FCSTD DOCUMENT  (FreeCAD 0.20R29410 (Git))
Label: lightModuleV2_2023_08_15
License: All rights reserved
LicenseURL: http://en.wikipedia.org/wiki/All_rights_reserved
objects: Part::Cylinder×122, Part::Feature×114, Part::MultiFuse×90, Sketcher::SketchObject×51, Part::Cut×49, Part::Extrusion×35, App::Part×14, Part::Box×12, Part::Fillet×11, Part::FeaturePython×10, Part::Loft×8, Part::Sphere×4, Mesh::Feature×2, Part::Compound×1, Part::Cone×1, Part::Compound2×1
note: 508 computed .brp shape members not serialized (recipe doc carries the construction recipe); baked Part::Feature solids carry a one-line shape summary decoded from their .brp

FEATURE [Mesh::Feature] Odroid_H004  label="Odroid-H004"
  Placement = pos=(15,-110,-70) rot=(0.57735,-0.57735,0.57735;4.18879rad)
FEATURE [Sketcher::SketchObject] Sketch  label="top"
  FullyConstrained = true
  sketch-geometry (24):
    g0: Circle CenterX=0 CenterY=-150 CenterZ=0 NormalX=0 NormalY=0 NormalZ=1 AngleXU=0 Radius=98
    g1: Circle CenterX=-92 CenterY=-150 CenterZ=0 NormalX=0 NormalY=0 NormalZ=1 AngleXU=0 Radius=2
    g2: Circle CenterX=-57 CenterY=-115 CenterZ=0 NormalX=0 NormalY=0 NormalZ=1 AngleXU=0 Radius=2
    g3: Circle CenterX=-22 CenterY=-150 CenterZ=0 NormalX=0 NormalY=0 NormalZ=1 AngleXU=0 Radius=2
    g4: Circle CenterX=-57 CenterY=-185 CenterZ=0 NormalX=0 NormalY=0 NormalZ=1 AngleXU=0 Radius=2
    g5: Circle CenterX=0 CenterY=-172 CenterZ=0 NormalX=0 NormalY=0 NormalZ=1 AngleXU=0 Radius=2
    g6: Circle CenterX=0 CenterY=-242 CenterZ=0 NormalX=0 NormalY=0 NormalZ=1 AngleXU=0 Radius=2
    g7: Circle CenterX=-35 CenterY=-207 CenterZ=0 NormalX=0 NormalY=0 NormalZ=1 AngleXU=0 Radius=2
    g8: Circle CenterX=35 CenterY=-207 CenterZ=0 NormalX=0 NormalY=0 NormalZ=1 AngleXU=0 Radius=2
    g9: Circle CenterX=57 CenterY=-185 CenterZ=0 NormalX=0 NormalY=0 NormalZ=1 AngleXU=0 Radius=2
    g10: Circle CenterX=22 CenterY=-150 CenterZ=0 NormalX=0 NormalY=0 NormalZ=1 AngleXU=0 Radius=2
    g11: Circle CenterX=57 CenterY=-115 CenterZ=0 NormalX=0 NormalY=0 NormalZ=1 AngleXU=0 Radius=2
    g12: Circle CenterX=92 CenterY=-150 CenterZ=0 NormalX=0 NormalY=0 NormalZ=1 AngleXU=0 Radius=2
    g13: Circle CenterX=0 CenterY=-58 CenterZ=0 NormalX=0 NormalY=0 NormalZ=1 AngleXU=0 Radius=2
    g14: Circle CenterX=0 CenterY=-207 CenterZ=0 NormalX=0 NormalY=0 NormalZ=1 AngleXU=0 Radius=25
    g15: Circle CenterX=57 CenterY=-150 CenterZ=0 NormalX=0 NormalY=0 NormalZ=1 AngleXU=0 Radius=25
    g16: Circle CenterX=0 CenterY=-93 CenterZ=0 NormalX=0 NormalY=0 NormalZ=1 AngleXU=0 Radius=25
    g17: Circle CenterX=-35 CenterY=-93 CenterZ=0 NormalX=0 NormalY=0 NormalZ=1 AngleXU=0 Radius=2
    g18: Circle CenterX=35 CenterY=-93 CenterZ=0 NormalX=0 NormalY=0 NormalZ=1 AngleXU=0 Radius=2
    g19: Circle CenterX=0 CenterY=-128 CenterZ=0 NormalX=0 NormalY=0 NormalZ=1 AngleXU=0 Radius=2
    g20: LineSegment StartX=-75.25 StartY=-129.25 StartZ=0 EndX=-38.75 EndY=-129.25 EndZ=0
    g21: LineSegment StartX=-38.75 StartY=-129.25 StartZ=0 EndX=-38.75 EndY=-170.75 EndZ=0
    g22: LineSegment StartX=-38.75 StartY=-170.75 StartZ=0 EndX=-75.25 EndY=-170.75 EndZ=0
    g23: LineSegment StartX=-75.25 StartY=-170.75 StartZ=0 EndX=-75.25 EndY=-129.25 EndZ=0
  constraints (72):
    c: PointOnObject(g0,g-2)
    c: Radius(g0) = 98
    c: DistanceY(g0) = -150
    c: PointOnObject(g5,g-2)
    c: PointOnObject(g6,g-2)
    c: PointOnObject(g13,g-2)
    c: PointOnObject(g19,g-2)
    c: Equal(g6,g7)
    c: Equal(g6,g4)
    c: Equal(g6,g1)
    c: Equal(g6,g2)
    c: Equal(g6,g3)
    c: Equal(g6,g19)
    c: Equal(g6,g5)
    c: Equal(g6,g8)
    c: Equal(g6,g9)
    c: Equal(g6,g10)
    c: Equal(g6,g12)
    c: Equal(g6,g11)
    c: Equal(g6,g17)
    c: Equal(g6,g18)
    c: Equal(g6,g13)
    c: Radius(g6) = 2
    c: DistanceY(g12,g0) = 0
    c: DistanceY(g10,g0) = 0
    c: DistanceY(g0,g3) = 0
    c: DistanceY(g1,g3) = 0
    c: Equal(g15,g14)
    c: Equal(g15,g16)
    c: Radius(g15) = 25
    c: Coincident(g20,g21)
    c: Coincident(g21,g22)
    c: Coincident(g22,g23)
    c: Coincident(g23,g20)
    c: Horizontal(g20)
    c: Horizontal(g22)
    c: Vertical(g21)
    c: Vertical(g23)
    c: DistanceX(g20) = -38.75
    c: DistanceY(g0,g20) = 20.75
    c: DistanceY(g21,g0) = 20.75
    c: DistanceX(g22,g0) = 75.25
    c: DistanceX(g14,g0) = 0
    c: DistanceX(g0,g15) = 57
    c: DistanceY(g15,g0) = 0
    c: DistanceY(g0,g16) = 57
    c: DistanceX(g16,g0) = 0
    c: DistanceX(g0,g10) = 22
    c: DistanceX(g3,g0) = 22
    c: DistanceX(g1,g0) = 92
    c: DistanceX(g15,g12) = 35
    c: DistanceX(g16,g18) = 35
    c: DistanceX(g17,g16) = 35
    c: DistanceX(g7,g14) = 35
    c: DistanceX(g14,g8) = 35
    c: DistanceX(g9,g15) = 0
    c: DistanceX(g15,g11) = 0
    c: DistanceX(g2,g0) = 57
    c: DistanceY(g18,g16) = 0
    c: DistanceY(g16,g17) = 0
    c: DistanceY(g19,g16) = 35
    c: DistanceY(g16,g13) = 35
    c: DistanceY(g4,g0) = 35
    c: DistanceY(g0,g2) = 35
    c: DistanceY(g14,g5) = 35
    c: DistanceY(g6,g14) = 35
    c: DistanceY(g8,g14) = 0
    c: DistanceY(g14,g7) = 0
    c: DistanceY(g9,g15) = 35
    c: DistanceY(g15,g11) = 35
    c: DistanceX(g4,g2) = 0
    c: DistanceY(g14,g0) = 57
FEATURE [Part::Cylinder] Cylinder036
  Angle = 360
  AttacherType = Attacher::AttachEngine3D
  FirstAngle = 0
  Height = 10
  Placement = pos=(0,-21,0) rot=(0,0,1;0rad)
  Radius = 2
  SecondAngle = 0
FEATURE [Part::Cylinder] Cylinder037
  Angle = 360
  AttacherType = Attacher::AttachEngine3D
  FirstAngle = 0
  Height = 10
  Placement = pos=(20,-21,0) rot=(0,0,1;0rad)
  Radius = 2
  SecondAngle = 0
FEATURE [Part::Cylinder] Cylinder038
  Angle = 360
  AttacherType = Attacher::AttachEngine3D
  FirstAngle = 0
  Height = 10
  Placement = pos=(0,-21,0) rot=(0,0,1;0rad)
  Radius = 2
  SecondAngle = 0
FEATURE [Part::Cylinder] Cylinder039
  Angle = 360
  AttacherType = Attacher::AttachEngine3D
  FirstAngle = 0
  Height = 10
  Placement = pos=(20,-21,0) rot=(0,0,1;0rad)
  Radius = 2
  SecondAngle = 0
FEATURE [Part::Cylinder] Cylinder040  label="base002"
  Angle = 360
  AttacherType = Attacher::AttachEngine3D
  FirstAngle = 0
  Height = 5
  Placement = pos=(5,0,70) rot=(0,0,1;0rad)
  Radius = 40
  SecondAngle = 0
FEATURE [Part::Cylinder] Cylinder041  label="baseCut001"
  Angle = 360
  AttacherType = Attacher::AttachEngine3D
  FirstAngle = 0
  Height = 7
  Placement = pos=(5,0,74) rot=(0,0,1;0rad)
  Radius = 24
  SecondAngle = 0
FEATURE [Part::Cylinder] Cylinder042  label="wireCUt002"
  Angle = 360
  AttacherType = Attacher::AttachEngine3D
  FirstAngle = 0
  Height = 10
  Placement = pos=(-5,0,70) rot=(0,0,1;0rad)
  Radius = 2
  SecondAngle = 0
FEATURE [Part::Cylinder] Cylinder043  label="wireCUt003"
  Angle = 360
  AttacherType = Attacher::AttachEngine3D
  FirstAngle = 0
  Height = 10
  Placement = pos=(15,0,70) rot=(0,0,1;0rad)
  Radius = 2
  SecondAngle = 0
FEATURE [Part::Cylinder] Cylinder044  label="m3Cuts002"
  Angle = 360
  AttacherType = Attacher::AttachEngine3D
  FirstAngle = 0
  Height = 10
  Placement = pos=(5,-9,70) rot=(0,0,1;0rad)
  Radius = 1.75
  SecondAngle = 0
FEATURE [Part::Cylinder] Cylinder045  label="m3Cuts003"
  Angle = 360
  AttacherType = Attacher::AttachEngine3D
  FirstAngle = 0
  Height = 10
  Placement = pos=(5,9,70) rot=(0,0,1;0rad)
  Radius = 1.75
  SecondAngle = 0
FEATURE [Part::Cylinder] Cylinder046  label="m2HeatSetInsets004"
  Angle = 360
  AttacherType = Attacher::AttachEngine3D
  FirstAngle = 0
  Height = 10
  Placement = pos=(-30,0,65) rot=(0,0,1;0rad)
  Radius = 1.6
  SecondAngle = 0
FEATURE [Part::Cylinder] Cylinder047  label="m2HeatSetInsets005"
  Angle = 360
  AttacherType = Attacher::AttachEngine3D
  FirstAngle = 0
  Height = 10
  Placement = pos=(40,0,65) rot=(0,0,1;0rad)
  Radius = 1.6
  SecondAngle = 0
FEATURE [Part::Cylinder] Cylinder048  label="m2HeatSetInsets006"
  Angle = 360
  AttacherType = Attacher::AttachEngine3D
  FirstAngle = 0
  Height = 10
  Placement = pos=(5,35,65) rot=(0,0,1;0rad)
  Radius = 1.6
  SecondAngle = 0
FEATURE [Part::Cylinder] Cylinder049  label="m2HeatSetInsets007"
  Angle = 360
  AttacherType = Attacher::AttachEngine3D
  FirstAngle = 0
  Height = 10
  Placement = pos=(5,-35,65) rot=(0,0,1;0rad)
  Radius = 1.6
  SecondAngle = 0
FEATURE [Part::MultiFuse] Fusion014  label="m3HeatSetCuts003"
  Placement = pos=(-5,38.5,70) rot=(0,0,1;0rad)
  Shapes = -> [Cylinder037,Cylinder036]
FEATURE [Part::MultiFuse] Fusion015  label="m3HeatSetCuts004"
  Placement = pos=(-5,3.5,70) rot=(0,0,1;0rad)
  Shapes = -> [Cylinder039,Cylinder038]
FEATURE [Part::MultiFuse] Fusion016  label="m3HeatSetCuts005"
  Shapes = -> [Fusion015,Fusion014]
FEATURE [Part::MultiFuse] Fusion017  label="wireCuts001"
  Shapes = -> [Cylinder042,Cylinder043]
FEATURE [Part::MultiFuse] Fusion018  label="m3Cute001"
  Shapes = -> [Cylinder044,Cylinder045]
FEATURE [Part::MultiFuse] Fusion019  label="baseCUts001"
  Shapes = -> [Fusion016,Fusion017,Fusion018]
FEATURE [Part::MultiFuse] Fusion021
  Shapes = -> [Cylinder046,Cylinder047,Cylinder048,Cylinder049]
FEATURE [Part::Sphere] Sphere002  label="SphereBase001"
  Angle1 = 0
  Angle2 = 12
  Angle3 = 360
  AttacherType = Attacher::AttachEngine3D
  Placement = pos=(5,0,74) rot=(0,0,1;0rad)
  Radius = 29
FEATURE [Part::Cut] Cut006
  Base = -> Sphere002
  Tool = -> Cylinder041
FEATURE [Part::MultiFuse] Fusion020  label="base003"
  Shapes = -> [Cylinder040,Cut006]
FEATURE [Part::Cut] Cut007
  Base = -> Fusion020
  Tool = -> Fusion019
FEATURE [Part::Cut] Cut008  label="lightModule001"
  Base = -> Cut007
  Placement = pos=(-5,-207,0) rot=(0,1,0;0rad)
  Tool = -> Fusion021
FEATURE [Part::Box] Box005  label="as7265x"
  AttacherType = Attacher::AttachEngine3D
  Height = 2
  Length = 36
  Placement = pos=(-75,-170.5,110) rot=(0,0,1;0rad)
  Width = 41
FEATURE [Part::Cylinder] Cylinder050
  Angle = 360
  AttacherType = Attacher::AttachEngine3D
  FirstAngle = 0
  Height = 10
  Placement = pos=(0,-21,0) rot=(0,0,1;0rad)
  Radius = 2
  SecondAngle = 0
FEATURE [Part::Cylinder] Cylinder051
  Angle = 360
  AttacherType = Attacher::AttachEngine3D
  FirstAngle = 0
  Height = 10
  Placement = pos=(20,-21,0) rot=(0,0,1;0rad)
  Radius = 2
  SecondAngle = 0
FEATURE [Part::Cylinder] Cylinder052
  Angle = 360
  AttacherType = Attacher::AttachEngine3D
  FirstAngle = 0
  Height = 10
  Placement = pos=(0,-21,0) rot=(0,0,1;0rad)
  Radius = 2
  SecondAngle = 0
FEATURE [Part::Cylinder] Cylinder053
  Angle = 360
  AttacherType = Attacher::AttachEngine3D
  FirstAngle = 0
  Height = 10
  Placement = pos=(20,-21,0) rot=(0,0,1;0rad)
  Radius = 2
  SecondAngle = 0
FEATURE [Part::Cylinder] Cylinder054  label="base004"
  Angle = 360
  AttacherType = Attacher::AttachEngine3D
  FirstAngle = 0
  Height = 5
  Placement = pos=(5,0,70) rot=(0,0,1;0rad)
  Radius = 40
  SecondAngle = 0
FEATURE [Part::Cylinder] Cylinder055  label="baseCut002"
  Angle = 360
  AttacherType = Attacher::AttachEngine3D
  FirstAngle = 0
  Height = 7
  Placement = pos=(5,0,74) rot=(0,0,1;0rad)
  Radius = 24
  SecondAngle = 0
FEATURE [Part::Cylinder] Cylinder056  label="wireCUt004"
  Angle = 360
  AttacherType = Attacher::AttachEngine3D
  FirstAngle = 0
  Height = 10
  Placement = pos=(-5,0,70) rot=(0,0,1;0rad)
  Radius = 2
  SecondAngle = 0
FEATURE [Part::Cylinder] Cylinder057  label="wireCUt005"
  Angle = 360
  AttacherType = Attacher::AttachEngine3D
  FirstAngle = 0
  Height = 10
  Placement = pos=(15,0,70) rot=(0,0,1;0rad)
  Radius = 2
  SecondAngle = 0
FEATURE [Part::Cylinder] Cylinder058  label="m3Cuts004"
  Angle = 360
  AttacherType = Attacher::AttachEngine3D
  FirstAngle = 0
  Height = 10
  Placement = pos=(5,-9,70) rot=(0,0,1;0rad)
  Radius = 1.75
  SecondAngle = 0
FEATURE [Part::Cylinder] Cylinder059  label="m3Cuts005"
  Angle = 360
  AttacherType = Attacher::AttachEngine3D
  FirstAngle = 0
  Height = 10
  Placement = pos=(5,9,70) rot=(0,0,1;0rad)
  Radius = 1.75
  SecondAngle = 0
FEATURE [Part::Cylinder] Cylinder060  label="m2HeatSetInsets008"
  Angle = 360
  AttacherType = Attacher::AttachEngine3D
  FirstAngle = 0
  Height = 10
  Placement = pos=(-30,0,65) rot=(0,0,1;0rad)
  Radius = 1.6
  SecondAngle = 0
FEATURE [Part::Cylinder] Cylinder061  label="m2HeatSetInsets009"
  Angle = 360
  AttacherType = Attacher::AttachEngine3D
  FirstAngle = 0
  Height = 10
  Placement = pos=(40,0,65) rot=(0,0,1;0rad)
  Radius = 1.6
  SecondAngle = 0
FEATURE [Part::Cylinder] Cylinder062  label="m2HeatSetInsets010"
  Angle = 360
  AttacherType = Attacher::AttachEngine3D
  FirstAngle = 0
  Height = 10
  Placement = pos=(5,35,65) rot=(0,0,1;0rad)
  Radius = 1.6
  SecondAngle = 0
FEATURE [Part::Cylinder] Cylinder063  label="m2HeatSetInsets011"
  Angle = 360
  AttacherType = Attacher::AttachEngine3D
  FirstAngle = 0
  Height = 10
  Placement = pos=(5,-35,65) rot=(0,0,1;0rad)
  Radius = 1.6
  SecondAngle = 0
FEATURE [Part::MultiFuse] Fusion022  label="m3HeatSetCuts006"
  Placement = pos=(-5,38.5,70) rot=(0,0,1;0rad)
  Shapes = -> [Cylinder051,Cylinder050]
FEATURE [Part::MultiFuse] Fusion023  label="m3HeatSetCuts007"
  Placement = pos=(-5,3.5,70) rot=(0,0,1;0rad)
  Shapes = -> [Cylinder053,Cylinder052]
FEATURE [Part::MultiFuse] Fusion024  label="m3HeatSetCuts008"
  Shapes = -> [Fusion023,Fusion022]
FEATURE [Part::MultiFuse] Fusion025  label="wireCuts002"
  Shapes = -> [Cylinder056,Cylinder057]
FEATURE [Part::MultiFuse] Fusion026  label="m3Cute002"
  Shapes = -> [Cylinder058,Cylinder059]
FEATURE [Part::MultiFuse] Fusion027  label="baseCUts002"
  Shapes = -> [Fusion024,Fusion025,Fusion026]
FEATURE [Part::MultiFuse] Fusion029
  Shapes = -> [Cylinder060,Cylinder061,Cylinder062,Cylinder063]
FEATURE [Part::Sphere] Sphere003  label="SphereBase002"
  Angle1 = 0
  Angle2 = 12
  Angle3 = 360
  AttacherType = Attacher::AttachEngine3D
  Placement = pos=(5,0,74) rot=(0,0,1;0rad)
  Radius = 29
FEATURE [Part::Cut] Cut009
  Base = -> Sphere003
  Tool = -> Cylinder055
FEATURE [Part::MultiFuse] Fusion028  label="base005"
  Shapes = -> [Cylinder054,Cut009]
FEATURE [Part::Cut] Cut010
  Base = -> Fusion028
  Tool = -> Fusion027
FEATURE [Part::Cut] Cut011  label="lightModule002"
  Base = -> Cut010
  Placement = pos=(-62,-150,0) rot=(0,1,0;0rad)
  Tool = -> Fusion029
FEATURE [Part::Cylinder] Cylinder064
  Angle = 360
  AttacherType = Attacher::AttachEngine3D
  FirstAngle = 0
  Height = 10
  Placement = pos=(0,-21,0) rot=(0,0,1;0rad)
  Radius = 2
  SecondAngle = 0
FEATURE [Part::Cylinder] Cylinder065
  Angle = 360
  AttacherType = Attacher::AttachEngine3D
  FirstAngle = 0
  Height = 10
  Placement = pos=(20,-21,0) rot=(0,0,1;0rad)
  Radius = 2
  SecondAngle = 0
FEATURE [Part::Cylinder] Cylinder066
  Angle = 360
  AttacherType = Attacher::AttachEngine3D
  FirstAngle = 0
  Height = 10
  Placement = pos=(0,-21,0) rot=(0,0,1;0rad)
  Radius = 2
  SecondAngle = 0
FEATURE [Part::Cylinder] Cylinder067
  Angle = 360
  AttacherType = Attacher::AttachEngine3D
  FirstAngle = 0
  Height = 10
  Placement = pos=(20,-21,0) rot=(0,0,1;0rad)
  Radius = 2
  SecondAngle = 0
FEATURE [Part::Cylinder] Cylinder068  label="base006"
  Angle = 360
  AttacherType = Attacher::AttachEngine3D
  FirstAngle = 0
  Height = 5
  Placement = pos=(5,0,70) rot=(0,0,1;0rad)
  Radius = 40
  SecondAngle = 0
FEATURE [Part::Cylinder] Cylinder069  label="baseCut003"
  Angle = 360
  AttacherType = Attacher::AttachEngine3D
  FirstAngle = 0
  Height = 7
  Placement = pos=(5,0,74) rot=(0,0,1;0rad)
  Radius = 24
  SecondAngle = 0
FEATURE [Part::Cylinder] Cylinder070  label="wireCUt006"
  Angle = 360
  AttacherType = Attacher::AttachEngine3D
  FirstAngle = 0
  Height = 10
  Placement = pos=(-5,0,70) rot=(0,0,1;0rad)
  Radius = 2
  SecondAngle = 0
FEATURE [Part::Cylinder] Cylinder071  label="wireCUt007"
  Angle = 360
  AttacherType = Attacher::AttachEngine3D
  FirstAngle = 0
  Height = 10
  Placement = pos=(15,0,70) rot=(0,0,1;0rad)
  Radius = 2
  SecondAngle = 0
FEATURE [Part::Cylinder] Cylinder072  label="m3Cuts006"
  Angle = 360
  AttacherType = Attacher::AttachEngine3D
  FirstAngle = 0
  Height = 10
  Placement = pos=(5,-9,70) rot=(0,0,1;0rad)
  Radius = 1.75
  SecondAngle = 0
FEATURE [Part::Cylinder] Cylinder073  label="m3Cuts007"
  Angle = 360
  AttacherType = Attacher::AttachEngine3D
  FirstAngle = 0
  Height = 10
  Placement = pos=(5,9,70) rot=(0,0,1;0rad)
  Radius = 1.75
  SecondAngle = 0
FEATURE [Part::Cylinder] Cylinder074  label="m2HeatSetInsets012"
  Angle = 360
  AttacherType = Attacher::AttachEngine3D
  FirstAngle = 0
  Height = 10
  Placement = pos=(-30,0,65) rot=(0,0,1;0rad)
  Radius = 1.6
  SecondAngle = 0
FEATURE [Part::Cylinder] Cylinder075  label="m2HeatSetInsets013"
  Angle = 360
  AttacherType = Attacher::AttachEngine3D
  FirstAngle = 0
  Height = 10
  Placement = pos=(40,0,65) rot=(0,0,1;0rad)
  Radius = 1.6
  SecondAngle = 0
FEATURE [Part::Cylinder] Cylinder076  label="m2HeatSetInsets014"
  Angle = 360
  AttacherType = Attacher::AttachEngine3D
  FirstAngle = 0
  Height = 10
  Placement = pos=(5,35,65) rot=(0,0,1;0rad)
  Radius = 1.6
  SecondAngle = 0
FEATURE [Part::Cylinder] Cylinder077  label="m2HeatSetInsets015"
  Angle = 360
  AttacherType = Attacher::AttachEngine3D
  FirstAngle = 0
  Height = 10
  Placement = pos=(5,-35,65) rot=(0,0,1;0rad)
  Radius = 1.6
  SecondAngle = 0
FEATURE [Part::MultiFuse] Fusion030  label="m3HeatSetCuts009"
  Placement = pos=(-5,38.5,70) rot=(0,0,1;0rad)
  Shapes = -> [Cylinder065,Cylinder064]
FEATURE [Part::MultiFuse] Fusion031  label="m3HeatSetCuts010"
  Placement = pos=(-5,3.5,70) rot=(0,0,1;0rad)
  Shapes = -> [Cylinder067,Cylinder066]
FEATURE [Part::MultiFuse] Fusion032  label="m3HeatSetCuts011"
  Shapes = -> [Fusion031,Fusion030]
FEATURE [Part::MultiFuse] Fusion033  label="wireCuts003"
  Shapes = -> [Cylinder070,Cylinder071]
FEATURE [Part::MultiFuse] Fusion034  label="m3Cute003"
  Shapes = -> [Cylinder072,Cylinder073]
FEATURE [Part::MultiFuse] Fusion035  label="baseCUts003"
  Shapes = -> [Fusion032,Fusion033,Fusion034]
FEATURE [Part::MultiFuse] Fusion037
  Shapes = -> [Cylinder074,Cylinder075,Cylinder076,Cylinder077]
FEATURE [Part::Sphere] Sphere004  label="SphereBase003"
  Angle1 = 0
  Angle2 = 12
  Angle3 = 360
  AttacherType = Attacher::AttachEngine3D
  Placement = pos=(5,0,74) rot=(0,0,1;0rad)
  Radius = 29
FEATURE [Part::Cut] Cut012
  Base = -> Sphere004
  Tool = -> Cylinder069
FEATURE [Part::MultiFuse] Fusion036  label="base007"
  Shapes = -> [Cylinder068,Cut012]
FEATURE [Part::Cut] Cut013
  Base = -> Fusion036
  Tool = -> Fusion035
FEATURE [Part::Cut] Cut014  label="lightModule003"
  Base = -> Cut013
  Placement = pos=(52,-150,0) rot=(0,1,0;0rad)
  Tool = -> Fusion037
FEATURE [Part::Cylinder] Cylinder078
  Angle = 360
  AttacherType = Attacher::AttachEngine3D
  FirstAngle = 0
  Height = 10
  Placement = pos=(0,-21,0) rot=(0,0,1;0rad)
  Radius = 2
  SecondAngle = 0
FEATURE [Part::Cylinder] Cylinder079
  Angle = 360
  AttacherType = Attacher::AttachEngine3D
  FirstAngle = 0
  Height = 10
  Placement = pos=(20,-21,0) rot=(0,0,1;0rad)
  Radius = 2
  SecondAngle = 0
FEATURE [Part::Cylinder] Cylinder080
  Angle = 360
  AttacherType = Attacher::AttachEngine3D
  FirstAngle = 0
  Height = 10
  Placement = pos=(0,-21,0) rot=(0,0,1;0rad)
  Radius = 2
  SecondAngle = 0
FEATURE [Part::Cylinder] Cylinder081
  Angle = 360
  AttacherType = Attacher::AttachEngine3D
  FirstAngle = 0
  Height = 10
  Placement = pos=(20,-21,0) rot=(0,0,1;0rad)
  Radius = 2
  SecondAngle = 0
FEATURE [Part::Cylinder] Cylinder082  label="base008"
  Angle = 360
  AttacherType = Attacher::AttachEngine3D
  FirstAngle = 0
  Height = 5
  Placement = pos=(5,0,70) rot=(0,0,1;0rad)
  Radius = 40
  SecondAngle = 0
FEATURE [Part::Cylinder] Cylinder083  label="baseCut004"
  Angle = 360
  AttacherType = Attacher::AttachEngine3D
  FirstAngle = 0
  Height = 7
  Placement = pos=(5,0,74) rot=(0,0,1;0rad)
  Radius = 24
  SecondAngle = 0
FEATURE [Part::Cylinder] Cylinder084  label="wireCUt008"
  Angle = 360
  AttacherType = Attacher::AttachEngine3D
  FirstAngle = 0
  Height = 10
  Placement = pos=(-5,0,70) rot=(0,0,1;0rad)
  Radius = 2
  SecondAngle = 0
FEATURE [Part::Cylinder] Cylinder085  label="wireCUt009"
  Angle = 360
  AttacherType = Attacher::AttachEngine3D
  FirstAngle = 0
  Height = 10
  Placement = pos=(15,0,70) rot=(0,0,1;0rad)
  Radius = 2
  SecondAngle = 0
FEATURE [Part::Cylinder] Cylinder086  label="m3Cuts008"
  Angle = 360
  AttacherType = Attacher::AttachEngine3D
  FirstAngle = 0
  Height = 10
  Placement = pos=(5,-9,70) rot=(0,0,1;0rad)
  Radius = 1.75
  SecondAngle = 0
FEATURE [Part::Cylinder] Cylinder087  label="m3Cuts009"
  Angle = 360
  AttacherType = Attacher::AttachEngine3D
  FirstAngle = 0
  Height = 10
  Placement = pos=(5,9,70) rot=(0,0,1;0rad)
  Radius = 1.75
  SecondAngle = 0
FEATURE [Part::Cylinder] Cylinder088  label="m2HeatSetInsets016"
  Angle = 360
  AttacherType = Attacher::AttachEngine3D
  FirstAngle = 0
  Height = 10
  Placement = pos=(-30,0,65) rot=(0,0,1;0rad)
  Radius = 1.6
  SecondAngle = 0
FEATURE [Part::Cylinder] Cylinder089  label="m2HeatSetInsets017"
  Angle = 360
  AttacherType = Attacher::AttachEngine3D
  FirstAngle = 0
  Height = 10
  Placement = pos=(40,0,65) rot=(0,0,1;0rad)
  Radius = 1.6
  SecondAngle = 0
FEATURE [Part::Cylinder] Cylinder090  label="m2HeatSetInsets018"
  Angle = 360
  AttacherType = Attacher::AttachEngine3D
  FirstAngle = 0
  Height = 10
  Placement = pos=(5,35,65) rot=(0,0,1;0rad)
  Radius = 1.6
  SecondAngle = 0
FEATURE [Part::Cylinder] Cylinder091  label="m2HeatSetInsets019"
  Angle = 360
  AttacherType = Attacher::AttachEngine3D
  FirstAngle = 0
  Height = 10
  Placement = pos=(5,-35,65) rot=(0,0,1;0rad)
  Radius = 1.6
  SecondAngle = 0
FEATURE [Part::MultiFuse] Fusion038  label="m3HeatSetCuts012"
  Placement = pos=(-5,38.5,70) rot=(0,0,1;0rad)
  Shapes = -> [Cylinder079,Cylinder078]
FEATURE [Part::MultiFuse] Fusion039  label="m3HeatSetCuts013"
  Placement = pos=(-5,3.5,70) rot=(0,0,1;0rad)
  Shapes = -> [Cylinder081,Cylinder080]
FEATURE [Part::MultiFuse] Fusion040  label="m3HeatSetCuts014"
  Shapes = -> [Fusion039,Fusion038]
FEATURE [Part::MultiFuse] Fusion041  label="wireCuts004"
  Shapes = -> [Cylinder084,Cylinder085]
FEATURE [Part::MultiFuse] Fusion042  label="m3Cute004"
  Shapes = -> [Cylinder086,Cylinder087]
FEATURE [Part::MultiFuse] Fusion043  label="baseCUts004"
  Shapes = -> [Fusion040,Fusion041,Fusion042]
FEATURE [Part::MultiFuse] Fusion045
  Shapes = -> [Cylinder088,Cylinder089,Cylinder090,Cylinder091]
FEATURE [Part::Sphere] Sphere005  label="SphereBase004"
  Angle1 = 0
  Angle2 = 12
  Angle3 = 360
  AttacherType = Attacher::AttachEngine3D
  Placement = pos=(5,0,74) rot=(0,0,1;0rad)
  Radius = 29
FEATURE [Part::Cut] Cut015
  Base = -> Sphere005
  Tool = -> Cylinder083
FEATURE [Part::MultiFuse] Fusion044  label="base009"
  Shapes = -> [Cylinder082,Cut015]
FEATURE [Part::Cut] Cut016
  Base = -> Fusion044
  Tool = -> Fusion043
FEATURE [Part::Cut] Cut017  label="lightModule004"
  Base = -> Cut016
  Placement = pos=(-5,-93,0) rot=(0,1,0;0rad)
  Tool = -> Fusion045
FEATURE [Part::MultiFuse] Fusion  label="lightModules"
  Placement = pos=(0,0,30) rot=(0,0,1;0rad)
  Shapes = -> [Cut008,Cut011,Cut014,Cut017]
FEATURE [Part::Extrusion] Extrude  label="top001"
  Base = -> Sketch
  Dir = (0,0,1)
  DirMode = 2
  FaceMakerClass = Part::FaceMakerBullseye
  LengthFwd = 5
  LengthRev = 0
  Placement = pos=(0,0,100) rot=(0,0,1;0rad)
  Solid = true
  Symmetric = false
FEATURE [Part::Feature] Part__Feature  label="elpCamera"
  Placement = pos=(57,-150,90) rot=(0,0,1;0rad)
  shape: bbox 38 x 38 x 25.12 mm, 164 faces (baked)
FEATURE [Part::FeaturePython] Tube  label="tube001"  # WARN: FeaturePython — macro-defined, semantics opaque (R4)
  AttacherType = Attacher::AttachEngine3D
  Height = 20
  InnerRadius = 94
  OuterRadius = 98
  Placement = pos=(0,-150,80) rot=(0,0,1;0rad)
FEATURE [Part::Feature] Part__Feature010  label="veml6075_sensor"
  Placement = pos=(0,-92,105) rot=(0,0,1;0rad)
  shape: bbox 15.31 x 17.01 x 46.02 mm, 450 faces (baked)
FEATURE [Sketcher::SketchObject] Sketch001
  FullyConstrained = true
  Placement = pos=(0,0,105) rot=(0,0,1;0rad)
  sketch-geometry (14):
    g0: Circle CenterX=0 CenterY=-93 CenterZ=0 NormalX=0 NormalY=0 NormalZ=1 AngleXU=0 Radius=25
    g1: Circle CenterX=0 CenterY=-93 CenterZ=0 NormalX=0 NormalY=0 NormalZ=1 AngleXU=0 Radius=26.5
    g2: Circle CenterX=57 CenterY=-150 CenterZ=0 NormalX=0 NormalY=0 NormalZ=1 AngleXU=0 Radius=25
    g3: Circle CenterX=57 CenterY=-150 CenterZ=0 NormalX=0 NormalY=0 NormalZ=1 AngleXU=0 Radius=26.5
    g4: Circle CenterX=0 CenterY=-207 CenterZ=0 NormalX=0 NormalY=0 NormalZ=1 AngleXU=0 Radius=25
    g5: Circle CenterX=0 CenterY=-207 CenterZ=0 NormalX=0 NormalY=0 NormalZ=1 AngleXU=0 Radius=26.5
    g6: LineSegment StartX=-75.25 StartY=-129.25 StartZ=0 EndX=-38.75 EndY=-129.25 EndZ=0
    g7: LineSegment StartX=-38.75 StartY=-129.25 StartZ=0 EndX=-38.75 EndY=-170.75 EndZ=0
    g8: LineSegment StartX=-38.75 StartY=-170.75 StartZ=0 EndX=-75.25 EndY=-170.75 EndZ=0
    g9: LineSegment StartX=-75.25 StartY=-170.75 StartZ=0 EndX=-75.25 EndY=-129.25 EndZ=0
    g10: LineSegment StartX=-75.7 StartY=-128.8 StartZ=0 EndX=-38.3 EndY=-128.8 EndZ=0
    g11: LineSegment StartX=-38.3 StartY=-128.8 StartZ=0 EndX=-38.3 EndY=-171.2 EndZ=0
    g12: LineSegment StartX=-38.3 StartY=-171.2 StartZ=0 EndX=-75.7 EndY=-171.2 EndZ=0
    g13: LineSegment StartX=-75.7 StartY=-171.2 StartZ=0 EndX=-75.7 EndY=-128.8 EndZ=0
  constraints (39):
    c: PointOnObject(g0,g-2)
    c: Coincident(g1,g0)
    c: Coincident(g3,g2)
    c: PointOnObject(g4,g-2)
    c: Coincident(g5,g4)
    c: Coincident(g6,g7)
    c: Coincident(g7,g8)
    c: Coincident(g8,g9)
    c: Coincident(g9,g6)
    c: Horizontal(g6)
    c: Horizontal(g8)
    c: Vertical(g7)
    c: Vertical(g9)
    c: DistanceY(g0) = -93
    c: DistanceY(g2) = -150
    c: DistanceX(g2) = 57
    c: Equal(g0,g2)
    c: Equal(g0,g4)
    c: Radius(g0) = 25
    c: Equal(g3,g1)
    c: Equal(g3,g5)
    c: Radius(g3) = 26.5
    c: DistanceY(g4) = -207
    c: DistanceY(g7) = -170.75
    c: DistanceX(g7) = -38.75
    c: DistanceX(g6) = -75.25
    c: DistanceY(g6) = -129.25
    c: Coincident(g10,g11)
    c: Coincident(g11,g12)
    c: Coincident(g12,g13)
    c: Coincident(g13,g10)
    c: Horizontal(g10)
    c: Horizontal(g12)
    c: Vertical(g11)
    c: Vertical(g13)
    c: DistanceY(g11,g7) = 0.45
    c: DistanceX(g7,g11) = 0.45
    c: DistanceX(g10,g6) = 0.45
    c: DistanceY(g6,g10) = 0.45
FEATURE [Part::Extrusion] Extrude001
  Base = -> Sketch001
  Dir = (0,0,1)
  DirMode = 2
  FaceMakerClass = Part::FaceMakerBullseye
  LengthFwd = 1
  LengthRev = 0
  Solid = true
  Symmetric = false
FEATURE [Part::MultiFuse] Fusion046  label="top002"
  Shapes = -> [Extrude001,Extrude]
FEATURE [Part::Cylinder] Cylinder
  Angle = 360
  AttacherType = Attacher::AttachEngine3D
  FirstAngle = 0
  Height = 300
  Placement = pos=(0,0,90) rot=(1,0,0;1.5708rad)
  Radius = 2.2
  SecondAngle = 0
FEATURE [Part::Cylinder] Cylinder092
  Angle = 360
  AttacherType = Attacher::AttachEngine3D
  FirstAngle = 0
  Height = 300
  Placement = pos=(-150,-150,90) rot=(0.57735,0.57735,0.57735;2.0944rad)
  Radius = 2.2
  SecondAngle = 0
FEATURE [Part::MultiFuse] Fusion047  label="m4Cuts"
  Shapes = -> [Cylinder092,Cylinder]
FEATURE [Part::Fillet] Fillet  label="top003"
  Base = -> Fusion046
  Edges = 1 edges r=2: [Edge3]
FEATURE [Part::Fillet] Fillet001  label="tube"
  Base = -> Tube
  Edges = 1 edges r=2: [Edge5]
FEATURE [Part::MultiFuse] Fusion048  label="top004"
  Shapes = -> [Fillet,Fillet001]
FEATURE [Part::Cut] Cut  label="top005"
  Base = -> Fusion048
  Tool = -> Fusion047
FEATURE [Part::Cylinder] Cylinder094  label="refModules"
  Angle = 360
  AttacherType = Attacher::AttachEngine3D
  FirstAngle = 0
  Height = 75
  Placement = pos=(0,-207,37) rot=(0,0,1;0rad)
  Radius = 3.75
  SecondAngle = 0
FEATURE [Part::Cylinder] Cylinder095  label="refModulesCoverCut"
  Angle = 360
  AttacherType = Attacher::AttachEngine3D
  FirstAngle = 0
  Height = 60
  Placement = pos=(0,-207,37) rot=(0,0,1;0rad)
  Radius = 4.5
  SecondAngle = 0
FEATURE [Sketcher::SketchObject] Sketch002
  FullyConstrained = true
  sketch-geometry (16):
    g0: Circle CenterX=-67 CenterY=-167.5 CenterZ=0 NormalX=0 NormalY=0 NormalZ=1 AngleXU=0 Radius=1.625
    g1: Circle CenterX=-47 CenterY=-167.5 CenterZ=0 NormalX=0 NormalY=0 NormalZ=1 AngleXU=0 Radius=1.625
    g2: Circle CenterX=-67 CenterY=-132.5 CenterZ=0 NormalX=0 NormalY=0 NormalZ=1 AngleXU=0 Radius=1.625
    g3: Circle CenterX=-47 CenterY=-132.5 CenterZ=0 NormalX=0 NormalY=0 NormalZ=1 AngleXU=0 Radius=1.625
    g4: LineSegment StartX=-62 StartY=-129.75 StartZ=0 EndX=-72 EndY=-129.75 EndZ=0
    g5: LineSegment StartX=-52 StartY=-129.75 StartZ=0 EndX=-42 EndY=-129.75 EndZ=0
    g6: LineSegment StartX=-72 StartY=-129.75 StartZ=0 EndX=-72 EndY=-170.25 EndZ=0
    g7: LineSegment StartX=-72 StartY=-170.25 StartZ=0 EndX=-62 EndY=-170.25 EndZ=0
    g8: LineSegment StartX=-62 StartY=-170.25 StartZ=0 EndX=-62 EndY=-155 EndZ=0
    g9: LineSegment StartX=-52 StartY=-155 StartZ=0 EndX=-52 EndY=-170.25 EndZ=0
    g10: LineSegment StartX=-52 StartY=-170.25 StartZ=0 EndX=-42 EndY=-170.25 EndZ=0
    g11: LineSegment StartX=-42 StartY=-170.25 StartZ=0 EndX=-42 EndY=-129.75 EndZ=0
    g12: LineSegment StartX=-62 StartY=-155 StartZ=0 EndX=-52 EndY=-155 EndZ=0
    g13: LineSegment StartX=-62 StartY=-129.75 StartZ=0 EndX=-62 EndY=-145 EndZ=0
    g14: LineSegment StartX=-62 StartY=-145 StartZ=0 EndX=-52 EndY=-145 EndZ=0
    g15: LineSegment StartX=-52 StartY=-145 StartZ=0 EndX=-52 EndY=-129.75 EndZ=0
  constraints (48):
    c: DistanceY(g2,g3) = 0
    c: DistanceX(g0,g2) = 0
    c: DistanceX(g1,g3) = 0
    c: DistanceX(g1) = -47
    c: DistanceY(g1) = -167.5
    c: DistanceX(g0,g1) = 20
    c: Horizontal(g4)
    c: Horizontal(g5)
    c: Vertical(g6)
    c: Coincident(g7,g6)
    c: Horizontal(g7)
    c: Coincident(g8,g7)
    c: Vertical(g9)
    c: Coincident(g10,g9)
    c: Horizontal(g10)
    c: Coincident(g11,g10)
    c: Vertical(g8)
    c: DistanceX(g4,g4) = 10
    c: DistanceX(g5,g5) = 10
    c: DistanceX(g6,g7) = 10
    c: DistanceX(g9,g10) = 10
    c: Vertical(g11)
    c: DistanceY(g7,g9) = 0
    c: DistanceY(g4,g5) = 0
    c: DistanceX(g6,g0) = 5
    c: DistanceX(g9,g1) = 5
    c: DistanceY(g2,g4) = 2.75
    c: Coincident(g4,g6)
    c: Coincident(g12,g8)
    c: Horizontal(g12)
    c: Coincident(g9,g12)
    c: Coincident(g13,g4)
    c: Vertical(g13)
    c: Coincident(g14,g13)
    c: Horizontal(g14)
    c: Coincident(g15,g14)
    c: Coincident(g15,g5)
    c: Vertical(g15)
    c: Coincident(g5,g11)
    c: DistanceY(g8,g13) = 10
    c: DistanceY(g13) = -145
    c: DistanceY(g7,g0) = 2.75
    c: Equal(g1,g0)
    c: Equal(g1,g2)
    c: Equal(g1,g3)
    c: Diameter(g1) = 3.25
    c: DistanceY(g1,g0) = 0
    c: DistanceY(g2) = -132.5
FEATURE [Sketcher::SketchObject] Sketch003
  FullyConstrained = true
  sketch-geometry (6):
    g0: Circle CenterX=74 CenterY=-167 CenterZ=0 NormalX=0 NormalY=0 NormalZ=1 AngleXU=0 Radius=1.65
    g1: Circle CenterX=40 CenterY=-167 CenterZ=0 NormalX=0 NormalY=0 NormalZ=1 AngleXU=0 Radius=1.65
    g2: Circle CenterX=40 CenterY=-133 CenterZ=0 NormalX=0 NormalY=0 NormalZ=1 AngleXU=0 Radius=1.65
    g3: Circle CenterX=74 CenterY=-133 CenterZ=0 NormalX=0 NormalY=0 NormalZ=1 AngleXU=0 Radius=1.65
    g4: Circle CenterX=57 CenterY=-150 CenterZ=0 NormalX=0 NormalY=0 NormalZ=1 AngleXU=0 Radius=27.5
    g5: Circle CenterX=57 CenterY=-150 CenterZ=0 NormalX=0 NormalY=0 NormalZ=1 AngleXU=0 Radius=21
  constraints (17):
    c: Equal(g3,g0)
    c: Equal(g3,g1)
    c: Equal(g3,g2)
    c: Diameter(g3) = 3.3
    c: DistanceX(g1) = 40
    c: DistanceY(g1) = -167
    c: DistanceY(g1,g0) = 0
    c: DistanceX(g2,g1) = 0
    c: DistanceY(g1,g2) = 34
    c: DistanceY(g2,g3) = 0
    c: DistanceX(g2,g3) = 34
    c: DistanceX(g0,g3) = 0
    c: Coincident(g5,g4)
    c: DistanceX(g4) = 57
    c: DistanceY(g4) = -150
    c: Diameter(g5) = 42
    c: Diameter(g4) = 55
FEATURE [Part::Feature] Part__Feature105  label="Printed Circuit Board"
  shape: bbox 25.4 x 17.78 x 1.6 mm, 42 faces (baked)
FEATURE [Part::Feature] Part__Feature106  label="EAHC2835WD6"
  shape: bbox 3.513 x 2.813 x 0.7485 mm, 108 faces, 4 solids (baked)
FEATURE [Part::Feature] Part__Feature107  label="AS7341 v2"
  Placement = pos=(0,-0.339822,1.6) rot=(0,0,1;0rad)
  shape: bbox 2 x 3.1 x 1.1 mm, 267 faces, 26 solids (baked)
FEATURE [Part::Feature] Part__Feature108  label="CAPC-0805-T0.95-BN v1"
  Placement = pos=(-5.01759,-3.15294,1.6) rot=(0,0,1;0rad)
  shape: bbox 2.1 x 1.35 x 0.95 mm, 42 faces (baked)
FEATURE [Part::Feature] Part__Feature109  label="CAPC-0805-T0.95-BN v002"
  Placement = pos=(-5.48627,2.66154,1.6) rot=(0,0,-1;1.5708rad)
  shape: bbox 1.35 x 2.1 x 0.95 mm, 42 faces (baked)
FEATURE [Part::Feature] Part__Feature110  label="CAPC-0805-T0.95-BN v003"
  Placement = pos=(-3.43627,2.66154,1.6) rot=(0,0,-1;1.5708rad)
  shape: bbox 1.35 x 2.1 x 0.95 mm, 42 faces (baked)
FEATURE [Part::Feature] Part__Feature111  label="CAPC-0603-T0.9-BN v1"
  Placement = pos=(-1.69987,-3.28475,1.6) rot=(0,0,1;0rad)
  shape: bbox 1.7 x 0.9 x 0.9 mm, 42 faces (baked)
FEATURE [Part::Feature] Part__Feature112  label="BODY_MF06A"
  Placement = pos=(0,0,0.762) rot=(0.57735,-0.57735,-0.57735;2.0944rad)
  shape: bbox 1.601 x 2.921 x 1.016 mm, 42 faces (baked)
FEATURE [Part::Feature] Part__Feature113  label="LEAD_MF06A"
  Placement = pos=(-0.9652,-0.9525,0.1016) rot=(0.57735,-0.57735,-0.57735;2.0944rad)
  shape: bbox 0.6223 x 0.3749 x 0.8636 mm, 14 faces (baked)
FEATURE [Part::Feature] Part__Feature114  label="LEAD_MF06A001"
  Placement = pos=(-0.9652,0,0.1016) rot=(0.57735,-0.57735,-0.57735;2.0944rad)
  shape: bbox 0.6223 x 0.3749 x 0.8636 mm, 14 faces (baked)
FEATURE [Part::Feature] Part__Feature115  label="LEAD_MF06A002"
  Placement = pos=(-0.9652,0.9525,0.1016) rot=(0.57735,-0.57735,-0.57735;2.0944rad)
  shape: bbox 0.6223 x 0.3749 x 0.8636 mm, 14 faces (baked)
FEATURE [Part::Feature] Part__Feature116  label="LEAD_MF06A003"
  Placement = pos=(0.9652,-0.9525,0.1016) rot=(0.57735,0.57735,0.57735;2.0944rad)
  shape: bbox 0.6223 x 0.3749 x 0.8636 mm, 14 faces (baked)
FEATURE [Part::Feature] Part__Feature117  label="LEAD_MF06A004"
  Placement = pos=(0.9652,0,0.1016) rot=(0.57735,0.57735,0.57735;2.0944rad)
  shape: bbox 0.6223 x 0.3749 x 0.8636 mm, 14 faces (baked)
FEATURE [Part::Feature] Part__Feature118  label="LEAD_MF06A005"
  Placement = pos=(0.9652,0.9525,0.1016) rot=(0.57735,0.57735,0.57735;2.0944rad)
  shape: bbox 0.6223 x 0.3749 x 0.8636 mm, 14 faces (baked)
FEATURE [Part::Feature] Part__Feature119  label="SOT363 v2"
  Placement = pos=(4.97054,-0.645171,1.675) rot=(0,0,1;3.14159rad)
  shape: bbox 2.1 x 2 x 1.1 mm, 94 faces, 7 solids (baked)
FEATURE [Part::Feature] Part__Feature120  label="LED 0603 single color v1"
  Placement = pos=(-9.18406,3.72778,1.60762) rot=(0,0,1;1.5708rad)
  shape: bbox 1.961 x 0.7932 x 0.7145 mm, 63 faces, 5 solids (baked)
FEATURE [Part::Feature] Part__Feature121  label="RESC-0603 v1"
  Placement = pos=(4.83432,-3.67461,1.6) rot=(0,0,1;0rad)
  shape: bbox 1.7 x 0.9 x 0.55 mm, 52 faces, 3 solids (baked)
FEATURE [Part::Feature] Part__Feature122  label="RESC-0603 v002"
  Placement = pos=(-7.14949,3.61248,1.6) rot=(0,0,-1;1.5708rad)
  shape: bbox 0.9 x 1.7 x 0.55 mm, 52 faces, 3 solids (baked)
FEATURE [Part::Feature] Part__Feature123  label="YC164_RESPACK v1"
  Placement = pos=(2.99591,1.52916,1.6) rot=(0,0,1;0rad)
  shape: bbox 3.2 x 1.6 x 0.61 mm, 172 faces (baked)
FEATURE [Part::Feature] Part__Feature124  label="qwicc v2"
  Placement = pos=(-10.8364,0.0607456,1.65) rot=(0,0,-1;1.5708rad)
  shape: bbox 4.95 x 6 x 2.96 mm, 229 faces, 7 solids (baked)
FEATURE [Part::Feature] Part__Feature125  label="qwicc v003"
  Placement = pos=(10.8256,0.00556102,1.65) rot=(0,0,1;1.5708rad)
  shape: bbox 4.95 x 6 x 2.96 mm, 229 faces, 7 solids (baked)
FEATURE [App::Part] sot_23_6_v2  label="sot-23-6 v2"
  Group = -> [Part__Feature112,Part__Feature113,Part__Feature114,Part__Feature115,Part__Feature116,Part__Feature117,Part__Feature118]
  Origin = -> Origin008
  Placement = pos=(-4.47945,-0.603742,1.69152) rot=(0,0,1;0rad)
FEATURE [App::Part] Adafruit_AS7341_STEMMA_QT_v2  label="ltr390"
  Group = -> [Part__Feature105,Part__Feature106,Part__Feature107,Part__Feature108,Part__Feature109,Part__Feature110,Part__Feature111,sot_23_6_v2,Part__Feature119,Part__Feature120,Part__Feature121,Part__Feature122,Part__Feature123,Part__Feature124,Part__Feature125]
  Origin = -> Origin009
  Placement = pos=(0,-98,110) rot=(0,0,1;0rad)
FEATURE [Part::Box] Box  label="guva"
  AttacherType = Attacher::AttachEngine3D
  Height = 2
  Length = 19
  Placement = pos=(-9.5,-88,0) rot=(0,0,1;0rad)
  Width = 10
FEATURE [Part::Cylinder] Cylinder098
  Angle = 360
  AttacherType = Attacher::AttachEngine3D
  FirstAngle = 0
  Height = 10
  Placement = pos=(6.5,-83,0) rot=(0,0,1;0rad)
  Radius = 1.13
  SecondAngle = 0
FEATURE [Part::Cut] Cut018  label="guva001"
  Base = -> Box
  Placement = pos=(0,0,110) rot=(0,0,1;0rad)
  Tool = -> Cylinder098
FEATURE [Sketcher::SketchObject] Sketch004
  FullyConstrained = true
  sketch-geometry (11):
    g0: Circle CenterX=6.5 CenterY=-83 CenterZ=0 NormalX=0 NormalY=0 NormalZ=1 AngleXU=0 Radius=1.125
    g1: Circle CenterX=10.15 CenterY=-91.65 CenterZ=0 NormalX=0 NormalY=0 NormalZ=1 AngleXU=0 Radius=1.125
    g2: Circle CenterX=10.15 CenterY=-104.35 CenterZ=0 NormalX=0 NormalY=0 NormalZ=1 AngleXU=0 Radius=1.125
    g3: Circle CenterX=-10.15 CenterY=-104.35 CenterZ=0 NormalX=0 NormalY=0 NormalZ=1 AngleXU=0 Radius=1.125
    g4: Circle CenterX=-10.15 CenterY=-91.65 CenterZ=0 NormalX=0 NormalY=0 NormalZ=1 AngleXU=0 Radius=1.125
    g5: ArcOfCircle CenterX=-9.5 CenterY=-78 CenterZ=0 NormalX=0 NormalY=0 NormalZ=1 AngleXU=0 Radius=9.5 StartAngle=4.71239 EndAngle=6.28319
    g6: LineSegment StartX=-9.5 StartY=-87.5 StartZ=0 EndX=-15.15 EndY=-87.5 EndZ=0
    g7: LineSegment StartX=-15.15 StartY=-87.5 StartZ=0 EndX=-15.15 EndY=-109.35 EndZ=0
    g8: LineSegment StartX=-15.15 StartY=-109.35 StartZ=0 EndX=15.15 EndY=-109.35 EndZ=0
    g9: LineSegment StartX=15.15 StartY=-109.35 StartZ=0 EndX=15.15 EndY=-78 EndZ=0
    g10: LineSegment StartX=15.15 StartY=-78 StartZ=0 EndX=0 EndY=-78 EndZ=0
  constraints (34):
    c: DistanceX(g4,g3) = 0
    c: DistanceX(g2,g1) = 0
    c: Equal(g2,g3)
    c: Equal(g2,g4)
    c: Equal(g2,g1)
    c: Equal(g2,g0)
    c: Diameter(g2) = 2.25
    c: DistanceX(g2) = 10.15
    c: DistanceY(g2) = -104.35
    c: DistanceY(g2,g1) = 12.7
    c: DistanceY(g3,g2) = 0
    c: DistanceX(g3,g2) = 20.3
    c: DistanceY(g4,g1) = 0
    c: DistanceY(g0) = -83
    c: DistanceX(g0) = 6.5
    c: PointOnObject(g5,g-2)
    c: Coincident(g6,g5)
    c: Horizontal(g6)
    c: Coincident(g7,g6)
    c: Vertical(g7)
    c: Coincident(g8,g7)
    c: Horizontal(g8)
    c: Coincident(g9,g8)
    c: Vertical(g9)
    c: Coincident(g10,g9)
    c: Coincident(g10,g5)
    c: Horizontal(g10)
    c: DistanceY(g5) = -78
    c: DistanceY(g5,g5) = 0
    c: DistanceX(g5,g5) = 9.5
    c: DistanceX(g5,g5) = 0
    c: DistanceX(g1,g9) = 5
    c: DistanceX(g7,g3) = 5
    c: DistanceY(g7,g3) = 5
FEATURE [Part::Extrusion] Extrude002  label="as7265Holder"
  Base = -> Sketch002
  Dir = (0,0,1)
  DirMode = 2
  FaceMakerClass = Part::FaceMakerBullseye
  LengthFwd = 10
  LengthRev = 0
  Placement = pos=(0,0,100) rot=(0,0,1;0rad)
  Solid = true
  Symmetric = false
FEATURE [Part::Extrusion] Extrude003  label="cameraHolder"
  Base = -> Sketch003
  Dir = (0,0,1)
  DirMode = 2
  FaceMakerClass = Part::FaceMakerBullseye
  LengthFwd = 8.25
  LengthRev = 0
  Placement = pos=(0,0,80) rot=(0,0,1;0rad)
  Solid = true
  Symmetric = false
FEATURE [Part::Extrusion] Extrude004  label="uvHolder"
  Base = -> Sketch004
  Dir = (0,0,1)
  DirMode = 2
  FaceMakerClass = Part::FaceMakerBullseye
  LengthFwd = 10
  LengthRev = 0
  Placement = pos=(0,0,100) rot=(0,0,1;0rad)
  Solid = true
  Symmetric = false
FEATURE [Part::Feature] Part__Feature040  label="CeramicBody (1)"
  shape: bbox 1.8 x 1.23 x 1.23 mm, 10 faces (baked)
FEATURE [Part::Feature] Part__Feature104  label="ips7100"
  Placement = pos=(-24,0,222) rot=(0.999993,-0.003655,0;3.14159rad)
  shape: bbox 48.14 x 14.05 x 44.14 mm, 1935 faces (baked)
FEATURE [Part::Compound] Compound  label="ips7100s"
  Links = -> [Part__Feature104]
  Placement = pos=(24,-180,25) rot=(0,0,1;0.006109rad)
FEATURE [Part::Feature] Part__Feature126  label="scd30"
  Placement = pos=(-1e-15,-110,40) rot=(1,0,0;3.14159rad)
  shape: bbox 35.11 x 7.027 x 23.02 mm, 2292 faces, 25 solids (baked)
FEATURE [Part::Feature] Part__Feature127  label="Board"
  shape: bbox 25.4 x 25.4 x 1.57 mm, 211 faces (baked)
FEATURE [Part::Feature] Part__Feature128  label="QFN24_4MM"
  Placement = pos=(12.1412,14.4526,1.57) rot=(0,0,1;3.92699rad)
  shape: bbox 5.657 x 5.657 x 0.9 mm, 172 faces (baked)
FEATURE [Part::Feature] Part__Feature129  label="Part 5"
  shape: bbox 0.48 x 0.6603 x 0.6 mm, 14 faces (baked)
FEATURE [Part::Feature] Part__Feature130  label="Part 6"
  shape: bbox 0.48 x 0.6603 x 0.6 mm, 14 faces (baked)
FEATURE [Part::Feature] Part__Feature131  label="Part 4"
  shape: bbox 0.48 x 0.6603 x 0.6 mm, 14 faces (baked)
FEATURE [Part::Feature] Part__Feature132  label="Part 3"
  shape: bbox 0.48 x 0.6603 x 0.6 mm, 14 faces (baked)
FEATURE [Part::Feature] Part__Feature133  label="Part 010"
  shape: bbox 0.48 x 0.6603 x 0.6 mm, 14 faces (baked)
FEATURE [Part::Feature] Part__Feature134  label="Part 011"
  shape: bbox 3 x 1.4 x 1 mm, 10 faces (baked)
FEATURE [Part::Feature] Part__Feature135  label="Pin1"
  shape: bbox 0.6224 x 1.252 x 1.252 mm, 37 faces (baked)
FEATURE [Part::Feature] Part__Feature136  label="Pin2"
  shape: bbox 0.6224 x 1.252 x 1.252 mm, 37 faces (baked)
FEATURE [Part::Feature] Part__Feature137  label="CeramicBody"
  shape: bbox 1.8 x 1.23 x 1.23 mm, 10 faces (baked)
FEATURE [Part::Feature] Part__Feature138  label="0603-NO (1)"
  Placement = pos=(23.241,6.223,1.57) rot=(0,0,1;0rad)
  shape: bbox 1.7 x 0.9 x 0.55 mm, 52 faces, 3 solids (baked)
FEATURE [Part::Feature] Part__Feature139  label="0603-NO (2)"
  Placement = pos=(13.3858,8.4328,1.57) rot=(0,0,1;0rad)
  shape: bbox 1.7 x 0.9 x 0.55 mm, 52 faces, 3 solids (baked)
FEATURE [Part::Feature] Part__Feature140  label="0603-NO (3)"
  Placement = pos=(1.905,18.923,1.57) rot=(0,0,1;3.14159rad)
  shape: bbox 1.7 x 0.9 x 0.55 mm, 52 faces, 3 solids (baked)
FEATURE [Part::Feature] Part__Feature141  label="Pin1 (1)"
  shape: bbox 0.6224 x 1.252 x 1.252 mm, 37 faces (baked)
FEATURE [Part::Feature] Part__Feature142  label="Pin2 (1)"
  shape: bbox 0.6224 x 1.252 x 1.252 mm, 37 faces (baked)
FEATURE [Part::Feature] Part__Feature143  label="Pin1 (2)"
  shape: bbox 0.6224 x 1.252 x 1.252 mm, 37 faces (baked)
FEATURE [Part::Feature] Part__Feature144  label="Pin2 (2)"
  shape: bbox 0.6224 x 1.252 x 1.252 mm, 37 faces (baked)
FEATURE [Part::Feature] Part__Feature145  label="CeramicBody (2)"
  shape: bbox 1.8 x 1.23 x 1.23 mm, 10 faces (baked)
FEATURE [Part::Feature] Part__Feature146  label="CHIPLED_0603_NOOUTLINE"
  Placement = pos=(23.368,8.509,1.57) rot=(0,0,1;1.5708rad)
  shape: bbox 1.616 x 0.8 x 0.4 mm, 133 faces (baked)
FEATURE [Part::Feature] Part__Feature147  label="CHIPLED_0603_NOOUTLINE (1)"
  Placement = pos=(1.905,16.764,1.57) rot=(0,0,-1;1.5708rad)
  shape: bbox 1.616 x 0.8 x 0.4 mm, 133 faces (baked)
FEATURE [Part::Feature] Part__Feature148  label="JST_SH4"
  Placement = pos=(22.86,12.7,1.57) rot=(0,0,1;1.5708rad)
  shape: bbox 4.95 x 6 x 2.96 mm, 229 faces, 7 solids (baked)
FEATURE [Part::Feature] Part__Feature149  label="JST_SH4 (1)"
  Placement = pos=(2.54,12.7,1.57) rot=(0,0,-1;1.5708rad)
  shape: bbox 4.95 x 6 x 2.96 mm, 229 faces, 7 solids (baked)
FEATURE [Part::Feature] Part__Feature150  label="NEO3535_REVERSE"
  Placement = pos=(12.7,23.114,0) rot=(0,1,0;3.14159rad)
  shape: bbox 5.88 x 2.8 x 1.78 mm, 41 faces, 5 solids (baked)
FEATURE [Part::Feature] Part__Feature151  label="RESPACK_4X0603"
  Placement = pos=(22.86,18.415,1.57) rot=(0,0,1;3.14159rad)
  shape: bbox 3.2 x 1.6 x 0.61 mm, 172 faces (baked)
FEATURE [Part::Feature] Part__Feature152  label="SOT363"
  Placement = pos=(17.399,12.192,1.57) rot=(0,0,-1;1.5708rad)
  shape: bbox 2.208 x 2.208 x 1.121 mm, 178 faces, 4 solids (baked)
FEATURE [App::Part] _603_NO  label="0603-NO"
  Group = -> [Part__Feature135,Part__Feature136,Part__Feature137]
  Origin = -> Origin012
  Placement = pos=(16.51,8.382,1.57) rot=(0,0,1;0rad)
FEATURE [App::Part] _6700497  label="36700497"
  Group = -> [Part__Feature129,Part__Feature130,Part__Feature131,Part__Feature132,Part__Feature133,Part__Feature134]
  Origin = -> Origin010
  Placement = pos=(0,0,0) rot=(0,0,1;3.14159rad)
FEATURE [App::Part] SOT23_5  label="SOT23-5"
  Group = -> [_6700497]
  Origin = -> Origin011
  Placement = pos=(2.54,6.985,1.57) rot=(0,0,1;3.14159rad)
FEATURE [App::Part] _805_NO  label="0805-NO"
  Group = -> [Part__Feature141,Part__Feature142,Part__Feature040]
  Origin = -> Origin013
  Placement = pos=(7.874,13.589,1.57) rot=(0,0,1;1.5708rad)
FEATURE [App::Part] _805_NO__1_  label="0805-NO (1)"
  Group = -> [Part__Feature143,Part__Feature144,Part__Feature145]
  Origin = -> Origin014
  Placement = pos=(12.827,6.223,1.57) rot=(0,0,1;3.14159rad)
FEATURE [App::Part] Packages
  Group = -> [Part__Feature128,SOT23_5,_603_NO,Part__Feature138,Part__Feature139,Part__Feature140,_805_NO,_805_NO__1_,Part__Feature146,Part__Feature147,Part__Feature148,Part__Feature149,Part__Feature150,Part__Feature151,Part__Feature152]
  Origin = -> Origin015
FEATURE [App::Part] Adafruit_I2C_QT_Rotary_Encoder_v2  label="gps"
  Group = -> [Part__Feature127,Packages]
  Origin = -> Origin016
  Placement = pos=(-12.7,-163,95) rot=(0,0,1;0rad)
FEATURE [Sketcher::SketchObject] Sketch005  label="top007"
  FullyConstrained = true
  sketch-geometry (15):
    g0: Circle CenterX=0 CenterY=-150 CenterZ=0 NormalX=0 NormalY=0 NormalZ=1 AngleXU=0 Radius=85
    g1: Circle CenterX=-57 CenterY=-115 CenterZ=0 NormalX=0 NormalY=0 NormalZ=1 AngleXU=0 Radius=2.13
    g2: Circle CenterX=-22 CenterY=-150 CenterZ=0 NormalX=0 NormalY=0 NormalZ=1 AngleXU=0 Radius=4
    g3: Circle CenterX=-57 CenterY=-185 CenterZ=0 NormalX=0 NormalY=0 NormalZ=1 AngleXU=0 Radius=2.13
    g4: Circle CenterX=0 CenterY=-172 CenterZ=0 NormalX=0 NormalY=0 NormalZ=1 AngleXU=0 Radius=4
    g5: Circle CenterX=-35 CenterY=-207 CenterZ=0 NormalX=0 NormalY=0 NormalZ=1 AngleXU=0 Radius=2.13
    g6: Circle CenterX=35 CenterY=-207 CenterZ=0 NormalX=0 NormalY=0 NormalZ=1 AngleXU=0 Radius=2.13
    g7: Circle CenterX=57 CenterY=-185 CenterZ=0 NormalX=0 NormalY=0 NormalZ=1 AngleXU=0 Radius=2.13
    g8: Circle CenterX=22 CenterY=-150 CenterZ=0 NormalX=0 NormalY=0 NormalZ=1 AngleXU=0 Radius=4
    g9: Circle CenterX=57 CenterY=-115 CenterZ=0 NormalX=0 NormalY=0 NormalZ=1 AngleXU=0 Radius=2.13
    g10: Circle CenterX=0 CenterY=-207 CenterZ=0 NormalX=0 NormalY=0 NormalZ=1 AngleXU=0 Radius=4.5
    g11: Circle CenterX=57 CenterY=-150 CenterZ=0 NormalX=0 NormalY=0 NormalZ=1 AngleXU=0 Radius=21
    g12: Circle CenterX=-35 CenterY=-93 CenterZ=0 NormalX=0 NormalY=0 NormalZ=1 AngleXU=0 Radius=2.13
    g13: Circle CenterX=35 CenterY=-93 CenterZ=0 NormalX=0 NormalY=0 NormalZ=1 AngleXU=0 Radius=2.13
    g14: Circle CenterX=0 CenterY=-128 CenterZ=0 NormalX=0 NormalY=0 NormalZ=1 AngleXU=0 Radius=4
  constraints (45):
    c: Radius(g0) = 85
    c: DistanceY(g0) = -150
    c: DistanceY(g8,g0) = 0
    c: DistanceY(g0,g2) = 0
    c: Radius(g11) = 21
    c: DistanceX(g10,g0) = 0
    c: DistanceX(g0,g11) = 57
    c: DistanceY(g11,g0) = 0
    c: DistanceX(g0,g8) = 22
    c: DistanceX(g2,g0) = 22
    c: DistanceX(g5,g10) = 35
    c: DistanceX(g10,g6) = 35
    c: DistanceX(g7,g11) = 0
    c: DistanceX(g11,g9) = 0
    c: DistanceX(g1,g0) = 57
    c: DistanceY(g3,g0) = 35
    c: DistanceY(g0,g1) = 35
    c: DistanceY(g10,g4) = 35
    c: DistanceY(g6,g10) = 0
    c: DistanceY(g10,g5) = 0
    c: DistanceY(g7,g11) = 35
    c: DistanceY(g11,g9) = 35
    c: DistanceX(g3,g1) = 0
    c: DistanceY(g10,g0) = 57
    c: Diameter(g10) = 9
    c: DistanceX(g12) = -35
    c: DistanceX(g13) = 35
    c: DistanceY(g0,g14) = 22
    c: DistanceX(g0) = 0
    c: DistanceX(g4) = 0
    c: DistanceX(g14) = 0
    c: DistanceY(g0,g13) = 57
    c: DistanceY(g0,g12) = 57
    c: Equal(g5,g6)
    c: Equal(g5,g7)
    c: Equal(g5,g9)
    c: Equal(g5,g13)
    c: Equal(g5,g12)
    c: Equal(g5,g1)
    c: Equal(g5,g3)
    c: Radius(g5) = 2.13
    c: Equal(g4,g8)
    c: Equal(g4,g14)
    c: Equal(g4,g2)
    c: Diameter(g4) = 8
FEATURE [Part::Extrusion] Extrude005  label="level1"
  Base = -> Sketch005
  Dir = (0,0,1)
  DirMode = 2
  FaceMakerClass = Part::FaceMakerBullseye
  LengthFwd = 5
  LengthRev = 0
  Placement = pos=(0,0,75) rot=(0,0,1;0rad)
  Solid = true
  Symmetric = false
FEATURE [Part::Box] Box007  label="Cube001"
  AttacherType = Attacher::AttachEngine3D
  Height = 20
  Length = 30
  Placement = pos=(-72,-155,80) rot=(0,0,1;0rad)
  Width = 10
FEATURE [Part::MultiFuse] Fusion049  label="as7265Holder001"
  Shapes = -> [Box007,Extrude002]
FEATURE [Sketcher::SketchObject] Sketch006
  FullyConstrained = true
  sketch-geometry (6):
    g0: Circle CenterX=0 CenterY=-150 CenterZ=0 NormalX=0 NormalY=0 NormalZ=1 AngleXU=0 Radius=17.5
    g1: Circle CenterX=-10.15 CenterY=-140.15 CenterZ=0 NormalX=0 NormalY=0 NormalZ=1 AngleXU=0 Radius=1.65
    g2: Circle CenterX=10.15 CenterY=-140.15 CenterZ=0 NormalX=0 NormalY=0 NormalZ=1 AngleXU=0 Radius=1.65
    g3: Circle CenterX=10.15 CenterY=-160.45 CenterZ=0 NormalX=0 NormalY=0 NormalZ=1 AngleXU=0 Radius=1.65
    g4: Circle CenterX=-10.15 CenterY=-160.45 CenterZ=0 NormalX=0 NormalY=0 NormalZ=1 AngleXU=0 Radius=1.65
    g5: Circle CenterX=0 CenterY=-150 CenterZ=0 NormalX=0 NormalY=0 NormalZ=1 AngleXU=0 Radius=11
  constraints (17):
    c: DistanceY(g0) = -150
    c: DistanceX(g0) = 0
    c: Radius(g0) = 17.5
    c: Equal(g4,g3)
    c: Equal(g4,g2)
    c: Equal(g4,g1)
    c: Diameter(g4) = 3.3
    c: DistanceX(g1,g4) = 0
    c: DistanceY(g2,g1) = 0
    c: DistanceY(g3,g4) = 0
    c: DistanceX(g2,g3) = 0
    c: DistanceY(g4,g0) = 10.45
    c: DistanceY(g0,g1) = 9.85
    c: DistanceX(g3) = 10.15
    c: DistanceX(g4) = -10.15
    c: Coincident(g5,g0)
    c: Diameter(g5) = 22
FEATURE [Part::Extrusion] Extrude006  label="gpsHolder"
  Base = -> Sketch006
  Dir = (0,0,1)
  DirMode = 2
  FaceMakerClass = Part::FaceMakerBullseye
  LengthFwd = 15
  LengthRev = 0
  Placement = pos=(0,0,80) rot=(0,0,1;0rad)
  Solid = true
  Symmetric = false
FEATURE [Part::Box] Box008  label="Cube"
  AttacherType = Attacher::AttachEngine3D
  Height = 25
  Length = 10
  Placement = pos=(-5,-109.35,75) rot=(0,0,1;0rad)
  Width = 20
FEATURE [Part::MultiFuse] Fusion050  label="uvHolder001"
  Shapes = -> [Box008,Extrude004]
FEATURE [Part::Cylinder] Cylinder099  label="refModuleHold001"
  Angle = 360
  AttacherType = Attacher::AttachEngine3D
  FirstAngle = 0
  Height = 32
  Placement = pos=(0,-207,80) rot=(0,0,1;0rad)
  Radius = 12
  SecondAngle = 0
FEATURE [Part::MultiFuse] Fusion051  label="refModule"
  Shapes = -> [Cylinder095,Cylinder094]
FEATURE [Part::Cylinder] Cylinder100  label="refModules001"
  Angle = 360
  AttacherType = Attacher::AttachEngine3D
  FirstAngle = 0
  Height = 75
  Placement = pos=(0,-207,37) rot=(0,0,1;0rad)
  Radius = 3.75
  SecondAngle = 0
FEATURE [Part::Cylinder] Cylinder101  label="refModulesCoverCut002"
  Angle = 360
  AttacherType = Attacher::AttachEngine3D
  FirstAngle = 0
  Height = 60
  Placement = pos=(0,-207,37) rot=(0,0,1;0rad)
  Radius = 4.5
  SecondAngle = 0
FEATURE [Part::MultiFuse] Fusion052  label="refModule001Cut"
  Shapes = -> [Cylinder101,Cylinder100]
FEATURE [Part::Cut] Cut019  label="refModuleHold002"
  Base = -> Cylinder099
  Tool = -> Fusion052
FEATURE [Sketcher::SketchObject] Sketch007
  FullyConstrained = true
  Placement = pos=(0,0,0) rot=(1,0,0;1.5708rad)
  sketch-geometry (1):
    g0: Circle CenterX=0 CenterY=102.5 CenterZ=0 NormalX=0 NormalY=0 NormalZ=1 AngleXU=0 Radius=2
  constraints (3):
    c: PointOnObject(g0,g-2)
    c: DistanceY(g0) = 102.5
    c: Diameter(g0) = 4
FEATURE [Part::Extrusion] Extrude007  label="m3HeatSetInsertCut"
  Base = -> Sketch007
  Dir = (0,-1,-3e-16)
  DirMode = 2
  FaceMakerClass = Part::FaceMakerBullseye
  LengthFwd = 50
  LengthRev = 0
  Placement = pos=(0,-183.25,0) rot=(0,0,1;0rad)
  Solid = true
  Symmetric = false
FEATURE [Part::Cut] Cut020  label="refSensorHoldLev1"
  Base = -> Cut019
  Tool = -> Extrude007
FEATURE [Part::MultiFuse] Fusion053  label="level1SensorHolds"
  Shapes = -> [Fusion050,Cut020,Extrude006,Fusion049,Extrude003]
FEATURE [Part::MultiFuse] Fusion054  label="level001x"
  Shapes = -> [Fusion053,Extrude005]
FEATURE [Part::Feature] Part__Feature153  label="Printed Circuit Board001"
  shape: bbox 25.4 x 17.78 x 1.6 mm, 42 faces (baked)
FEATURE [Part::Feature] Part__Feature154  label="EAHC2835WD007"
  shape: bbox 3.513 x 2.813 x 0.7485 mm, 108 faces, 4 solids (baked)
FEATURE [Part::Feature] Part__Feature155  label="AS7341 v003"
  Placement = pos=(0,-0.339822,1.6) rot=(0,0,1;0rad)
  shape: bbox 2 x 3.1 x 1.1 mm, 267 faces, 26 solids (baked)
FEATURE [Part::Feature] Part__Feature156  label="CAPC-0805-T0.95-BN v004"
  Placement = pos=(-5.01759,-3.15294,1.6) rot=(0,0,1;0rad)
  shape: bbox 2.1 x 1.35 x 0.95 mm, 42 faces (baked)
FEATURE [Part::Feature] Part__Feature157  label="CAPC-0805-T0.95-BN v005"
  Placement = pos=(-5.48627,2.66154,1.6) rot=(0,0,-1;1.5708rad)
  shape: bbox 1.35 x 2.1 x 0.95 mm, 42 faces (baked)
FEATURE [Part::Feature] Part__Feature158  label="CAPC-0805-T0.95-BN v006"
  Placement = pos=(-3.43627,2.66154,1.6) rot=(0,0,-1;1.5708rad)
  shape: bbox 1.35 x 2.1 x 0.95 mm, 42 faces (baked)
FEATURE [Part::Feature] Part__Feature159  label="CAPC-0603-T0.9-BN v002"
  Placement = pos=(-1.69987,-3.28475,1.6) rot=(0,0,1;0rad)
  shape: bbox 1.7 x 0.9 x 0.9 mm, 42 faces (baked)
FEATURE [Part::Feature] Part__Feature160  label="BODY_MF06A001"
  Placement = pos=(0,0,0.762) rot=(0.57735,-0.57735,-0.57735;2.0944rad)
  shape: bbox 1.601 x 2.921 x 1.016 mm, 42 faces (baked)
FEATURE [Part::Feature] Part__Feature161  label="LEAD_MF06A006"
  Placement = pos=(-0.9652,-0.9525,0.1016) rot=(0.57735,-0.57735,-0.57735;2.0944rad)
  shape: bbox 0.6223 x 0.3749 x 0.8636 mm, 14 faces (baked)
FEATURE [Part::Feature] Part__Feature162  label="LEAD_MF06A007"
  Placement = pos=(-0.9652,0,0.1016) rot=(0.57735,-0.57735,-0.57735;2.0944rad)
  shape: bbox 0.6223 x 0.3749 x 0.8636 mm, 14 faces (baked)
FEATURE [Part::Feature] Part__Feature163  label="LEAD_MF06A008"
  Placement = pos=(-0.9652,0.9525,0.1016) rot=(0.57735,-0.57735,-0.57735;2.0944rad)
  shape: bbox 0.6223 x 0.3749 x 0.8636 mm, 14 faces (baked)
FEATURE [Part::Feature] Part__Feature164  label="LEAD_MF06A009"
  Placement = pos=(0.9652,-0.9525,0.1016) rot=(0.57735,0.57735,0.57735;2.0944rad)
  shape: bbox 0.6223 x 0.3749 x 0.8636 mm, 14 faces (baked)
FEATURE [Part::Feature] Part__Feature165  label="LEAD_MF06A010"
  Placement = pos=(0.9652,0,0.1016) rot=(0.57735,0.57735,0.57735;2.0944rad)
  shape: bbox 0.6223 x 0.3749 x 0.8636 mm, 14 faces (baked)
FEATURE [Part::Feature] Part__Feature166  label="LEAD_MF06A011"
  Placement = pos=(0.9652,0.9525,0.1016) rot=(0.57735,0.57735,0.57735;2.0944rad)
  shape: bbox 0.6223 x 0.3749 x 0.8636 mm, 14 faces (baked)
FEATURE [Part::Feature] Part__Feature167  label="SOT363 v003"
  Placement = pos=(4.97054,-0.645171,1.675) rot=(0,0,1;3.14159rad)
  shape: bbox 2.1 x 2 x 1.1 mm, 94 faces, 7 solids (baked)
FEATURE [Part::Feature] Part__Feature168  label="LED 0603 single color v002"
  Placement = pos=(-9.18406,3.72778,1.60762) rot=(0,0,1;1.5708rad)
  shape: bbox 1.961 x 0.7932 x 0.7145 mm, 63 faces, 5 solids (baked)
FEATURE [Part::Feature] Part__Feature169  label="RESC-0603 v003"
  Placement = pos=(4.83432,-3.67461,1.6) rot=(0,0,1;0rad)
  shape: bbox 1.7 x 0.9 x 0.55 mm, 52 faces, 3 solids (baked)
FEATURE [Part::Feature] Part__Feature170  label="RESC-0603 v004"
  Placement = pos=(-7.14949,3.61248,1.6) rot=(0,0,-1;1.5708rad)
  shape: bbox 0.9 x 1.7 x 0.55 mm, 52 faces, 3 solids (baked)
FEATURE [Part::Feature] Part__Feature171  label="YC164_RESPACK v002"
  Placement = pos=(2.99591,1.52916,1.6) rot=(0,0,1;0rad)
  shape: bbox 3.2 x 1.6 x 0.61 mm, 172 faces (baked)
FEATURE [Part::Feature] Part__Feature172  label="qwicc v004"
  Placement = pos=(-10.8364,0.0607456,1.65) rot=(0,0,-1;1.5708rad)
  shape: bbox 4.95 x 6 x 2.96 mm, 229 faces, 7 solids (baked)
FEATURE [Part::Feature] Part__Feature173  label="qwicc v005"
  Placement = pos=(10.8256,0.00556102,1.65) rot=(0,0,1;1.5708rad)
  shape: bbox 4.95 x 6 x 2.96 mm, 229 faces, 7 solids (baked)
FEATURE [App::Part] sot_23_6_v003  label="sot-23-6 v003"
  Group = -> [Part__Feature160,Part__Feature161,Part__Feature162,Part__Feature163,Part__Feature164,Part__Feature165,Part__Feature166]
  Origin = -> Origin017
  Placement = pos=(-4.47945,-0.603742,1.69152) rot=(0,0,1;0rad)
FEATURE [App::Part] Adafruit_AS7341_STEMMA_QT_v003  label="bme280"
  Group = -> [Part__Feature153,Part__Feature154,Part__Feature155,Part__Feature156,Part__Feature157,Part__Feature158,Part__Feature159,sot_23_6_v003,Part__Feature167,Part__Feature168,Part__Feature169,Part__Feature170,Part__Feature171,Part__Feature172,Part__Feature173]
  Origin = -> Origin018
  Placement = pos=(30,-149.75,45) rot=(0.57735,-0.57735,0.57735;4.18879rad)
FEATURE [Part::Cone] Cone
  Angle = 360
  AttacherType = Attacher::AttachEngine3D
  Height = 1.5
  Placement = pos=(0,0,25.5) rot=(0,0,1;0rad)
  Radius1 = 4
  Radius2 = 3.5
FEATURE [Part::Cylinder] Cylinder020
  Angle = 360
  AttacherType = Attacher::AttachEngine3D
  FirstAngle = 0
  Height = 22
  Placement = pos=(0,0,5) rot=(0,0,1;0rad)
  Radius = 3.2
  SecondAngle = 0
FEATURE [Part::Cylinder] Cylinder021
  Angle = 360
  AttacherType = Attacher::AttachEngine3D
  FirstAngle = 0
  Height = 2
  Placement = pos=(0,0,5) rot=(0,0,1;0rad)
  Radius = 3.55
  SecondAngle = 0
FEATURE [Part::Cylinder] Cylinder022
  Angle = 360
  AttacherType = Attacher::AttachEngine3D
  FirstAngle = 0
  Height = 1
  Placement = pos=(0,0,11) rot=(0,0,1;0rad)
  Radius = 3.55
  SecondAngle = 0
FEATURE [Part::Cylinder] Cylinder023
  Angle = 360
  AttacherType = Attacher::AttachEngine3D
  FirstAngle = 0
  Height = 8
  Placement = pos=(0,0,12) rot=(0,0,1;0rad)
  Radius = 3.25
  SecondAngle = 0
FEATURE [Part::Cylinder] Cylinder024
  Angle = 360
  AttacherType = Attacher::AttachEngine3D
  FirstAngle = 0
  Height = 5.5
  Placement = pos=(0,0,20) rot=(0,0,1;0rad)
  Radius = 4
  SecondAngle = 0
FEATURE [Part::Cylinder] Cylinder025
  Angle = 360
  AttacherType = Attacher::AttachEngine3D
  FirstAngle = 0
  Height = 2
  Placement = pos=(0,0,3) rot=(0,0,1;0rad)
  Radius = 1
  SecondAngle = 0
FEATURE [Part::MultiFuse] Fusion002
  Shapes = -> [Cone,Cylinder020,Cylinder021,Cylinder022,Cylinder023,Cylinder024]
FEATURE [Part::MultiFuse] Fusion055  label="mic"
  Placement = pos=(0,-212,-239.2) rot=(0,1,0;3.14159rad)
  Shapes = -> [Cylinder025,Fusion002]
FEATURE [Part::Feature] Part__Feature174  label="Printed Circuit Board002"
  shape: bbox 25.4 x 17.78 x 1.6 mm, 42 faces (baked)
FEATURE [Part::Feature] Part__Feature175  label="EAHC2835WD008"
  shape: bbox 3.513 x 2.813 x 0.7485 mm, 108 faces, 4 solids (baked)
FEATURE [Part::Feature] Part__Feature176  label="AS7341 v004"
  Placement = pos=(0,-0.339822,1.6) rot=(0,0,1;0rad)
  shape: bbox 2 x 3.1 x 1.1 mm, 267 faces, 26 solids (baked)
FEATURE [Part::Feature] Part__Feature177  label="CAPC-0805-T0.95-BN v007"
  Placement = pos=(-5.01759,-3.15294,1.6) rot=(0,0,1;0rad)
  shape: bbox 2.1 x 1.35 x 0.95 mm, 42 faces (baked)
FEATURE [Part::Feature] Part__Feature178  label="CAPC-0805-T0.95-BN v008"
  Placement = pos=(-5.48627,2.66154,1.6) rot=(0,0,-1;1.5708rad)
  shape: bbox 1.35 x 2.1 x 0.95 mm, 42 faces (baked)
FEATURE [Part::Feature] Part__Feature179  label="CAPC-0805-T0.95-BN v009"
  Placement = pos=(-3.43627,2.66154,1.6) rot=(0,0,-1;1.5708rad)
  shape: bbox 1.35 x 2.1 x 0.95 mm, 42 faces (baked)
FEATURE [Part::Feature] Part__Feature180  label="CAPC-0603-T0.9-BN v003"
  Placement = pos=(-1.69987,-3.28475,1.6) rot=(0,0,1;0rad)
  shape: bbox 1.7 x 0.9 x 0.9 mm, 42 faces (baked)
FEATURE [Part::Feature] Part__Feature181  label="BODY_MF06A002"
  Placement = pos=(0,0,0.762) rot=(0.57735,-0.57735,-0.57735;2.0944rad)
  shape: bbox 1.601 x 2.921 x 1.016 mm, 42 faces (baked)
FEATURE [Part::Feature] Part__Feature182  label="LEAD_MF06A012"
  Placement = pos=(-0.9652,-0.9525,0.1016) rot=(0.57735,-0.57735,-0.57735;2.0944rad)
  shape: bbox 0.6223 x 0.3749 x 0.8636 mm, 14 faces (baked)
FEATURE [Part::Feature] Part__Feature183  label="LEAD_MF06A013"
  Placement = pos=(-0.9652,0,0.1016) rot=(0.57735,-0.57735,-0.57735;2.0944rad)
  shape: bbox 0.6223 x 0.3749 x 0.8636 mm, 14 faces (baked)
FEATURE [Part::Feature] Part__Feature184  label="LEAD_MF06A014"
  Placement = pos=(-0.9652,0.9525,0.1016) rot=(0.57735,-0.57735,-0.57735;2.0944rad)
  shape: bbox 0.6223 x 0.3749 x 0.8636 mm, 14 faces (baked)
FEATURE [Part::Feature] Part__Feature185  label="LEAD_MF06A015"
  Placement = pos=(0.9652,-0.9525,0.1016) rot=(0.57735,0.57735,0.57735;2.0944rad)
  shape: bbox 0.6223 x 0.3749 x 0.8636 mm, 14 faces (baked)
FEATURE [Part::Feature] Part__Feature186  label="LEAD_MF06A016"
  Placement = pos=(0.9652,0,0.1016) rot=(0.57735,0.57735,0.57735;2.0944rad)
  shape: bbox 0.6223 x 0.3749 x 0.8636 mm, 14 faces (baked)
FEATURE [Part::Feature] Part__Feature187  label="LEAD_MF06A017"
  Placement = pos=(0.9652,0.9525,0.1016) rot=(0.57735,0.57735,0.57735;2.0944rad)
  shape: bbox 0.6223 x 0.3749 x 0.8636 mm, 14 faces (baked)
FEATURE [Part::Feature] Part__Feature188  label="SOT363 v004"
  Placement = pos=(4.97054,-0.645171,1.675) rot=(0,0,1;3.14159rad)
  shape: bbox 2.1 x 2 x 1.1 mm, 94 faces, 7 solids (baked)
FEATURE [Part::Feature] Part__Feature189  label="LED 0603 single color v003"
  Placement = pos=(-9.18406,3.72778,1.60762) rot=(0,0,1;1.5708rad)
  shape: bbox 1.961 x 0.7932 x 0.7145 mm, 63 faces, 5 solids (baked)
FEATURE [Part::Feature] Part__Feature190  label="RESC-0603 v005"
  Placement = pos=(4.83432,-3.67461,1.6) rot=(0,0,1;0rad)
  shape: bbox 1.7 x 0.9 x 0.55 mm, 52 faces, 3 solids (baked)
FEATURE [Part::Feature] Part__Feature191  label="RESC-0603 v006"
  Placement = pos=(-7.14949,3.61248,1.6) rot=(0,0,-1;1.5708rad)
  shape: bbox 0.9 x 1.7 x 0.55 mm, 52 faces, 3 solids (baked)
FEATURE [Part::Feature] Part__Feature192  label="YC164_RESPACK v003"
  Placement = pos=(2.99591,1.52916,1.6) rot=(0,0,1;0rad)
  shape: bbox 3.2 x 1.6 x 0.61 mm, 172 faces (baked)
FEATURE [Part::Feature] Part__Feature193  label="qwicc v006"
  Placement = pos=(-10.8364,0.0607456,1.65) rot=(0,0,-1;1.5708rad)
  shape: bbox 4.95 x 6 x 2.96 mm, 229 faces, 7 solids (baked)
FEATURE [Part::Feature] Part__Feature194  label="qwicc v007"
  Placement = pos=(10.8256,0.00556102,1.65) rot=(0,0,1;1.5708rad)
  shape: bbox 4.95 x 6 x 2.96 mm, 229 faces, 7 solids (baked)
FEATURE [App::Part] sot_23_6_v004  label="sot-23-6 v004"
  Group = -> [Part__Feature181,Part__Feature182,Part__Feature183,Part__Feature184,Part__Feature185,Part__Feature186,Part__Feature187]
  Origin = -> Origin019
  Placement = pos=(-4.47945,-0.603742,1.69152) rot=(0,0,1;0rad)
FEATURE [App::Part] Adafruit_AS7341_STEMMA_QT_v004  label="bme281"
  Group = -> [Part__Feature174,Part__Feature175,Part__Feature176,Part__Feature177,Part__Feature178,Part__Feature179,Part__Feature180,sot_23_6_v004,Part__Feature188,Part__Feature189,Part__Feature190,Part__Feature191,Part__Feature192,Part__Feature193,Part__Feature194]
  Origin = -> Origin020
  Placement = pos=(-30,-149.75,45) rot=(-0.57735,-0.57735,0.57735;2.0944rad)
FEATURE [Sketcher::SketchObject] Sketch008  label="top008"
  FullyConstrained = true
  sketch-geometry (15):
    g0: Circle CenterX=0 CenterY=-150 CenterZ=0 NormalX=0 NormalY=0 NormalZ=1 AngleXU=0 Radius=85
    g1: Circle CenterX=-57 CenterY=-115 CenterZ=0 NormalX=0 NormalY=0 NormalZ=1 AngleXU=0 Radius=2.125
    g2: Circle CenterX=-22 CenterY=-150 CenterZ=0 NormalX=0 NormalY=0 NormalZ=1 AngleXU=0 Radius=4
    g3: Circle CenterX=-57 CenterY=-185 CenterZ=0 NormalX=0 NormalY=0 NormalZ=1 AngleXU=0 Radius=2.125
    g4: Circle CenterX=0 CenterY=-172 CenterZ=0 NormalX=0 NormalY=0 NormalZ=1 AngleXU=0 Radius=4
    g5: Circle CenterX=-35 CenterY=-207 CenterZ=0 NormalX=0 NormalY=0 NormalZ=1 AngleXU=0 Radius=2.125
    g6: Circle CenterX=35 CenterY=-207 CenterZ=0 NormalX=0 NormalY=0 NormalZ=1 AngleXU=0 Radius=2.125
    g7: Circle CenterX=57 CenterY=-185 CenterZ=0 NormalX=0 NormalY=0 NormalZ=1 AngleXU=0 Radius=2.125
    g8: Circle CenterX=22 CenterY=-150 CenterZ=0 NormalX=0 NormalY=0 NormalZ=1 AngleXU=0 Radius=4
    g9: Circle CenterX=57 CenterY=-115 CenterZ=0 NormalX=0 NormalY=0 NormalZ=1 AngleXU=0 Radius=2.125
    g10: Circle CenterX=0 CenterY=-207 CenterZ=0 NormalX=0 NormalY=0 NormalZ=1 AngleXU=0 Radius=4.5
    g11: Circle CenterX=57 CenterY=-150 CenterZ=0 NormalX=0 NormalY=0 NormalZ=1 AngleXU=0 Radius=21
    g12: Circle CenterX=-35 CenterY=-93 CenterZ=0 NormalX=0 NormalY=0 NormalZ=1 AngleXU=0 Radius=2.125
    g13: Circle CenterX=35 CenterY=-93 CenterZ=0 NormalX=0 NormalY=0 NormalZ=1 AngleXU=0 Radius=2.125
    g14: Circle CenterX=0 CenterY=-128 CenterZ=0 NormalX=0 NormalY=0 NormalZ=1 AngleXU=0 Radius=4
  constraints (45):
    c: PointOnObject(g0,g-2)
    c: Radius(g0) = 85
    c: DistanceY(g0) = -150
    c: PointOnObject(g4,g-2)
    c: PointOnObject(g14,g-2)
    c: DistanceY(g8,g0) = 0
    c: DistanceY(g0,g2) = 0
    c: Radius(g11) = 21
    c: DistanceX(g10,g0) = 0
    c: DistanceX(g0,g11) = 57
    c: DistanceY(g11,g0) = 0
    c: DistanceX(g0,g8) = 22
    c: DistanceX(g2,g0) = 22
    c: DistanceX(g5,g10) = 35
    c: DistanceX(g10,g6) = 35
    c: DistanceX(g7,g11) = 0
    c: DistanceX(g11,g9) = 0
    c: DistanceX(g1,g0) = 57
    c: DistanceY(g3,g0) = 35
    c: DistanceY(g0,g1) = 35
    c: DistanceY(g10,g4) = 35
    c: DistanceY(g6,g10) = 0
    c: DistanceY(g10,g5) = 0
    c: DistanceY(g7,g11) = 35
    c: DistanceY(g11,g9) = 35
    c: DistanceX(g3,g1) = 0
    c: DistanceY(g10,g0) = 57
    c: Diameter(g10) = 9
    c: DistanceX(g12,g0) = 35
    c: DistanceY(g0,g13) = 57
    c: DistanceX(g0,g13) = 35
    c: Equal(g1,g12)
    c: Equal(g1,g13)
    c: Equal(g1,g9)
    c: Equal(g1,g7)
    c: Equal(g1,g6)
    c: Equal(g1,g5)
    c: Equal(g1,g3)
    c: Diameter(g1) = 4.25
    c: Equal(g4,g8)
    c: Equal(g4,g14)
    c: Equal(g4,g2)
    c: Diameter(g4) = 8
    c: DistanceY(g0,g14) = 22
    c: DistanceY(g0,g12) = 57
FEATURE [Part::Extrusion] Extrude008  label="level002"
  Base = -> Sketch008
  Dir = (0,0,1)
  DirMode = 2
  FaceMakerClass = Part::FaceMakerBullseye
  LengthFwd = 5
  LengthRev = 0
  Placement = pos=(0,0,15) rot=(0,0,1;0rad)
  Solid = true
  Symmetric = false
FEATURE [Part::Box] Box009  label="Cube002"
  AttacherType = Attacher::AttachEngine3D
  Height = 15
  Length = 10
  Placement = pos=(-25,-180,20) rot=(0,0,1;0rad)
  Width = 10
FEATURE [Part::Box] Box010  label="Cube003"
  AttacherType = Attacher::AttachEngine3D
  Height = 50
  Length = 10
  Placement = pos=(15,-180,20) rot=(0,0,1;0rad)
  Width = 10
FEATURE [Part::Box] Box011  label="Cube004"
  AttacherType = Attacher::AttachEngine3D
  Height = 35
  Length = 10
  Placement = pos=(20,-165,20) rot=(0,0,1;0rad)
  Width = 10
FEATURE [Part::Box] Box012  label="Cube005"
  AttacherType = Attacher::AttachEngine3D
  Height = 35
  Length = 10
  Placement = pos=(-30,-165,20) rot=(0,0,1;0rad)
  Width = 10
FEATURE [Part::Box] Box013  label="Cube006"
  AttacherType = Attacher::AttachEngine3D
  Height = 35
  Length = 10
  Placement = pos=(-30,-145,20) rot=(0,0,1;0rad)
  Width = 10
FEATURE [Part::Box] Box014  label="Cube007"
  AttacherType = Attacher::AttachEngine3D
  Height = 35
  Length = 10
  Placement = pos=(20,-145,20) rot=(0,0,1;0rad)
  Width = 10
FEATURE [Part::Box] Box015  label="Cube008"
  AttacherType = Attacher::AttachEngine3D
  Height = 35
  Length = 10
  Placement = pos=(-20,-130,20) rot=(0,0,1;0rad)
  Width = 10
FEATURE [Part::Box] Box016  label="Cube009"
  AttacherType = Attacher::AttachEngine3D
  Height = 17.5
  Length = 10
  Placement = pos=(12.5,-130,20) rot=(0,0,1;0rad)
  Width = 10
FEATURE [Part::MultiFuse] Fusion056  label="airSensorHolds"
  Shapes = -> [Box016,Box009,Box010,Box011,Box012,Box013,Box014,Box015]
FEATURE [Part::Cylinder] Cylinder102  label="m2Cuts"
  Angle = 360
  AttacherType = Attacher::AttachEngine3D
  FirstAngle = 0
  Height = 10
  Placement = pos=(-20.4,-170,28.6) rot=(1,0,0;1.5708rad)
  Radius = 1.13
  SecondAngle = 0
FEATURE [Part::Cylinder] Cylinder103  label="m2Cuts001"
  Angle = 360
  AttacherType = Attacher::AttachEngine3D
  FirstAngle = 0
  Height = 10
  Placement = pos=(20.4,-170,65.4) rot=(1,0,0;1.5708rad)
  Radius = 1.13
  SecondAngle = 0
FEATURE [Part::Cylinder] Cylinder104  label="m2Cuts002"
  Angle = 360
  AttacherType = Attacher::AttachEngine3D
  FirstAngle = 0
  Height = 10
  Placement = pos=(17.45,-120,33.2) rot=(1,0,0;1.5708rad)
  Radius = 1.13
  SecondAngle = 0
FEATURE [Part::Cylinder] Cylinder105  label="m2Cuts003"
  Angle = 360
  AttacherType = Attacher::AttachEngine3D
  FirstAngle = 0
  Height = 10
  Placement = pos=(-14.55,-120,49.4) rot=(1,0,0;1.5708rad)
  Radius = 1.1
  SecondAngle = 0
FEATURE [Part::Cylinder] Cylinder106  label="m2Cuts004"
  Angle = 360
  AttacherType = Attacher::AttachEngine3D
  FirstAngle = 0
  Height = 60
  Placement = pos=(-30,-159.9,38.65) rot=(0.57735,0.57735,0.57735;2.0944rad)
  Radius = 1.13
  SecondAngle = 0
FEATURE [Part::Cylinder] Cylinder107  label="m2Cuts005"
  Angle = 360
  AttacherType = Attacher::AttachEngine3D
  FirstAngle = 0
  Height = 60
  Placement = pos=(-30,-139.6,38.65) rot=(0.57735,0.57735,0.57735;2.0944rad)
  Radius = 1.13
  SecondAngle = 0
FEATURE [Part::Cylinder] Cylinder108  label="m2Cuts006"
  Angle = 360
  AttacherType = Attacher::AttachEngine3D
  FirstAngle = 0
  Height = 60
  Placement = pos=(-30,-159.9,51.35) rot=(0.57735,0.57735,0.57735;2.0944rad)
  Radius = 1.13
  SecondAngle = 0
FEATURE [Part::Cylinder] Cylinder109  label="m2Cuts007"
  Angle = 360
  AttacherType = Attacher::AttachEngine3D
  FirstAngle = 0
  Height = 60
  Placement = pos=(-30,-139.6,51.35) rot=(0.57735,0.57735,0.57735;2.0944rad)
  Radius = 1.13
  SecondAngle = 0
FEATURE [Part::MultiFuse] Fusion057  label="m2Cuts008"
  Shapes = -> [Cylinder109,Cylinder102,Cylinder103,Cylinder104,Cylinder105,Cylinder106,Cylinder107,Cylinder108]
FEATURE [Part::Cut] Cut021  label="airSesnorHolds"
  Base = -> Fusion056
  Tool = -> Fusion057
FEATURE [Sketcher::SketchObject] Sketch011
  FullyConstrained = true
  Placement = pos=(0,0,65) rot=(0,0,1;0rad)
  sketch-geometry (1):
    g0: Circle CenterX=0 CenterY=-150 CenterZ=0 NormalX=0 NormalY=0 NormalZ=1 AngleXU=0 Radius=98
  constraints (3):
    c: PointOnObject(g0,g-2)
    c: DistanceY(g0) = -150
    c: Radius(g0) = 98
FEATURE [Sketcher::SketchObject] Sketch012
  FullyConstrained = true
  Placement = pos=(0,0,80) rot=(0,0,1;0rad)
  sketch-geometry (1):
    g0: Circle CenterX=0 CenterY=-150 CenterZ=0 NormalX=0 NormalY=0 NormalZ=1 AngleXU=0 Radius=80
  constraints (3):
    c: PointOnObject(g0,g-2)
    c: DistanceY(g0) = -150
    c: Radius(g0) = 80
FEATURE [Part::Loft] Loft001
  Closed = false
  MaxDegree = 5
  Placement = pos=(0,0,-15) rot=(0,0,1;0rad)
  Ruled = false
  Sections = -> [Sketch012,Sketch011]
  Solid = true
FEATURE [Sketcher::SketchObject] Sketch013
  FullyConstrained = true
  Placement = pos=(0,0,65) rot=(0,0,1;0rad)
  sketch-geometry (1):
    g0: Circle CenterX=0 CenterY=-150 CenterZ=0 NormalX=0 NormalY=0 NormalZ=1 AngleXU=0 Radius=98
  constraints (3):
    c: PointOnObject(g0,g-2)
    c: DistanceY(g0) = -150
    c: Radius(g0) = 98
FEATURE [Sketcher::SketchObject] Sketch014
  FullyConstrained = true
  Placement = pos=(0,0,80) rot=(0,0,1;0rad)
  sketch-geometry (1):
    g0: Circle CenterX=0 CenterY=-150 CenterZ=0 NormalX=0 NormalY=0 NormalZ=1 AngleXU=0 Radius=80
  constraints (3):
    c: PointOnObject(g0,g-2)
    c: DistanceY(g0) = -150
    c: Radius(g0) = 80
FEATURE [Part::Loft] Loft002
  Closed = false
  MaxDegree = 5
  Placement = pos=(0,0,-20) rot=(0,0,1;0rad)
  Ruled = false
  Sections = -> [Sketch014,Sketch013]
  Solid = true
FEATURE [Part::Cut] Cut022  label="Loft003"
  Base = -> Loft001
  Tool = -> Loft002
FEATURE [Sketcher::SketchObject] Sketch015
  FullyConstrained = true
  Placement = pos=(0,0,65) rot=(0,0,1;0rad)
  sketch-geometry (1):
    g0: Circle CenterX=0 CenterY=-150 CenterZ=0 NormalX=0 NormalY=0 NormalZ=1 AngleXU=0 Radius=98
  constraints (3):
    c: PointOnObject(g0,g-2)
    c: DistanceY(g0) = -150
    c: Radius(g0) = 98
FEATURE [Sketcher::SketchObject] Sketch016
  FullyConstrained = true
  Placement = pos=(0,0,80) rot=(0,0,1;0rad)
  sketch-geometry (1):
    g0: Circle CenterX=0 CenterY=-150 CenterZ=0 NormalX=0 NormalY=0 NormalZ=1 AngleXU=0 Radius=80
  constraints (3):
    c: PointOnObject(g0,g-2)
    c: DistanceY(g0) = -150
    c: Radius(g0) = 80
FEATURE [Part::Loft] Loft003  label="Loft005"
  Closed = false
  MaxDegree = 5
  Placement = pos=(0,0,-15) rot=(0,0,1;0rad)
  Ruled = false
  Sections = -> [Sketch016,Sketch015]
  Solid = true
FEATURE [Sketcher::SketchObject] Sketch017
  FullyConstrained = true
  Placement = pos=(0,0,65) rot=(0,0,1;0rad)
  sketch-geometry (1):
    g0: Circle CenterX=0 CenterY=-150 CenterZ=0 NormalX=0 NormalY=0 NormalZ=1 AngleXU=0 Radius=98
  constraints (3):
    c: PointOnObject(g0,g-2)
    c: DistanceY(g0) = -150
    c: Radius(g0) = 98
FEATURE [Sketcher::SketchObject] Sketch018
  FullyConstrained = true
  Placement = pos=(0,0,80) rot=(0,0,1;0rad)
  sketch-geometry (1):
    g0: Circle CenterX=0 CenterY=-150 CenterZ=0 NormalX=0 NormalY=0 NormalZ=1 AngleXU=0 Radius=80
  constraints (3):
    c: PointOnObject(g0,g-2)
    c: DistanceY(g0) = -150
    c: Radius(g0) = 80
FEATURE [Part::Loft] Loft004  label="Loft006"
  Closed = false
  MaxDegree = 5
  Placement = pos=(0,0,-20) rot=(0,0,1;0rad)
  Ruled = false
  Sections = -> [Sketch018,Sketch017]
  Solid = true
FEATURE [Part::Cut] Cut023  label="Loft004"
  Base = -> Loft003
  Placement = pos=(0,0,-15) rot=(0,0,1;0rad)
  Tool = -> Loft004
FEATURE [Sketcher::SketchObject] Sketch019
  FullyConstrained = true
  Placement = pos=(0,0,65) rot=(0,0,1;0rad)
  sketch-geometry (1):
    g0: Circle CenterX=0 CenterY=-150 CenterZ=0 NormalX=0 NormalY=0 NormalZ=1 AngleXU=0 Radius=98
  constraints (3):
    c: PointOnObject(g0,g-2)
    c: DistanceY(g0) = -150
    c: Radius(g0) = 98
FEATURE [Sketcher::SketchObject] Sketch020
  FullyConstrained = true
  Placement = pos=(0,0,80) rot=(0,0,1;0rad)
  sketch-geometry (1):
    g0: Circle CenterX=0 CenterY=-150 CenterZ=0 NormalX=0 NormalY=0 NormalZ=1 AngleXU=0 Radius=80
  constraints (3):
    c: PointOnObject(g0,g-2)
    c: DistanceY(g0) = -150
    c: Radius(g0) = 80
FEATURE [Part::Loft] Loft005  label="Loft008"
  Closed = false
  MaxDegree = 5
  Placement = pos=(0,0,-15) rot=(0,0,1;0rad)
  Ruled = false
  Sections = -> [Sketch020,Sketch019]
  Solid = true
FEATURE [Sketcher::SketchObject] Sketch021
  FullyConstrained = true
  Placement = pos=(0,0,65) rot=(0,0,1;0rad)
  sketch-geometry (1):
    g0: Circle CenterX=0 CenterY=-150 CenterZ=0 NormalX=0 NormalY=0 NormalZ=1 AngleXU=0 Radius=98
  constraints (3):
    c: PointOnObject(g0,g-2)
    c: DistanceY(g0) = -150
    c: Radius(g0) = 98
FEATURE [Sketcher::SketchObject] Sketch022
  FullyConstrained = true
  Placement = pos=(0,0,80) rot=(0,0,1;0rad)
  sketch-geometry (1):
    g0: Circle CenterX=0 CenterY=-150 CenterZ=0 NormalX=0 NormalY=0 NormalZ=1 AngleXU=0 Radius=80
  constraints (3):
    c: PointOnObject(g0,g-2)
    c: DistanceY(g0) = -150
    c: Radius(g0) = 80
FEATURE [Part::Loft] Loft006  label="Loft009"
  Closed = false
  MaxDegree = 5
  Placement = pos=(0,0,-20) rot=(0,0,1;0rad)
  Ruled = false
  Sections = -> [Sketch022,Sketch021]
  Solid = true
FEATURE [Part::Cut] Cut024  label="Loft007"
  Base = -> Loft005
  Placement = pos=(0,0,-30) rot=(0,0,1;0rad)
  Tool = -> Loft006
FEATURE [Sketcher::SketchObject] Sketch023
  FullyConstrained = true
  Placement = pos=(0,0,65) rot=(0,0,1;0rad)
  sketch-geometry (1):
    g0: Circle CenterX=0 CenterY=-150 CenterZ=0 NormalX=0 NormalY=0 NormalZ=1 AngleXU=0 Radius=98
  constraints (3):
    c: PointOnObject(g0,g-2)
    c: DistanceY(g0) = -150
    c: Radius(g0) = 98
FEATURE [Sketcher::SketchObject] Sketch024
  FullyConstrained = true
  Placement = pos=(0,0,80) rot=(0,0,1;0rad)
  sketch-geometry (1):
    g0: Circle CenterX=0 CenterY=-150 CenterZ=0 NormalX=0 NormalY=0 NormalZ=1 AngleXU=0 Radius=80
  constraints (3):
    c: PointOnObject(g0,g-2)
    c: DistanceY(g0) = -150
    c: Radius(g0) = 80
FEATURE [Part::Loft] Loft007  label="Loft011"
  Closed = false
  MaxDegree = 5
  Placement = pos=(0,0,-15) rot=(0,0,1;0rad)
  Ruled = false
  Sections = -> [Sketch024,Sketch023]
  Solid = true
FEATURE [Sketcher::SketchObject] Sketch025
  FullyConstrained = true
  Placement = pos=(0,0,65) rot=(0,0,1;0rad)
  sketch-geometry (1):
    g0: Circle CenterX=0 CenterY=-150 CenterZ=0 NormalX=0 NormalY=0 NormalZ=1 AngleXU=0 Radius=98
  constraints (3):
    c: PointOnObject(g0,g-2)
    c: DistanceY(g0) = -150
    c: Radius(g0) = 98
FEATURE [Sketcher::SketchObject] Sketch026
  FullyConstrained = true
  Placement = pos=(0,0,80) rot=(0,0,1;0rad)
  sketch-geometry (1):
    g0: Circle CenterX=0 CenterY=-150 CenterZ=0 NormalX=0 NormalY=0 NormalZ=1 AngleXU=0 Radius=80
  constraints (3):
    c: PointOnObject(g0,g-2)
    c: DistanceY(g0) = -150
    c: Radius(g0) = 80
FEATURE [Part::Loft] Loft008  label="Loft012"
  Closed = false
  MaxDegree = 5
  Placement = pos=(0,0,-20) rot=(0,0,1;0rad)
  Ruled = false
  Sections = -> [Sketch026,Sketch025]
  Solid = true
FEATURE [Part::Cut] Cut025  label="Loft010"
  Base = -> Loft007
  Placement = pos=(0,0,15) rot=(0,0,1;0rad)
  Tool = -> Loft008
FEATURE [Part::Cylinder] Cylinder110
  Angle = 360
  AttacherType = Attacher::AttachEngine3D
  FirstAngle = 0
  Height = 10
  Placement = pos=(0,-150,75) rot=(0,0,1;0rad)
  Radius = 98
  SecondAngle = 0
FEATURE [Part::Cut] Cut026  label="top009"
  Base = -> Cut025
  Tool = -> Cylinder110
FEATURE [Part::Cylinder] Cylinder111
  Angle = 360
  AttacherType = Attacher::AttachEngine3D
  FirstAngle = 0
  Height = 5
  Placement = pos=(0,-150,70) rot=(0,0,1;0rad)
  Radius = 86
  SecondAngle = 0
FEATURE [Part::MultiFuse] Fusion058  label="top010"
  Shapes = -> [Cut026,Cylinder111]
FEATURE [Part::MultiFuse] Fusion059  label="solarRadiationShield"
  Shapes = -> [Fusion058,Cut022,Cut023,Cut024]
FEATURE [Sketcher::SketchObject] Sketch028
  FullyConstrained = true
  sketch-geometry (16):
    g0: ArcOfCircle CenterX=0 CenterY=-150 CenterZ=0 NormalX=0 NormalY=0 NormalZ=1 AngleXU=0 Radius=85 StartAngle=2.84306 EndAngle=3.44012
    g1: ArcOfCircle CenterX=0 CenterY=-150 CenterZ=0 NormalX=0 NormalY=0 NormalZ=1 AngleXU=0 Radius=85 StartAngle=1.27226 EndAngle=1.86933
    g2: ArcOfCircle CenterX=0 CenterY=-150 CenterZ=0 NormalX=0 NormalY=0 NormalZ=1 AngleXU=0 Radius=85 StartAngle=5.98465 EndAngle=6.58172
    g3: ArcOfCircle CenterX=0 CenterY=-150 CenterZ=0 NormalX=0 NormalY=0 NormalZ=1 AngleXU=0 Radius=85 StartAngle=4.41386 EndAngle=5.01092
    g4: ArcOfCircle CenterX=0 CenterY=-150 CenterZ=0 NormalX=0 NormalY=0 NormalZ=1 AngleXU=0 Radius=79 StartAngle=1.24881 EndAngle=1.89279
    g5: ArcOfCircle CenterX=0 CenterY=-150 CenterZ=0 NormalX=0 NormalY=0 NormalZ=1 AngleXU=0 Radius=79 StartAngle=5.96119 EndAngle=6.60518
    g6: ArcOfCircle CenterX=0 CenterY=-150 CenterZ=0 NormalX=0 NormalY=0 NormalZ=1 AngleXU=0 Radius=79 StartAngle=2.8196 EndAngle=3.46358
    g7: ArcOfCircle CenterX=0 CenterY=-150 CenterZ=0 NormalX=0 NormalY=0 NormalZ=1 AngleXU=0 Radius=79 StartAngle=4.3904 EndAngle=5.03438
    g8: LineSegment StartX=25 StartY=-68.7596 StartZ=0 EndX=25 EndY=-75.06 EndZ=0
    g9: LineSegment StartX=-25 StartY=-68.7596 StartZ=0 EndX=-25 EndY=-75.06 EndZ=0
    g10: LineSegment StartX=-81.2404 StartY=-125 StartZ=0 EndX=-74.94 EndY=-125 EndZ=0
    g11: LineSegment StartX=-81.2404 StartY=-175 StartZ=0 EndX=-74.94 EndY=-175 EndZ=0
    g12: LineSegment StartX=-25 StartY=-231.24 StartZ=0 EndX=-25 EndY=-224.94 EndZ=0
    g13: LineSegment StartX=25 StartY=-231.24 StartZ=0 EndX=25 EndY=-224.94 EndZ=0
    g14: LineSegment StartX=81.2404 StartY=-175 StartZ=0 EndX=74.94 EndY=-175 EndZ=0
    g15: LineSegment StartX=81.2404 StartY=-125 StartZ=0 EndX=74.94 EndY=-125 EndZ=0
  constraints (49):
    c: PointOnObject(g0,g-2)
    c: Coincident(g1,g0)
    c: Coincident(g2,g0)
    c: Coincident(g3,g0)
    c: DistanceY(g0) = -150
    c: Coincident(g4,g0)
    c: Coincident(g5,g0)
    c: Coincident(g6,g0)
    c: Coincident(g7,g0)
    c: DistanceX(g4,g0) = 25
    c: DistanceX(g1,g4) = 0
    c: DistanceX(g0,g4) = 25
    c: DistanceX(g4,g1) = 0
    c: DistanceY(g0,g5) = 25
    c: DistanceY(g5,g2) = 0
    c: DistanceY(g2,g0) = 25
    c: DistanceY(g2,g5) = 0
    c: DistanceY(g6,g0) = 25
    c: DistanceY(g0,g6) = 0
    c: DistanceY(g0,g6) = 25
    c: DistanceY(g6,g0) = 0
    c: Equal(g1,g2)
    c: Equal(g1,g3)
    c: Equal(g1,g0)
    c: Radius(g1) = 85  'outer'
    c: Equal(g6,g4)
    c: Equal(g6,g5)
    c: Equal(g6,g7)
    c: Radius(g6) = 79
    c: DistanceX(g0,g7) = 25
    c: DistanceX(g7,g3) = 0
    c: DistanceX(g3) = -25
    c: DistanceX(g3,g7) = 0
    c: Coincident(g8,g1)
    c: Coincident(g8,g4)
    c: Coincident(g9,g1)
    c: Coincident(g9,g4)
    c: Coincident(g10,g0)
    c: Coincident(g10,g6)
    c: Coincident(g11,g0)
    c: Coincident(g11,g6)
    c: Coincident(g12,g3)
    c: Coincident(g12,g7)
    c: Coincident(g13,g3)
    c: Coincident(g13,g7)
    c: Coincident(g14,g2)
    c: Coincident(g14,g5)
    c: Coincident(g15,g2)
    c: Coincident(g15,g5)
FEATURE [Part::Extrusion] Extrude010  label="srsHolds"
  Base = -> Sketch028
  Dir = (0,0,1)
  DirMode = 2
  FaceMakerClass = Part::FaceMakerBullseye
  LengthFwd = 20
  LengthRev = 0
  Placement = pos=(0,0,75) rot=(0,0,1;0rad)
  Solid = true
  Symmetric = false
FEATURE [Part::Cylinder] Cylinder112
  Angle = 360
  AttacherType = Attacher::AttachEngine3D
  FirstAngle = 0
  Height = 300
  Placement = pos=(0,0,90) rot=(1,0,0;1.5708rad)
  Radius = 2.8
  SecondAngle = 0
FEATURE [Part::Cylinder] Cylinder113
  Angle = 360
  AttacherType = Attacher::AttachEngine3D
  FirstAngle = 0
  Height = 300
  Placement = pos=(-150,-150,90) rot=(0.57735,0.57735,0.57735;2.0944rad)
  Radius = 2.8
  SecondAngle = 0
FEATURE [Part::MultiFuse] Fusion062  label="m4Cuts001"
  Shapes = -> [Cylinder113,Cylinder112]
FEATURE [Part::MultiFuse] Fusion063  label="level2"
  Shapes = -> [Cut021,Extrude008]
FEATURE [Sketcher::SketchObject] Sketch030  label="top011"
  FullyConstrained = true
  sketch-geometry (10):
    g0: Circle CenterX=-57 CenterY=-115 CenterZ=0 NormalX=0 NormalY=0 NormalZ=1 AngleXU=0 Radius=2.125
    g1: Circle CenterX=-57 CenterY=-185 CenterZ=0 NormalX=0 NormalY=0 NormalZ=1 AngleXU=0 Radius=2.125
    g2: Circle CenterX=-35 CenterY=-207 CenterZ=0 NormalX=0 NormalY=0 NormalZ=1 AngleXU=0 Radius=2.125
    g3: Circle CenterX=-35 CenterY=-93 CenterZ=0 NormalX=0 NormalY=0 NormalZ=1 AngleXU=0 Radius=2.125
    g4: Circle CenterX=-4.2 CenterY=-109.55 CenterZ=0 NormalX=0 NormalY=0 NormalZ=1 AngleXU=0 Radius=1.5
    g5: Circle CenterX=-58.33 CenterY=-148.9 CenterZ=0 NormalX=0 NormalY=0 NormalZ=1 AngleXU=0 Radius=1.5
    g6: Circle CenterX=-4.2 CenterY=-180.9 CenterZ=0 NormalX=0 NormalY=0 NormalZ=1 AngleXU=0 Radius=1.5
    g7: Circle CenterX=0 CenterY=-150 CenterZ=0 NormalX=0 NormalY=0 NormalZ=1 AngleXU=0 Radius=92.5
    g8: ArcOfCircle CenterX=0 CenterY=-150 CenterZ=0 NormalX=0 NormalY=0 NormalZ=1 AngleXU=0 Radius=78 StartAngle=4.71239 EndAngle=7.85398
    g9: LineSegment StartX=2.39e-14 StartY=-72 StartZ=0 EndX=-1.43e-14 EndY=-228 EndZ=0
  constraints (30):
    c: DistanceX(g1,g0) = 0
    c: Equal(g0,g3)
    c: Equal(g0,g2)
    c: Equal(g0,g1)
    c: Diameter(g0) = 4.25
    c: DistanceY(g6) = -180.9
    c: DistanceX(g4,g6) = 0
    c: DistanceY(g6,g4) = 71.35
    c: DistanceX(g5,g6) = 54.13
    c: DistanceY(g6,g5) = 32
    c: Equal(g5,g6)
    c: Equal(g5,g4)
    c: Diameter(g5) = 3
    c: PointOnObject(g7,g-2)
    c: Diameter(g7) = 185
    c: DistanceY(g7) = -150
    c: DistanceX(g1,g7) = 57
    c: DistanceY(g1,g7) = 35
    c: DistanceY(g7,g0) = 35
    c: DistanceX(g3,g7) = 35
    c: DistanceY(g7,g3) = 57
    c: DistanceX(g4) = -4.2
    c: Coincident(g8,g7)
    c: PointOnObject(g8,g-2)
    c: DistanceX(g7,g8) = 0
    c: Coincident(g9,g8)
    c: Coincident(g9,g8)
    c: Diameter(g8) = 156
    c: DistanceX(g2) = -35
    c: DistanceY(g2,g7) = 57
FEATURE [Part::Extrusion] Extrude012  label="level003"
  Base = -> Sketch030
  Dir = (0,0,1)
  DirMode = 2
  FaceMakerClass = Part::FaceMakerBullseye
  LengthFwd = 5
  LengthRev = 0
  Placement = pos=(0,0,-60) rot=(0,0,1;0rad)
  Solid = true
  Symmetric = false
FEATURE [Part::Feature] Part__Feature195  label="srsRefLightModuke"
  Placement = pos=(-15,-170,-30) rot=(0.57735,-0.57735,0.57735;4.18879rad)
  shape: bbox 63.5 x 88.9 x 31.45 mm, 876 faces (baked)
FEATURE [Part::Cylinder] Cylinder114
  Angle = 270
  AttacherType = Attacher::AttachEngine3D
  FirstAngle = 0
  Height = 30
  Placement = pos=(0,-150,0) rot=(0,0,1;1.5708rad)
  Radius = 82
  SecondAngle = 0
FEATURE [Part::Cylinder] Cylinder115
  Angle = 270
  AttacherType = Attacher::AttachEngine3D
  FirstAngle = 0
  Height = 30
  Placement = pos=(0,-150,0) rot=(0,0,1;1.5708rad)
  Radius = 78
  SecondAngle = 0
FEATURE [Part::Cut] Cut028
  Base = -> Cylinder114
  Placement = pos=(0,0,-55) rot=(0,0,1;0rad)
  Tool = -> Cylinder115
FEATURE [Part::FeaturePython] Tube002  label="tube3to2"  # WARN: FeaturePython — macro-defined, semantics opaque (R4)
  AttacherType = Attacher::AttachEngine3D
  Height = 80
  InnerRadius = 94
  OuterRadius = 98
  Placement = pos=(0,-150,-60) rot=(0,0,1;0rad)
FEATURE [Part::Cylinder] Cylinder120  label="srsCut"
  Angle = 360
  AttacherType = Attacher::AttachEngine3D
  FirstAngle = 0
  Height = 100
  Placement = pos=(0,-150,0) rot=(0,0,1;0rad)
  Radius = 80
  SecondAngle = 0
FEATURE [Sketcher::SketchObject] Sketch031
  FullyConstrained = true
  sketch-geometry (16):
    g0: ArcOfCircle CenterX=0 CenterY=-150 CenterZ=0 NormalX=0 NormalY=0 NormalZ=1 AngleXU=0 Radius=93 StartAngle=2.86943 EndAngle=3.41376
    g1: ArcOfCircle CenterX=0 CenterY=-150 CenterZ=0 NormalX=0 NormalY=0 NormalZ=1 AngleXU=0 Radius=93 StartAngle=1.29863 EndAngle=1.84296
    g2: ArcOfCircle CenterX=0 CenterY=-150 CenterZ=0 NormalX=0 NormalY=0 NormalZ=1 AngleXU=0 Radius=93 StartAngle=6.01102 EndAngle=6.55535
    g3: ArcOfCircle CenterX=0 CenterY=-150 CenterZ=0 NormalX=0 NormalY=0 NormalZ=1 AngleXU=0 Radius=93 StartAngle=4.44022 EndAngle=4.98455
    g4: ArcOfCircle CenterX=0 CenterY=-150 CenterZ=0 NormalX=0 NormalY=0 NormalZ=1 AngleXU=0 Radius=86 StartAngle=1.27584 EndAngle=1.86575
    g5: ArcOfCircle CenterX=0 CenterY=-150 CenterZ=0 NormalX=0 NormalY=0 NormalZ=1 AngleXU=0 Radius=86 StartAngle=5.98823 EndAngle=6.57814
    g6: ArcOfCircle CenterX=0 CenterY=-150 CenterZ=0 NormalX=0 NormalY=0 NormalZ=1 AngleXU=0 Radius=86 StartAngle=2.84664 EndAngle=3.43655
    g7: ArcOfCircle CenterX=0 CenterY=-150 CenterZ=0 NormalX=0 NormalY=0 NormalZ=1 AngleXU=0 Radius=86 StartAngle=4.41743 EndAngle=5.00734
    g8: LineSegment StartX=25 StartY=-60.4232 StartZ=0 EndX=25 EndY=-67.7139 EndZ=0
    g9: LineSegment StartX=-25 StartY=-60.4232 StartZ=0 EndX=-25 EndY=-67.7139 EndZ=0
    g10: LineSegment StartX=-89.5768 StartY=-125 StartZ=0 EndX=-82.2861 EndY=-125 EndZ=0
    g11: LineSegment StartX=-89.5768 StartY=-175 StartZ=0 EndX=-82.2861 EndY=-175 EndZ=0
    g12: LineSegment StartX=-25 StartY=-239.577 StartZ=0 EndX=-25 EndY=-232.286 EndZ=0
    g13: LineSegment StartX=25 StartY=-239.577 StartZ=0 EndX=25 EndY=-232.286 EndZ=0
    g14: LineSegment StartX=89.5768 StartY=-175 StartZ=0 EndX=82.2861 EndY=-175 EndZ=0
    g15: LineSegment StartX=89.5768 StartY=-125 StartZ=0 EndX=82.2861 EndY=-125 EndZ=0
  constraints (49):
    c: PointOnObject(g0,g-2)
    c: Coincident(g1,g0)
    c: Coincident(g2,g0)
    c: Coincident(g3,g0)
    c: DistanceY(g0) = -150
    c: Coincident(g4,g0)
    c: Coincident(g5,g0)
    c: Coincident(g6,g0)
    c: Coincident(g7,g0)
    c: DistanceX(g4,g0) = 25
    c: DistanceX(g1,g4) = 0
    c: DistanceX(g0,g4) = 25
    c: DistanceX(g4,g1) = 0
    c: DistanceY(g0,g5) = 25
    c: DistanceY(g5,g2) = 0
    c: DistanceY(g2,g0) = 25
    c: DistanceY(g2,g5) = 0
    c: DistanceY(g6,g0) = 25
    c: DistanceY(g0,g6) = 0
    c: DistanceY(g0,g6) = 25
    c: DistanceY(g6,g0) = 0
    c: Equal(g1,g2)
    c: Equal(g1,g3)
    c: Equal(g1,g0)
    c: Radius(g1) = 93
    c: Equal(g6,g4)
    c: Equal(g6,g5)
    c: Equal(g6,g7)
    c: Radius(g6) = 86
    c: DistanceX(g0,g7) = 25
    c: DistanceX(g7,g3) = 0
    c: DistanceX(g3) = -25
    c: DistanceX(g3,g7) = 0
    c: Coincident(g8,g1)
    c: Coincident(g8,g4)
    c: Coincident(g9,g1)
    c: Coincident(g9,g4)
    c: Coincident(g10,g0)
    c: Coincident(g10,g6)
    c: Coincident(g11,g0)
    c: Coincident(g11,g6)
    c: Coincident(g12,g3)
    c: Coincident(g12,g7)
    c: Coincident(g13,g3)
    c: Coincident(g13,g7)
    c: Coincident(g14,g2)
    c: Coincident(g14,g5)
    c: Coincident(g15,g2)
    c: Coincident(g15,g5)
FEATURE [Part::Extrusion] Extrude013  label="srsHolds001"
  Base = -> Sketch031
  Dir = (0,0,1)
  DirMode = 2
  FaceMakerClass = Part::FaceMakerBullseye
  LengthFwd = 95.5
  LengthRev = 0
  Solid = true
  Symmetric = false
FEATURE [Part::MultiFuse] Fusion065  label="srs"
  Shapes = -> [Fusion059,Extrude013]
FEATURE [Part::MultiFuse] Fusion066  label="srsCut001"
  Shapes = -> [Cylinder120,Fusion062]
FEATURE [Part::Cut] Cut031  label="srs001"
  Base = -> Fusion065
  Tool = -> Fusion066
FEATURE [Part::MultiFuse] Fusion067  label="level3"
  Shapes = -> [Extrude012,Cut028]
FEATURE [Part::Cylinder] Cylinder121
  Angle = 360
  AttacherType = Attacher::AttachEngine3D
  FirstAngle = 0
  Height = 300
  Placement = pos=(0,0,90) rot=(1,0,0;1.5708rad)
  Radius = 2.8
  SecondAngle = 0
FEATURE [Part::Cylinder] Cylinder122
  Angle = 360
  AttacherType = Attacher::AttachEngine3D
  FirstAngle = 0
  Height = 300
  Placement = pos=(-150,-150,90) rot=(0.57735,0.57735,0.57735;2.0944rad)
  Radius = 2.8
  SecondAngle = 0
FEATURE [Part::MultiFuse] Fusion068  label="m4Cuts002"
  Shapes = -> [Cylinder122,Cylinder121]
FEATURE [Part::Cut] Cut032  label="srsHold"
  Base = -> Extrude010
  Tool = -> Fusion068
FEATURE [Part::MultiFuse] Fusion069  label="level001"
  Shapes = -> [Cut032,Fusion054]
FEATURE [Sketcher::SketchObject] Sketch032
  FullyConstrained = true
  sketch-geometry (16):
    g0: ArcOfCircle CenterX=0 CenterY=-150 CenterZ=0 NormalX=0 NormalY=0 NormalZ=1 AngleXU=0 Radius=92.5 StartAngle=3.68087 EndAngle=4.17311
    g1: ArcOfCircle CenterX=0 CenterY=-150 CenterZ=0 NormalX=0 NormalY=0 NormalZ=1 AngleXU=0 Radius=92.5 StartAngle=2.11007 EndAngle=2.60232
    g2: ArcOfCircle CenterX=0 CenterY=-150 CenterZ=0 NormalX=0 NormalY=0 NormalZ=1 AngleXU=0 Radius=92.5 StartAngle=0.539274 EndAngle=1.03152
    g3: ArcOfCircle CenterX=0 CenterY=-150 CenterZ=0 NormalX=0 NormalY=0 NormalZ=1 AngleXU=0 Radius=92.5 StartAngle=5.25166 EndAngle=5.74391
    g4: ArcOfCircle CenterX=0 CenterY=-150 CenterZ=0 NormalX=0 NormalY=0 NormalZ=1 AngleXU=0 Radius=85 StartAngle=2.1287 EndAngle=2.58369
    g5: ArcOfCircle CenterX=0 CenterY=-150 CenterZ=0 NormalX=0 NormalY=0 NormalZ=1 AngleXU=0 Radius=85 StartAngle=0.557907 EndAngle=1.01289
    g6: ArcOfCircle CenterX=0 CenterY=-150 CenterZ=0 NormalX=0 NormalY=0 NormalZ=1 AngleXU=0 Radius=85 StartAngle=3.6995 EndAngle=4.15448
    g7: ArcOfCircle CenterX=0 CenterY=-150 CenterZ=0 NormalX=0 NormalY=0 NormalZ=1 AngleXU=0 Radius=85 StartAngle=5.2703 EndAngle=5.72528
    g8: LineSegment StartX=-47.5 StartY=-70.6275 StartZ=0 EndX=-45 EndY=-77.889 EndZ=0
    g9: LineSegment StartX=-79.3725 StartY=-102.5 StartZ=0 EndX=-72.111 EndY=-105 EndZ=0
    g10: LineSegment StartX=-79.3725 StartY=-197.5 StartZ=0 EndX=-72.111 EndY=-195 EndZ=0
    g11: LineSegment StartX=-47.5 StartY=-229.373 StartZ=0 EndX=-45 EndY=-222.111 EndZ=0
    g12: LineSegment StartX=47.5 StartY=-229.373 StartZ=0 EndX=45 EndY=-222.111 EndZ=0
    g13: LineSegment StartX=79.3725 StartY=-102.5 StartZ=0 EndX=72.111 EndY=-105 EndZ=0
    g14: LineSegment StartX=47.5 StartY=-70.6275 StartZ=0 EndX=45 EndY=-77.889 EndZ=0
    g15: LineSegment StartX=72.111 StartY=-195 StartZ=0 EndX=79.3725 EndY=-197.5 EndZ=0
  constraints (49):
    c: Coincident(g1,g0)
    c: Coincident(g2,g0)
    c: DistanceY(g0) = -150
    c: Coincident(g4,g0)
    c: Coincident(g5,g0)
    c: Coincident(g6,g0)
    c: Coincident(g8,g1)
    c: Coincident(g8,g4)
    c: Coincident(g9,g1)
    c: Coincident(g10,g0)
    c: Coincident(g10,g6)
    c: Coincident(g11,g0)
    c: Coincident(g11,g6)
    c: Coincident(g12,g7)
    c: Coincident(g13,g2)
    c: Coincident(g13,g5)
    c: Coincident(g14,g2)
    c: Coincident(g14,g5)
    c: Coincident(g3,g12)
    c: Coincident(g9,g4)
    c: Coincident(g3,g15)
    c: Coincident(g15,g7)
    c: Coincident(g3,g0)
    c: Coincident(g7,g0)
    c: Equal(g7,g6)
    c: Equal(g7,g4)
    c: Equal(g7,g5)
    c: Diameter(g7) = 170
    c: DistanceX(g0) = 0
    c: Equal(g3,g0)
    c: Equal(g3,g2)
    c: Equal(g3,g1)
    c: Diameter(g3) = 185
    c: DistanceY(g0,g4) = 45
    c: DistanceX(g4,g0) = 45
    c: DistanceX(g4,g6) = 0
    c: DistanceX(g6,g4) = 0
    c: DistanceY(g5,g4) = 0
    c: DistanceY(g5,g4) = 0
    c: DistanceX(g7,g5) = 0
    c: DistanceY(g6,g7) = 0
    c: DistanceY(g5,g2) = 2.5
    c: DistanceX(g5,g2) = 2.5
    c: DistanceY(g1,g2) = 0
    c: DistanceY(g2,g1) = 0
    c: DistanceX(g1,g0) = 0
    c: DistanceX(g0,g1) = 0
    c: DistanceX(g2,g3) = 0
    c: DistanceY(g3,g0) = 0
FEATURE [Part::Extrusion] Extrude014
  Base = -> Sketch032
  Dir = (0,0,1)
  DirMode = 2
  FaceMakerClass = Part::FaceMakerBullseye
  LengthFwd = 20
  LengthRev = 0
  Solid = true
  Symmetric = false
FEATURE [Part::MultiFuse] Fusion070  label="level02"
  Shapes = -> [Fusion063,Extrude014]
FEATURE [Part::Cylinder] Cylinder123
  Angle = 360
  AttacherType = Attacher::AttachEngine3D
  FirstAngle = 0
  Height = 300
  Placement = pos=(0,0,90) rot=(1,0,0;1.5708rad)
  Radius = 2.8
  SecondAngle = 0
FEATURE [Part::Cylinder] Cylinder124
  Angle = 360
  AttacherType = Attacher::AttachEngine3D
  FirstAngle = 0
  Height = 300
  Placement = pos=(-150,-150,90) rot=(0.57735,0.57735,0.57735;2.0944rad)
  Radius = 2.8
  SecondAngle = 0
FEATURE [Part::MultiFuse] Fusion071  label="m4Cuts003"
  Placement = pos=(0,0,-82) rot=(0,0,1;0rad)
  Shapes = -> [Cylinder124,Cylinder123]
FEATURE [Part::Cylinder] Cylinder125
  Angle = 360
  AttacherType = Attacher::AttachEngine3D
  FirstAngle = 0
  Height = 300
  Placement = pos=(106.066,-43.934,90) rot=(0.862856,-0.357407,-0.357407;1.71777rad)
  Radius = 2.8
  SecondAngle = 0
FEATURE [Part::Cylinder] Cylinder126
  Angle = 360
  AttacherType = Attacher::AttachEngine3D
  FirstAngle = 0
  Height = 300
  Placement = pos=(-106.066,-43.934,90) rot=(0.862856,0.357407,0.357407;1.71777rad)
  Radius = 2.8
  SecondAngle = 0
FEATURE [Part::MultiFuse] Fusion072  label="m4Cuts004"
  Placement = pos=(0,0,-82) rot=(0,0,1;0rad)
  Shapes = -> [Cylinder125,Cylinder126]
FEATURE [Part::MultiFuse] Fusion073  label="m4Cuts005"
  Shapes = -> [Fusion071,Fusion072]
FEATURE [Part::Cylinder] Cylinder127
  Angle = 360
  AttacherType = Attacher::AttachEngine3D
  FirstAngle = 0
  Height = 300
  Placement = pos=(0,0,90) rot=(1,0,0;1.5708rad)
  Radius = 2.8
  SecondAngle = 0
FEATURE [Part::Cylinder] Cylinder128
  Angle = 360
  AttacherType = Attacher::AttachEngine3D
  FirstAngle = 0
  Height = 300
  Placement = pos=(-150,-150,90) rot=(0.57735,0.57735,0.57735;2.0944rad)
  Radius = 2.8
  SecondAngle = 0
FEATURE [Part::Cylinder] Cylinder129
  Angle = 360
  AttacherType = Attacher::AttachEngine3D
  FirstAngle = 0
  Height = 300
  Placement = pos=(106.066,-43.934,90) rot=(0.862856,-0.357407,-0.357407;1.71777rad)
  Radius = 2.8
  SecondAngle = 0
FEATURE [Part::Cylinder] Cylinder130
  Angle = 360
  AttacherType = Attacher::AttachEngine3D
  FirstAngle = 0
  Height = 300
  Placement = pos=(-106.066,-43.934,90) rot=(0.862856,0.357407,0.357407;1.71777rad)
  Radius = 2.8
  SecondAngle = 0
FEATURE [Part::MultiFuse] Fusion074  label="m4Cuts006"
  Placement = pos=(0,0,-82) rot=(0,0,1;0rad)
  Shapes = -> [Cylinder128,Cylinder127]
FEATURE [Part::MultiFuse] Fusion075  label="m4Cuts007"
  Placement = pos=(0,0,-82) rot=(0,0,1;0rad)
  Shapes = -> [Cylinder129,Cylinder130]
FEATURE [Part::MultiFuse] Fusion076  label="m4Cuts008"
  Shapes = -> [Fusion074,Fusion075]
FEATURE [Part::Cut] Cut033  label="srs002"
  Base = -> Cut031
  Tool = -> Fusion073
FEATURE [Part::Cut] Cut034  label="level002s"
  Base = -> Fusion070
  Tool = -> Fusion076
FEATURE [Part::Feature] Part__Feature197  label="CUI_VGS-75C-15"
  Placement = pos=(-32,-169,-130) rot=(0.57735,-0.57735,-0.57735;4.18879rad)
  shape: bbox 30.06 x 99.03 x 97.03 mm, 2447 faces, 17 solids (baked)
FEATURE [Part::Feature] Part__Feature198  label="F9 body"
  Placement = pos=(-78.1983,5.70939,50.7544) rot=(0,0,1;0rad)
  shape: bbox 118.8 x 26.53 x 118.8 mm, 173 faces (baked)
FEATURE [Part::Feature] Part__Feature199  label="F9 fan"
  Placement = pos=(-74.2115,10.4094,-44.9134) rot=(0,-1,0;1.65409rad)
  shape: bbox 98.04 x 20 x 97.21 mm, 60 faces (baked)
FEATURE [App::Part] F9  label="fan"
  Group = -> [Part__Feature198,Part__Feature199]
  Origin = -> Origin
  Placement = pos=(32.25,-103,-138.5) rot=(0,0,1;0rad)
FEATURE [Sketcher::SketchObject] Sketch033  label="top012"
  FullyConstrained = true
  sketch-geometry (6):
    g0: Circle CenterX=0 CenterY=-150 CenterZ=0 NormalX=0 NormalY=0 NormalZ=1 AngleXU=0 Radius=93
    g1: Circle CenterX=-57 CenterY=-150 CenterZ=0 NormalX=0 NormalY=0 NormalZ=1 AngleXU=0 Radius=21
    g2: Circle CenterX=-41.75 CenterY=-126 CenterZ=0 NormalX=0 NormalY=0 NormalZ=1 AngleXU=0 Radius=2
    g3: Circle CenterX=-30.75 CenterY=-129.1 CenterZ=0 NormalX=0 NormalY=0 NormalZ=1 AngleXU=0 Radius=1.625
    g4: Circle CenterX=-30.75 CenterY=-203.5 CenterZ=0 NormalX=0 NormalY=0 NormalZ=1 AngleXU=0 Radius=1.625
    g5: Circle CenterX=57 CenterY=-150 CenterZ=0 NormalX=0 NormalY=0 NormalZ=1 AngleXU=0 Radius=21
  constraints (18):
    c: PointOnObject(g0,g-2)
    c: Radius(g0) = 93
    c: DistanceY(g0) = -150
    c: Radius(g1) = 21
    c: DistanceX(g0,g1) = -57
    c: DistanceY(g1,g0) = 0
    c: DistanceY(g1,g5) = 0
    c: DistanceX(g0,g5) = 57
    c: Radius(g5) = 21
    c: DistanceY(g4,g0) = 53.5
    c: Equal(g3,g4)
    c: Radius(g3) = 1.625
    c: DistanceX(g2,g4) = 11
    c: DistanceY(g4,g2) = 77.5
    c: Radius(g2) = 2
    c: DistanceX(g4,g0) = 30.75
    c: DistanceX(g4,g3) = 0
    c: DistanceY(g4,g3) = 74.4
FEATURE [Sketcher::SketchObject] Sketch034
  FullyConstrained = true
  Placement = pos=(0,0,0) rot=(1,0,0;1.5708rad)
  sketch-geometry (12):
    g0: LineSegment StartX=-51 StartY=-85 StartZ=0 EndX=-31 EndY=-85 EndZ=0
    g1: LineSegment StartX=-31 StartY=-85 StartZ=0 EndX=-31 EndY=-180 EndZ=0
    g2: LineSegment StartX=-31 StartY=-180 StartZ=0 EndX=-51 EndY=-180 EndZ=0
    g3: LineSegment StartX=-51 StartY=-180 StartZ=0 EndX=-51 EndY=-85 EndZ=0
    g4: LineSegment StartX=31 StartY=-180 StartZ=0 EndX=51 EndY=-180 EndZ=0
    g5: LineSegment StartX=51 StartY=-180 StartZ=0 EndX=51 EndY=-85 EndZ=0
    g6: LineSegment StartX=51 StartY=-85 StartZ=0 EndX=31 EndY=-85 EndZ=0
    g7: LineSegment StartX=31 StartY=-85 StartZ=0 EndX=31 EndY=-180 EndZ=0
    g8: Circle CenterX=-41 CenterY=-92.75 CenterZ=0 NormalX=0 NormalY=0 NormalZ=1 AngleXU=0 Radius=2.8
    g9: Circle CenterX=41 CenterY=-92.75 CenterZ=0 NormalX=0 NormalY=0 NormalZ=1 AngleXU=0 Radius=2.8
    g10: Circle CenterX=41 CenterY=-174.75 CenterZ=0 NormalX=0 NormalY=0 NormalZ=1 AngleXU=0 Radius=2.8
    g11: Circle CenterX=-41 CenterY=-174.75 CenterZ=0 NormalX=0 NormalY=0 NormalZ=1 AngleXU=0 Radius=2.8
  constraints (36):
    c: Coincident(g0,g1)
    c: Coincident(g1,g2)
    c: Coincident(g2,g3)
    c: Coincident(g3,g0)
    c: Horizontal(g0)
    c: Horizontal(g2)
    c: Vertical(g1)
    c: Vertical(g3)
    c: DistanceX(g2,g1) = 20
    c: DistanceY(g2) = -180
    c: DistanceX(g1) = -31
    c: DistanceY(g2,g0) = 95
    c: Coincident(g4,g5)
    c: Coincident(g5,g6)
    c: Coincident(g6,g7)
    c: Coincident(g7,g4)
    c: Horizontal(g4)
    c: Horizontal(g6)
    c: Vertical(g5)
    c: Vertical(g7)
    c: DistanceY(g4,g1) = 0
    c: DistanceX(g4) = 31
    c: DistanceX(g4,g4) = 20
    c: DistanceY(g6,g0) = 0
    c: Equal(g9,g8)
    c: Equal(g9,g11)
    c: Equal(g9,g10)
    c: Radius(g9) = 2.8
    c: DistanceY(g11) = -174.75
    c: DistanceY(g10,g11) = 0
    c: DistanceX(g11) = -41
    c: DistanceX(g10) = 41
    c: DistanceX(g8,g11) = 0
    c: DistanceX(g9,g10) = 0
    c: DistanceY(g11,g8) = 82
    c: DistanceY(g9,g8) = 0
FEATURE [Part::Extrusion] Extrude015  label="level4"
  Base = -> Sketch033
  Dir = (0,0,1)
  DirMode = 2
  FaceMakerClass = Part::FaceMakerBullseye
  LengthFwd = 5
  LengthRev = 0
  Placement = pos=(0,0,-185) rot=(0,0,1;0rad)
  Solid = true
  Symmetric = false
FEATURE [Part::Extrusion] Extrude016  label="fanHolder"
  Base = -> Sketch034
  Dir = (0,-1,-3e-16)
  DirMode = 2
  FaceMakerClass = Part::FaceMakerBullseye
  LengthFwd = 10
  LengthRev = 0
  Placement = pos=(0,-98,0) rot=(0,0,1;0rad)
  Solid = true
  Symmetric = false
FEATURE [Sketcher::SketchObject] Sketch035
  FullyConstrained = true
  Placement = pos=(0,0,0) rot=(0.57735,0.57735,0.57735;2.0944rad)
  sketch-geometry (15):
    g0: LineSegment StartX=-222 StartY=-80 StartZ=0 EndX=-210 EndY=-80 EndZ=0
    g1: LineSegment StartX=-108 StartY=-180 StartZ=0 EndX=-222 EndY=-180 EndZ=0
    g2: LineSegment StartX=-222 StartY=-180 StartZ=0 EndX=-222 EndY=-80 EndZ=0
    g3: LineSegment StartX=-120 StartY=-80 StartZ=0 EndX=-108 EndY=-80 EndZ=0
    g4: LineSegment StartX=-108 StartY=-80 StartZ=0 EndX=-108 EndY=-180 EndZ=0
    g5: Circle CenterX=-216 CenterY=-94.75 CenterZ=0 NormalX=0 NormalY=0 NormalZ=1 AngleXU=0 Radius=2
    g6: Circle CenterX=-113.8 CenterY=-87.8 CenterZ=0 NormalX=0 NormalY=0 NormalZ=1 AngleXU=0 Radius=2
    g7: Circle CenterX=-113.8 CenterY=-176.2 CenterZ=0 NormalX=0 NormalY=0 NormalZ=1 AngleXU=0 Radius=2
    g8: Circle CenterX=-216 CenterY=-176.2 CenterZ=0 NormalX=0 NormalY=0 NormalZ=1 AngleXU=0 Radius=2
    g9: LineSegment StartX=-210 StartY=-80 StartZ=0 EndX=-210 EndY=-120 EndZ=0
    g10: LineSegment StartX=-210 StartY=-120 StartZ=0 EndX=-120 EndY=-120 EndZ=0
    g11: LineSegment StartX=-120 StartY=-120 StartZ=0 EndX=-120 EndY=-80 EndZ=0
    g12: Circle CenterX=-155.2 CenterY=-125.25 CenterZ=0 NormalX=0 NormalY=0 NormalZ=1 AngleXU=0 Radius=1.625
    g13: Circle CenterX=-140 CenterY=-134.25 CenterZ=0 NormalX=0 NormalY=0 NormalZ=1 AngleXU=0 Radius=1.625
    g14: Circle CenterX=-195 CenterY=-134.25 CenterZ=0 NormalX=0 NormalY=0 NormalZ=1 AngleXU=0 Radius=1.625
  constraints (45):
    c: Coincident(g1,g2)
    c: Coincident(g2,g0)
    c: Horizontal(g0)
    c: Horizontal(g1)
    c: Vertical(g2)
    c: Coincident(g3,g4)
    c: Horizontal(g3)
    c: Vertical(g4)
    c: DistanceY(g1) = -180
    c: DistanceY(g1,g0) = 100
    c: Coincident(g9,g0)
    c: Vertical(g9)
    c: Coincident(g10,g9)
    c: Horizontal(g10)
    c: Coincident(g11,g10)
    c: Coincident(g11,g3)
    c: DistanceX(g1) = -222
    c: DistanceX(g1,g4) = 114
    c: DistanceY(g1,g8) = 3.8
    c: DistanceY(g7,g8) = 0
    c: Vertical(g11)
    c: DistanceX(g0,g0) = 12
    c: DistanceX(g3,g3) = 12
    c: DistanceY(g0,g3) = 0
    c: DistanceY(g4,g10) = 60
    c: DistanceY(g1,g14) = 45.75
    c: DistanceY(g13,g14) = 0
    c: DistanceX(g14,g13) = 55
    c: DistanceY(g13,g12) = 9
    c: DistanceX(g12,g13) = 15.2
    c: Equal(g13,g12)
    c: Equal(g13,g14)
    c: Radius(g13) = 1.625
    c: DistanceX(g13) = -140
    c: Equal(g6,g7)
    c: Equal(g6,g8)
    c: Equal(g6,g5)
    c: Radius(g6) = 2
    c: DistanceX(g1,g8) = 6
    c: DistanceX(g8,g7) = 102.2
    c: DistanceX(g6,g7) = 0
    c: DistanceX(g5,g8) = 0
    c: DistanceY(g8,g5) = 81.45
    c: DistanceY(g7,g6) = 88.4
    c: Coincident(g1,g4)
FEATURE [Part::Extrusion] Extrude017  label="powerSBCHolder"
  Base = -> Sketch035
  Dir = (1,0,0)
  DirMode = 2
  FaceMakerClass = Part::FaceMakerBullseye
  LengthFwd = 10
  LengthRev = 0
  Placement = pos=(-15,0,0) rot=(0,0,1;0rad)
  Solid = true
  Symmetric = false
FEATURE [Part::MultiFuse] Fusion077  label="level004"
  Shapes = -> [Extrude015,Extrude016,Extrude017]
FEATURE [Part::Feature] Part__Feature028  label="DCP-RJ6ST-F"
  Placement = pos=(57,-150,-250) rot=(0,1,0;3.14159rad)
  shape: bbox 40.26 x 40.33 x 38.85 mm, 485 faces, 2 solids (baked)
FEATURE [Part::Feature] Part__Feature027  label="DCC-RJ6ST-310"
  Placement = pos=(57,-150,-259) rot=(0,0,1;0rad)
  shape: bbox 40.36 x 68.07 x 51.72 mm, 441 faces (baked)
FEATURE [Part::Feature] Part__Feature022  label="3136N138_T-Slotted Framing"
  Placement = pos=(0,200.3,0) rot=(0,0,1;0rad)
  shape: bbox 101.6 x 133.4 x 139.7 mm, 136 faces (baked)
FEATURE [Part::Feature] Part__Feature023  label="47065T801_T-Slotted Framing"
  Placement = pos=(0,300.5,0) rot=(-1,0,0;1.5708rad)
  shape: bbox 25.4 x 152.4 x 25.4 mm, 108 faces (baked)
FEATURE [Part::Feature] Part__Feature024  label="47065T801_T-Slotted Framing001"
  Placement = pos=(0,450,0) rot=(-1,0,0;1.5708rad)
  shape: bbox 25.4 x 152.4 x 25.4 mm, 108 faces (baked)
FEATURE [Part::MultiFuse] Fusion079  label="framingSupport"
  Placement = pos=(0,350,-263) rot=(0,0,1;3.14159rad)
  Shapes = -> [Part__Feature024,Part__Feature022,Part__Feature023]
FEATURE [Sketcher::SketchObject] Sketch037  label="top013"
  FullyConstrained = true
  sketch-geometry (9):
    g0: Circle CenterX=0 CenterY=-150 CenterZ=0 NormalX=0 NormalY=0 NormalZ=1 AngleXU=0 Radius=93
    g1: Circle CenterX=-57 CenterY=-150 CenterZ=0 NormalX=0 NormalY=0 NormalZ=1 AngleXU=0 Radius=11
    g2: Circle CenterX=57 CenterY=-150 CenterZ=0 NormalX=0 NormalY=0 NormalZ=1 AngleXU=0 Radius=15.1
    g3: Circle CenterX=35 CenterY=-200 CenterZ=0 NormalX=0 NormalY=0 NormalZ=1 AngleXU=0 Radius=15.1
    g4: Circle CenterX=-35 CenterY=-200 CenterZ=0 NormalX=0 NormalY=0 NormalZ=1 AngleXU=0 Radius=6.4
    g5: ArcOfCircle CenterX=0 CenterY=-220 CenterZ=0 NormalX=0 NormalY=0 NormalZ=1 AngleXU=0 Radius=5 StartAngle=2.26529 EndAngle=7.15948
    g6: ArcOfCircle CenterX=0 CenterY=-212.5 CenterZ=0 NormalX=0 NormalY=0 NormalZ=1 AngleXU=0 Radius=3.2 StartAngle=3e-15 EndAngle=3.14159
    g7: LineSegment StartX=-3.2 StartY=-212.5 StartZ=0 EndX=-3.2 EndY=-216.158 EndZ=0
    g8: LineSegment StartX=3.2 StartY=-216.158 StartZ=0 EndX=3.2 EndY=-212.5 EndZ=0
  constraints (29):
    c: PointOnObject(g0,g-2)
    c: Radius(g0) = 93
    c: DistanceY(g0) = -150
    c: Radius(g1) = 11
    c: DistanceX(g0,g1) = -57
    c: DistanceY(g1,g0) = 0
    c: DistanceY(g1,g2) = 0
    c: DistanceX(g0,g2) = 57
    c: DistanceX(g3) = 35
    c: DistanceY(g3,g0) = 50
    c: DistanceY(g3,g4) = 0
    c: DistanceX(g4,g0) = 35
    c: Radius(g4) = 6.4
    c: Equal(g2,g3)
    c: Radius(g2) = 15.1
    c: PointOnObject(g5,g-2)
    c: PointOnObject(g6,g-2)
    c: DistanceY(g5,g0) = 70
    c: DistanceX(g5,g6) = 0
    c: DistanceX(g6,g5) = 0
    c: Coincident(g7,g6)
    c: Coincident(g7,g5)
    c: Coincident(g8,g5)
    c: Coincident(g8,g6)
    c: DistanceX(g5,g5) = 6.4
    c: DistanceY(g5,g6) = 7.5
    c: DistanceY(g6,g6) = 0
    c: DistanceY(g6,g6) = 0
    c: Radius(g5) = 5
FEATURE [Part::Extrusion] Extrude019  label="level005"
  Base = -> Sketch037
  Dir = (0,0,1)
  DirMode = 2
  FaceMakerClass = Part::FaceMakerBullseye
  LengthFwd = 8
  LengthRev = 0
  Placement = pos=(0,0,-250) rot=(0,0,1;0rad)
  Solid = true
  Symmetric = false
FEATURE [Part::Feature] Feature001  label="PG7"
  Placement = pos=(-35,-200,-248) rot=(0,0,1;0rad)
  shape: bbox 21.32 x 20.97 x 29.79 mm, 246 faces, 3 solids (baked)
FEATURE [Part::Feature] Shell029
  shape: bbox 36.98 x 21.68 x 36.68 mm, 152 faces, 0 solids (baked)
FEATURE [Part::Feature] Shell030
  shape: bbox 22.66 x 11.43 x 22.66 mm, 6 faces, 0 solids (baked)
FEATURE [Part::Feature] Shell031
  shape: bbox 0.3612 x 0.889 x 0.6255 mm, 1 faces, 0 solids (baked)
FEATURE [Part::Feature] Shell032
  shape: bbox 35.58 x 29.16 x 35.58 mm, 49 faces, 0 solids (baked)
FEATURE [Part::Feature] Shell033
  shape: bbox 24.46 x 14.2 x 24.46 mm, 102 faces, 0 solids (baked)
FEATURE [Part::Feature] Shell034
  shape: bbox 0.3892 x 1.194 x 0.6742 mm, 1 faces, 0 solids (baked)
FEATURE [Part::Feature] Shell035
  shape: bbox 0.2703 x 0.381 x 0.4682 mm, 1 faces, 0 solids (baked)
FEATURE [Part::Feature] Shell036
  shape: bbox 0.2577 x 0.3048 x 0.4459 mm, 1 faces, 0 solids (baked)
FEATURE [Part::Feature] Shell037
  shape: bbox 36.98 x 18.12 x 36.6 mm, 205 faces, 0 solids (baked)
FEATURE [Part::Compound2] Compound003  label="M3222GBH_SW0002"
  Links = -> [Shell037,Shell029,Shell030,Shell033,Shell032,Shell036,Shell034,Shell031,Shell035]
  Placement = pos=(35,-200,-250) rot=(1,0,0;4.71239rad)
FEATURE [Part::Feature] Part__Feature200  label="powerInsert"
  Placement = pos=(-57,-150,-267) rot=(1,0,0;1.5708rad)
  shape: bbox 29.63 x 29.64 x 35.77 mm, 59 faces (baked)
FEATURE [Sketcher::SketchObject] Sketch038
  FullyConstrained = true
  sketch-geometry (4):
    g0: ArcOfCircle CenterX=0 CenterY=-220 CenterZ=0 NormalX=0 NormalY=0 NormalZ=1 AngleXU=0 Radius=5 StartAngle=3.14159 EndAngle=6.28319
    g1: ArcOfCircle CenterX=-1.2e-15 CenterY=-212.5 CenterZ=0 NormalX=0 NormalY=0 NormalZ=1 AngleXU=0 Radius=5 StartAngle=1.419e-13 EndAngle=3.14159
    g2: LineSegment StartX=5 StartY=-220 StartZ=0 EndX=5 EndY=-212.5 EndZ=0
    g3: LineSegment StartX=-5 StartY=-212.5 StartZ=0 EndX=-5 EndY=-220 EndZ=0
  constraints (10):
    c: Tangent(g0,g2) = -1.5708
    c: Tangent(g2,g1) = -1.5708
    c: Tangent(g1,g3) = -1.5708
    c: Tangent(g3,g0) = -1.5708
    c: Equal(g0,g1)
    c: Vertical(g2)
    c: DistanceX(g0) = 0
    c: DistanceY(g0) = -220
    c: Radius(g0) = 5
    c: DistanceY(g0,g1) = 7.5
FEATURE [Part::Extrusion] Extrude020  label="micCutLevel5"
  Base = -> Sketch038
  Dir = (0,0,1)
  DirMode = 2
  FaceMakerClass = Part::FaceMakerBullseye
  LengthFwd = 10
  LengthRev = 0
  Placement = pos=(0,0,-246.5) rot=(0,0,1;0rad)
  Solid = true
  Symmetric = false
FEATURE [Sketcher::SketchObject] Sketch039
  FullyConstrained = true
  sketch-geometry (16):
    g0: ArcOfCircle CenterX=0 CenterY=-150 CenterZ=0 NormalX=0 NormalY=0 NormalZ=1 AngleXU=0 Radius=93 StartAngle=2.86943 EndAngle=3.41376
    g1: ArcOfCircle CenterX=0 CenterY=-150 CenterZ=0 NormalX=0 NormalY=0 NormalZ=1 AngleXU=0 Radius=93 StartAngle=1.29863 EndAngle=1.84296
    g2: ArcOfCircle CenterX=0 CenterY=-150 CenterZ=0 NormalX=0 NormalY=0 NormalZ=1 AngleXU=0 Radius=93 StartAngle=6.01102 EndAngle=6.55535
    g3: ArcOfCircle CenterX=0 CenterY=-150 CenterZ=0 NormalX=0 NormalY=0 NormalZ=1 AngleXU=0 Radius=93 StartAngle=4.44022 EndAngle=4.98455
    g4: ArcOfCircle CenterX=0 CenterY=-150 CenterZ=0 NormalX=0 NormalY=0 NormalZ=1 AngleXU=0 Radius=86 StartAngle=1.27584 EndAngle=1.86575
    g5: ArcOfCircle CenterX=0 CenterY=-150 CenterZ=0 NormalX=0 NormalY=0 NormalZ=1 AngleXU=0 Radius=86 StartAngle=5.98823 EndAngle=6.57814
    g6: ArcOfCircle CenterX=0 CenterY=-150 CenterZ=0 NormalX=0 NormalY=0 NormalZ=1 AngleXU=0 Radius=86 StartAngle=2.84664 EndAngle=3.43655
    g7: ArcOfCircle CenterX=0 CenterY=-150 CenterZ=0 NormalX=0 NormalY=0 NormalZ=1 AngleXU=0 Radius=86 StartAngle=4.41743 EndAngle=5.00734
    g8: LineSegment StartX=25 StartY=-60.4232 StartZ=0 EndX=25 EndY=-67.7139 EndZ=0
    g9: LineSegment StartX=-25 StartY=-60.4232 StartZ=0 EndX=-25 EndY=-67.7139 EndZ=0
    g10: LineSegment StartX=-89.5768 StartY=-125 StartZ=0 EndX=-82.2861 EndY=-125 EndZ=0
    g11: LineSegment StartX=-89.5768 StartY=-175 StartZ=0 EndX=-82.2861 EndY=-175 EndZ=0
    g12: LineSegment StartX=-25 StartY=-239.577 StartZ=0 EndX=-25 EndY=-232.286 EndZ=0
    g13: LineSegment StartX=25 StartY=-239.577 StartZ=0 EndX=25 EndY=-232.286 EndZ=0
    g14: LineSegment StartX=89.5768 StartY=-175 StartZ=0 EndX=82.2861 EndY=-175 EndZ=0
    g15: LineSegment StartX=89.5768 StartY=-125 StartZ=0 EndX=82.2861 EndY=-125 EndZ=0
  constraints (49):
    c: PointOnObject(g0,g-2)
    c: Coincident(g1,g0)
    c: Coincident(g2,g0)
    c: Coincident(g3,g0)
    c: DistanceY(g0) = -150
    c: Coincident(g4,g0)
    c: Coincident(g5,g0)
    c: Coincident(g6,g0)
    c: Coincident(g7,g0)
    c: DistanceX(g4,g0) = 25
    c: DistanceX(g1,g4) = 0
    c: DistanceX(g0,g4) = 25
    c: DistanceX(g4,g1) = 0
    c: DistanceY(g0,g5) = 25
    c: DistanceY(g5,g2) = 0
    c: DistanceY(g2,g0) = 25
    c: DistanceY(g2,g5) = 0
    c: DistanceY(g6,g0) = 25
    c: DistanceY(g0,g6) = 0
    c: DistanceY(g0,g6) = 25
    c: DistanceY(g6,g0) = 0
    c: Equal(g1,g2)
    c: Equal(g1,g3)
    c: Equal(g1,g0)
    c: Radius(g1) = 93
    c: Equal(g6,g4)
    c: Equal(g6,g5)
    c: Equal(g6,g7)
    c: Radius(g6) = 86
    c: DistanceX(g0,g7) = 25
    c: DistanceX(g7,g3) = 0
    c: DistanceX(g3) = -25
    c: DistanceX(g3,g7) = 0
    c: Coincident(g8,g1)
    c: Coincident(g8,g4)
    c: Coincident(g9,g1)
    c: Coincident(g9,g4)
    c: Coincident(g10,g0)
    c: Coincident(g10,g6)
    c: Coincident(g11,g0)
    c: Coincident(g11,g6)
    c: Coincident(g12,g3)
    c: Coincident(g12,g7)
    c: Coincident(g13,g3)
    c: Coincident(g13,g7)
    c: Coincident(g14,g2)
    c: Coincident(g14,g5)
    c: Coincident(g15,g2)
    c: Coincident(g15,g5)
FEATURE [Part::Extrusion] Extrude021  label="srsHolds002"
  Base = -> Sketch039
  Dir = (0,0,1)
  DirMode = 2
  FaceMakerClass = Part::FaceMakerBullseye
  LengthFwd = 30
  LengthRev = 0
  Placement = pos=(0,0,-185) rot=(0,0,1;0rad)
  Solid = true
  Symmetric = false
FEATURE [Part::FeaturePython] Tube003  # WARN: FeaturePython — macro-defined, semantics opaque (R4)
  AttacherType = Attacher::AttachEngine3D
  Height = 125
  InnerRadius = 94
  OuterRadius = 98
  Placement = pos=(0,-150,-185) rot=(0,0,1;0rad)
FEATURE [Sketcher::SketchObject] Sketch040  label="top014"
  FullyConstrained = true
  sketch-geometry (2):
    g0: Circle CenterX=0 CenterY=-150 CenterZ=0 NormalX=0 NormalY=0 NormalZ=1 AngleXU=0 Radius=98
    g1: Circle CenterX=0 CenterY=-150 CenterZ=0 NormalX=0 NormalY=0 NormalZ=1 AngleXU=0 Radius=78
  constraints (5):
    c: PointOnObject(g0,g-2)
    c: Diameter(g0) = 196
    c: DistanceY(g0) = -150
    c: Coincident(g1,g0)
    c: Radius(g1) = 78
FEATURE [Part::Extrusion] Extrude022  label="TupeConnectLevel3"
  Base = -> Sketch040
  Dir = (0,0,1)
  DirMode = 2
  FaceMakerClass = Part::FaceMakerBullseye
  LengthFwd = 5
  LengthRev = 0
  Placement = pos=(0,0,-65) rot=(0,0,1;0rad)
  Solid = true
  Symmetric = false
FEATURE [Part::MultiFuse] Fusion080  label="tube4to3"
  Shapes = -> [Extrude022,Tube003]
FEATURE [Part::MultiFuse] Fusion081  label="level04"
  Shapes = -> [Fusion077,Extrude021]
FEATURE [Sketcher::SketchObject] Sketch041
  FullyConstrained = true
  sketch-geometry (16):
    g0: ArcOfCircle CenterX=0 CenterY=-150 CenterZ=0 NormalX=0 NormalY=0 NormalZ=1 AngleXU=0 Radius=93 StartAngle=2.86943 EndAngle=3.41376
    g1: ArcOfCircle CenterX=0 CenterY=-150 CenterZ=0 NormalX=0 NormalY=0 NormalZ=1 AngleXU=0 Radius=93 StartAngle=1.29863 EndAngle=1.84296
    g2: ArcOfCircle CenterX=0 CenterY=-150 CenterZ=0 NormalX=0 NormalY=0 NormalZ=1 AngleXU=0 Radius=93 StartAngle=6.01102 EndAngle=6.55535
    g3: ArcOfCircle CenterX=0 CenterY=-150 CenterZ=0 NormalX=0 NormalY=0 NormalZ=1 AngleXU=0 Radius=93 StartAngle=4.44022 EndAngle=4.98455
    g4: ArcOfCircle CenterX=0 CenterY=-150 CenterZ=0 NormalX=0 NormalY=0 NormalZ=1 AngleXU=0 Radius=86 StartAngle=1.27584 EndAngle=1.86575
    g5: ArcOfCircle CenterX=0 CenterY=-150 CenterZ=0 NormalX=0 NormalY=0 NormalZ=1 AngleXU=0 Radius=86 StartAngle=5.98823 EndAngle=6.57814
    g6: ArcOfCircle CenterX=0 CenterY=-150 CenterZ=0 NormalX=0 NormalY=0 NormalZ=1 AngleXU=0 Radius=86 StartAngle=2.84664 EndAngle=3.43655
    g7: ArcOfCircle CenterX=0 CenterY=-150 CenterZ=0 NormalX=0 NormalY=0 NormalZ=1 AngleXU=0 Radius=86 StartAngle=4.41743 EndAngle=5.00734
    g8: LineSegment StartX=25 StartY=-60.4232 StartZ=0 EndX=25 EndY=-67.7139 EndZ=0
    g9: LineSegment StartX=-25 StartY=-60.4232 StartZ=0 EndX=-25 EndY=-67.7139 EndZ=0
    g10: LineSegment StartX=-89.5768 StartY=-125 StartZ=0 EndX=-82.2861 EndY=-125 EndZ=0
    g11: LineSegment StartX=-89.5768 StartY=-175 StartZ=0 EndX=-82.2861 EndY=-175 EndZ=0
    g12: LineSegment StartX=-25 StartY=-239.577 StartZ=0 EndX=-25 EndY=-232.286 EndZ=0
    g13: LineSegment StartX=25 StartY=-239.577 StartZ=0 EndX=25 EndY=-232.286 EndZ=0
    g14: LineSegment StartX=89.5768 StartY=-175 StartZ=0 EndX=82.2861 EndY=-175 EndZ=0
    g15: LineSegment StartX=89.5768 StartY=-125 StartZ=0 EndX=82.2861 EndY=-125 EndZ=0
  constraints (49):
    c: PointOnObject(g0,g-2)
    c: Coincident(g1,g0)
    c: Coincident(g2,g0)
    c: Coincident(g3,g0)
    c: DistanceY(g0) = -150
    c: Coincident(g4,g0)
    c: Coincident(g5,g0)
    c: Coincident(g6,g0)
    c: Coincident(g7,g0)
    c: DistanceX(g4,g0) = 25
    c: DistanceX(g1,g4) = 0
    c: DistanceX(g0,g4) = 25
    c: DistanceX(g4,g1) = 0
    c: DistanceY(g0,g5) = 25
    c: DistanceY(g5,g2) = 0
    c: DistanceY(g2,g0) = 25
    c: DistanceY(g2,g5) = 0
    c: DistanceY(g6,g0) = 25
    c: DistanceY(g0,g6) = 0
    c: DistanceY(g0,g6) = 25
    c: DistanceY(g6,g0) = 0
    c: Equal(g1,g2)
    c: Equal(g1,g3)
    c: Equal(g1,g0)
    c: Radius(g1) = 93
    c: Equal(g6,g4)
    c: Equal(g6,g5)
    c: Equal(g6,g7)
    c: Radius(g6) = 86
    c: DistanceX(g0,g7) = 25
    c: DistanceX(g7,g3) = 0
    c: DistanceX(g3) = -25
    c: DistanceX(g3,g7) = 0
    c: Coincident(g8,g1)
    c: Coincident(g8,g4)
    c: Coincident(g9,g1)
    c: Coincident(g9,g4)
    c: Coincident(g10,g0)
    c: Coincident(g10,g6)
    c: Coincident(g11,g0)
    c: Coincident(g11,g6)
    c: Coincident(g12,g3)
    c: Coincident(g12,g7)
    c: Coincident(g13,g3)
    c: Coincident(g13,g7)
    c: Coincident(g14,g2)
    c: Coincident(g14,g5)
    c: Coincident(g15,g2)
    c: Coincident(g15,g5)
FEATURE [Part::Extrusion] Extrude023  label="srsHoldsLevel5"
  Base = -> Sketch041
  Dir = (0,0,1)
  DirMode = 2
  FaceMakerClass = Part::FaceMakerBullseye
  LengthFwd = 30
  LengthRev = 0
  Placement = pos=(0,0,-250) rot=(0,0,1;0rad)
  Solid = true
  Symmetric = false
FEATURE [Sketcher::SketchObject] Sketch042  label="top015"
  FullyConstrained = true
  sketch-geometry (2):
    g0: Circle CenterX=0 CenterY=-150 CenterZ=0 NormalX=0 NormalY=0 NormalZ=1 AngleXU=0 Radius=98
    g1: Circle CenterX=0 CenterY=-150 CenterZ=0 NormalX=0 NormalY=0 NormalZ=1 AngleXU=0 Radius=76
  constraints (5):
    c: PointOnObject(g0,g-2)
    c: Diameter(g0) = 196
    c: DistanceY(g0) = -150
    c: Coincident(g1,g0)
    c: Radius(g1) = 76
FEATURE [Part::Extrusion] Extrude024  label="TupeConnectLevel004"
  Base = -> Sketch042
  Dir = (0,0,1)
  DirMode = 2
  FaceMakerClass = Part::FaceMakerBullseye
  LengthFwd = 5
  LengthRev = 0
  Placement = pos=(0,0,-65) rot=(0,0,1;0rad)
  Solid = true
  Symmetric = false
FEATURE [Part::FeaturePython] Tube004  # WARN: FeaturePython — macro-defined, semantics opaque (R4)
  AttacherType = Attacher::AttachEngine3D
  Height = 65
  InnerRadius = 94
  OuterRadius = 98
  Placement = pos=(0,-150,-125) rot=(0,0,1;0rad)
FEATURE [Part::MultiFuse] Fusion082  label="tube5to004"
  Placement = pos=(0,0,-125) rot=(0,0,1;0rad)
  Shapes = -> [Extrude024,Tube004]
FEATURE [Part::MultiFuse] Fusion083  label="level5"
  Shapes = -> [Extrude019,Extrude023]
FEATURE [Part::Cylinder] Cylinder131
  Angle = 360
  AttacherType = Attacher::AttachEngine3D
  FirstAngle = 0
  Height = 300
  Placement = pos=(0,0,90) rot=(1,0,0;1.5708rad)
  Radius = 2.13
  SecondAngle = 0
FEATURE [Part::Cylinder] Cylinder132
  Angle = 360
  AttacherType = Attacher::AttachEngine3D
  FirstAngle = 0
  Height = 300
  Placement = pos=(-150,-150,90) rot=(0.57735,0.57735,0.57735;2.0944rad)
  Radius = 2.13
  SecondAngle = 0
FEATURE [Part::MultiFuse] Fusion084  label="m4Cuts009"
  Placement = pos=(0,0,-321) rot=(0,0,1;0rad)
  Shapes = -> [Cylinder132,Cylinder131]
FEATURE [Part::Cylinder] Cylinder133
  Angle = 360
  AttacherType = Attacher::AttachEngine3D
  FirstAngle = 0
  Height = 300
  Placement = pos=(0,0,90) rot=(1,0,0;1.5708rad)
  Radius = 2.8
  SecondAngle = 0
FEATURE [Part::Cylinder] Cylinder134
  Angle = 360
  AttacherType = Attacher::AttachEngine3D
  FirstAngle = 0
  Height = 300
  Placement = pos=(-150,-150,90) rot=(0.57735,0.57735,0.57735;2.0944rad)
  Radius = 2.8
  SecondAngle = 0
FEATURE [Part::MultiFuse] Fusion085  label="m4HeatSetCuts001"
  Placement = pos=(0,0,-321) rot=(0,0,1;0rad)
  Shapes = -> [Cylinder134,Cylinder133]
FEATURE [Sketcher::SketchObject] Sketch043
  FullyConstrained = true
  sketch-geometry (4):
    g0: Circle CenterX=0 CenterY=-68 CenterZ=0 NormalX=0 NormalY=0 NormalZ=1 AngleXU=0 Radius=2.125
    g1: Circle CenterX=82 CenterY=-150 CenterZ=0 NormalX=0 NormalY=0 NormalZ=1 AngleXU=0 Radius=2.125
    g2: Circle CenterX=0 CenterY=-232 CenterZ=0 NormalX=0 NormalY=0 NormalZ=1 AngleXU=0 Radius=2.125
    g3: Circle CenterX=-82 CenterY=-150 CenterZ=0 NormalX=0 NormalY=0 NormalZ=1 AngleXU=0 Radius=2.125
  constraints (12):
    c: PointOnObject(g0,g-2)
    c: DistanceY(g1) = -150
    c: DistanceY(g1,g3) = 0
    c: DistanceX(g2) = 0
    c: DistanceX(g1) = 82
    c: Equal(g1,g0)
    c: Equal(g1,g3)
    c: Equal(g1,g2)
    c: Diameter(g1) = 4.25
    c: DistanceX(g3) = -82
    c: DistanceY(g3,g0) = 82
    c: DistanceY(g2,g3) = 82
FEATURE [Part::Extrusion] Extrude025  label="m4VerCuts"
  Base = -> Sketch043
  Dir = (0,0,1)
  DirMode = 2
  FaceMakerClass = Part::FaceMakerBullseye
  LengthFwd = 20
  LengthRev = 0
  Placement = pos=(0,0,-194.5) rot=(0,0,1;0rad)
  Solid = true
  Symmetric = false
FEATURE [Sketcher::SketchObject] Sketch044
  FullyConstrained = true
  sketch-geometry (4):
    g0: Circle CenterX=0 CenterY=-68 CenterZ=0 NormalX=0 NormalY=0 NormalZ=1 AngleXU=0 Radius=2.8
    g1: Circle CenterX=82 CenterY=-150 CenterZ=0 NormalX=0 NormalY=0 NormalZ=1 AngleXU=0 Radius=2.8
    g2: Circle CenterX=0 CenterY=-232 CenterZ=0 NormalX=0 NormalY=0 NormalZ=1 AngleXU=0 Radius=2.8
    g3: Circle CenterX=-82 CenterY=-150 CenterZ=0 NormalX=0 NormalY=0 NormalZ=1 AngleXU=0 Radius=2.8
  constraints (12):
    c: PointOnObject(g0,g-2)
    c: DistanceY(g1) = -150
    c: DistanceY(g1,g3) = 0
    c: DistanceX(g2) = 0
    c: DistanceX(g1) = 82
    c: Equal(g1,g0)
    c: Equal(g1,g3)
    c: Equal(g1,g2)
    c: Diameter(g1) = 5.6
    c: DistanceX(g3) = -82
    c: DistanceY(g3,g0) = 82
    c: DistanceY(g2,g3) = 82
FEATURE [Part::Extrusion] Extrude026  label="m4HeatSetVerCuts001"
  Base = -> Sketch044
  Dir = (0,0,1)
  DirMode = 2
  FaceMakerClass = Part::FaceMakerBullseye
  LengthFwd = 20
  LengthRev = 0
  Placement = pos=(0,0,-193) rot=(0,0,1;0rad)
  Solid = true
  Symmetric = false
FEATURE [Part::Cut] Cut035  label="level05s"
  Base = -> Fusion083
  Tool = -> Fusion085
FEATURE [Part::Cut] Cut036  label="tube4to5"
  Base = -> Fusion082
  Tool = -> Fusion084
FEATURE [Part::Cut] Cut037  label="level4s"
  Base = -> Fusion081
  Tool = -> Extrude025
FEATURE [Part::Cut] Cut038  label="tube4to5s"
  Base = -> Cut036
  Tool = -> Extrude026
FEATURE [Part::Cylinder] Cylinder135
  Angle = 360
  AttacherType = Attacher::AttachEngine3D
  FirstAngle = 0
  Height = 300
  Placement = pos=(0,0,90) rot=(1,0,0;1.5708rad)
  Radius = 2.8
  SecondAngle = 0
FEATURE [Part::Cylinder] Cylinder136
  Angle = 360
  AttacherType = Attacher::AttachEngine3D
  FirstAngle = 0
  Height = 300
  Placement = pos=(-150,-150,90) rot=(0.57735,0.57735,0.57735;2.0944rad)
  Radius = 2.8
  SecondAngle = 0
FEATURE [Part::MultiFuse] Fusion086  label="m4HeatSetCuts002"
  Placement = pos=(0,0,-257) rot=(0,0,1;0rad)
  Shapes = -> [Cylinder136,Cylinder135]
FEATURE [Part::Cut] Cut039  label="level4s001"
  Base = -> Cut037
  Tool = -> Fusion086
FEATURE [Part::Cylinder] Cylinder137
  Angle = 360
  AttacherType = Attacher::AttachEngine3D
  FirstAngle = 0
  Height = 300
  Placement = pos=(0,0,90) rot=(1,0,0;1.5708rad)
  Radius = 2.13
  SecondAngle = 0
FEATURE [Part::Cylinder] Cylinder138
  Angle = 360
  AttacherType = Attacher::AttachEngine3D
  FirstAngle = 0
  Height = 300
  Placement = pos=(-150,-150,90) rot=(0.57735,0.57735,0.57735;2.0944rad)
  Radius = 2.13
  SecondAngle = 0
FEATURE [Part::MultiFuse] Fusion087  label="m4Cuts010"
  Placement = pos=(0,0,-257) rot=(0,0,1;0rad)
  Shapes = -> [Cylinder138,Cylinder137]
FEATURE [Part::Cut] Cut040  label="level3to4Tube"
  Base = -> Fusion080
  Tool = -> Fusion087
FEATURE [Part::Cut] Cut041  label="level5s"
  Base = -> Cut035
  Tool = -> Extrude020
FEATURE [Sketcher::SketchObject] Sketch046
  FullyConstrained = true
  sketch-geometry (4):
    g0: Circle CenterX=0 CenterY=-63 CenterZ=0 NormalX=0 NormalY=0 NormalZ=1 AngleXU=0 Radius=2.8
    g1: Circle CenterX=87 CenterY=-150 CenterZ=0 NormalX=0 NormalY=0 NormalZ=1 AngleXU=0 Radius=2.8
    g2: Circle CenterX=0 CenterY=-237 CenterZ=0 NormalX=0 NormalY=0 NormalZ=1 AngleXU=0 Radius=2.8
    g3: Circle CenterX=-87 CenterY=-150 CenterZ=0 NormalX=0 NormalY=0 NormalZ=1 AngleXU=0 Radius=2.8
  constraints (12):
    c: PointOnObject(g0,g-2)
    c: DistanceY(g1) = -150
    c: DistanceY(g1,g3) = 0
    c: DistanceX(g2) = 0
    c: DistanceX(g1) = 87
    c: Equal(g1,g0)
    c: Equal(g1,g3)
    c: Equal(g1,g2)
    c: Diameter(g1) = 5.6
    c: DistanceX(g3) = -87
    c: DistanceY(g3,g0) = 87
    c: DistanceY(g2,g3) = 87
FEATURE [Part::Extrusion] Extrude028  label="m4HeatSetVerCuts003"
  Base = -> Sketch046
  Dir = (0,0,1)
  DirMode = 2
  FaceMakerClass = Part::FaceMakerBullseye
  LengthFwd = 20
  LengthRev = 0
  Placement = pos=(0,0,-69.5) rot=(0,0,1;0rad)
  Solid = true
  Symmetric = false
FEATURE [Sketcher::SketchObject] Sketch047
  FullyConstrained = true
  sketch-geometry (4):
    g0: Circle CenterX=0 CenterY=-63 CenterZ=0 NormalX=0 NormalY=0 NormalZ=1 AngleXU=0 Radius=2.125
    g1: Circle CenterX=87 CenterY=-150 CenterZ=0 NormalX=0 NormalY=0 NormalZ=1 AngleXU=0 Radius=2.125
    g2: Circle CenterX=0 CenterY=-237 CenterZ=0 NormalX=0 NormalY=0 NormalZ=1 AngleXU=0 Radius=2.125
    g3: Circle CenterX=-87 CenterY=-150 CenterZ=0 NormalX=0 NormalY=0 NormalZ=1 AngleXU=0 Radius=2.125
  constraints (12):
    c: PointOnObject(g0,g-2)
    c: DistanceY(g1) = -150
    c: DistanceY(g1,g3) = 0
    c: DistanceX(g2) = 0
    c: DistanceX(g1) = 87
    c: Equal(g1,g0)
    c: Equal(g1,g3)
    c: Equal(g1,g2)
    c: Diameter(g1) = 4.25
    c: DistanceX(g3) = -87
    c: DistanceY(g3,g0) = 87
    c: DistanceY(g2,g3) = 87
FEATURE [Part::Extrusion] Extrude029  label="m4VerCuts001"
  Base = -> Sketch047
  Dir = (0,0,1)
  DirMode = 2
  FaceMakerClass = Part::FaceMakerBullseye
  LengthFwd = 20
  LengthRev = 0
  Placement = pos=(0,0,-65.5) rot=(0,0,1;0rad)
  Solid = true
  Symmetric = false
FEATURE [Part::Cut] Cut042  label="tube3to4s"
  Base = -> Cut040
  Tool = -> Extrude028
FEATURE [Part::Cut] Cut043  label="level03"
  Base = -> Fusion067
  Tool = -> Extrude029
FEATURE [Part::Cylinder] Cylinder139
  Angle = 360
  AttacherType = Attacher::AttachEngine3D
  FirstAngle = 0
  Height = 300
  Placement = pos=(0,0,90) rot=(1,0,0;1.5708rad)
  Radius = 2.13
  SecondAngle = 0
FEATURE [Part::Cylinder] Cylinder140
  Angle = 360
  AttacherType = Attacher::AttachEngine3D
  FirstAngle = 0
  Height = 300
  Placement = pos=(-150,-150,90) rot=(0.57735,0.57735,0.57735;2.0944rad)
  Radius = 2.13
  SecondAngle = 0
FEATURE [Part::MultiFuse] Fusion088  label="m4Cuts011"
  Placement = pos=(0,0,-130) rot=(0,0,1;0rad)
  Shapes = -> [Cylinder140,Cylinder139]
FEATURE [Part::Cut] Cut044  label="tube3to2s"
  Base = -> Tube002
  Tool = -> Fusion088
FEATURE [Part::Cylinder] Cylinder141
  Angle = 360
  AttacherType = Attacher::AttachEngine3D
  FirstAngle = 0
  Height = 300
  Placement = pos=(0,0,90) rot=(1,0,0;1.5708rad)
  Radius = 2.8
  SecondAngle = 0
FEATURE [Part::Cylinder] Cylinder142
  Angle = 360
  AttacherType = Attacher::AttachEngine3D
  FirstAngle = 0
  Height = 300
  Placement = pos=(-150,-150,90) rot=(0.57735,0.57735,0.57735;2.0944rad)
  Radius = 2.8
  SecondAngle = 0
FEATURE [Part::MultiFuse] Fusion089  label="m4HeatSetCuts003"
  Placement = pos=(0,0,-130) rot=(0,0,1;0rad)
  Shapes = -> [Cylinder142,Cylinder141]
FEATURE [Part::Cylinder] Cylinder143  label="heatSetHolds"
  Angle = 360
  AttacherType = Attacher::AttachEngine3D
  FirstAngle = 0
  Height = 10
  Placement = pos=(0,-72,-40) rot=(1,0,0;4.71239rad)
  Radius = 8
  SecondAngle = 0
FEATURE [Part::Cylinder] Cylinder144  label="heatSetHolds001"
  Angle = 360
  AttacherType = Attacher::AttachEngine3D
  FirstAngle = 0
  Height = 10
  Placement = pos=(1.91e-14,-228,-40) rot=(0,0.707107,-0.707107;3.14159rad)
  Radius = 8
  SecondAngle = 0
FEATURE [Part::Cylinder] Cylinder145  label="heatSetHolds002"
  Angle = 360
  AttacherType = Attacher::AttachEngine3D
  FirstAngle = 0
  Height = 10
  Placement = pos=(78,-150,-40) rot=(-0.57735,0.57735,-0.57735;2.0944rad)
  Radius = 8
  SecondAngle = 0
FEATURE [Part::Cylinder] Cylinder146  label="heatSetHolds003"
  Angle = 360
  AttacherType = Attacher::AttachEngine3D
  FirstAngle = 0
  Height = 10
  Placement = pos=(-78,-150,-40) rot=(-0.57735,-0.57735,0.57735;2.0944rad)
  Radius = 8
  SecondAngle = 0
FEATURE [Part::MultiFuse] Fusion090  label="m4HeatSetHolds"
  Shapes = -> [Cylinder143,Cylinder144,Cylinder145,Cylinder146]
FEATURE [Part::MultiFuse] Fusion091  label="level003s"
  Shapes = -> [Cut043,Fusion090]
FEATURE [Part::Cut] Cut045  label="level3s"
  Base = -> Fusion091
  Tool = -> Fusion089
FEATURE [Part::Cylinder] Cylinder147
  Angle = 360
  AttacherType = Attacher::AttachEngine3D
  FirstAngle = 0
  Height = 300
  Placement = pos=(0,0,90) rot=(1,0,0;1.5708rad)
  Radius = 2.13
  SecondAngle = 0
FEATURE [Part::Cylinder] Cylinder148
  Angle = 360
  AttacherType = Attacher::AttachEngine3D
  FirstAngle = 0
  Height = 300
  Placement = pos=(-150,-150,90) rot=(0.57735,0.57735,0.57735;2.0944rad)
  Radius = 2.13
  SecondAngle = 0
FEATURE [Part::Cylinder] Cylinder149
  Angle = 360
  AttacherType = Attacher::AttachEngine3D
  FirstAngle = 0
  Height = 300
  Placement = pos=(106.066,-43.934,90) rot=(0.862856,-0.357407,-0.357407;1.71777rad)
  Radius = 2.13
  SecondAngle = 0
FEATURE [Part::Cylinder] Cylinder150
  Angle = 360
  AttacherType = Attacher::AttachEngine3D
  FirstAngle = 0
  Height = 300
  Placement = pos=(-106.066,-43.934,90) rot=(0.862856,0.357407,0.357407;1.71777rad)
  Radius = 2.13
  SecondAngle = 0
FEATURE [Part::MultiFuse] Fusion092  label="m4Cuts012"
  Placement = pos=(0,0,-82) rot=(0,0,1;0rad)
  Shapes = -> [Cylinder148,Cylinder147]
FEATURE [Part::MultiFuse] Fusion093  label="m4Cuts013"
  Placement = pos=(0,0,-82) rot=(0,0,1;0rad)
  Shapes = -> [Cylinder149,Cylinder150]
FEATURE [Part::MultiFuse] Fusion094  label="m4Cuts014"
  Shapes = -> [Fusion092,Fusion093]
FEATURE [Part::Cut] Cut046  label="tubeLevel3to2s"
  Base = -> Cut044
  Tool = -> Fusion094
FEATURE [Part::Fillet] Fillet002  label="level5s001"
  Base = -> Cut038
  Edges = 3 edges r=3: [Edge3,Edge7,Edge32]
FEATURE [Part::FeaturePython] Tube005  # WARN: FeaturePython — macro-defined, semantics opaque (R4)
  AttacherType = Attacher::AttachEngine3D
  Height = 3
  InnerRadius = 95
  OuterRadius = 98
  Placement = pos=(0,-150,-188) rot=(0,0,1;0rad)
FEATURE [Part::Cylinder] Cylinder151
  Angle = 360
  AttacherType = Attacher::AttachEngine3D
  FirstAngle = 0
  Height = 300
  Placement = pos=(0,0,90) rot=(1,0,0;1.5708rad)
  Radius = 2.13
  SecondAngle = 0
FEATURE [Part::Cylinder] Cylinder152
  Angle = 360
  AttacherType = Attacher::AttachEngine3D
  FirstAngle = 0
  Height = 300
  Placement = pos=(-150,-150,90) rot=(0.57735,0.57735,0.57735;2.0944rad)
  Radius = 2.13
  SecondAngle = 0
FEATURE [Part::MultiFuse] Fusion096  label="m4Cuts015"
  Placement = pos=(0,0,-321) rot=(0,0,1;0rad)
  Shapes = -> [Cylinder152,Cylinder151]
FEATURE [Sketcher::SketchObject] Sketch048  label="top016"
  FullyConstrained = true
  sketch-geometry (2):
    g0: Circle CenterX=0 CenterY=-150 CenterZ=0 NormalX=0 NormalY=0 NormalZ=1 AngleXU=0 Radius=98
    g1: Circle CenterX=0 CenterY=-150 CenterZ=0 NormalX=0 NormalY=0 NormalZ=1 AngleXU=0 Radius=76
  constraints (5):
    c: PointOnObject(g0,g-2)
    c: Diameter(g0) = 196
    c: DistanceY(g0) = -150
    c: Coincident(g1,g0)
    c: Radius(g1) = 76
FEATURE [Part::Extrusion] Extrude030  label="TupeConnectLevel005"
  Base = -> Sketch048
  Dir = (0,0,1)
  DirMode = 2
  FaceMakerClass = Part::FaceMakerBullseye
  LengthFwd = 5
  LengthRev = 0
  Placement = pos=(0,0,-65) rot=(0,0,1;0rad)
  Solid = true
  Symmetric = false
FEATURE [Sketcher::SketchObject] Sketch049
  FullyConstrained = true
  sketch-geometry (4):
    g0: Circle CenterX=0 CenterY=-68 CenterZ=0 NormalX=0 NormalY=0 NormalZ=1 AngleXU=0 Radius=2.8
    g1: Circle CenterX=82 CenterY=-150 CenterZ=0 NormalX=0 NormalY=0 NormalZ=1 AngleXU=0 Radius=2.8
    g2: Circle CenterX=0 CenterY=-232 CenterZ=0 NormalX=0 NormalY=0 NormalZ=1 AngleXU=0 Radius=2.8
    g3: Circle CenterX=-82 CenterY=-150 CenterZ=0 NormalX=0 NormalY=0 NormalZ=1 AngleXU=0 Radius=2.8
  constraints (12):
    c: PointOnObject(g0,g-2)
    c: DistanceY(g1) = -150
    c: DistanceY(g1,g3) = 0
    c: DistanceX(g2) = 0
    c: DistanceX(g1) = 82
    c: Equal(g1,g0)
    c: Equal(g1,g3)
    c: Equal(g1,g2)
    c: Diameter(g1) = 5.6
    c: DistanceX(g3) = -82
    c: DistanceY(g3,g0) = 82
    c: DistanceY(g2,g3) = 82
FEATURE [Part::Extrusion] Extrude031  label="m4HeatSetVerCuts004"
  Base = -> Sketch049
  Dir = (0,0,1)
  DirMode = 2
  FaceMakerClass = Part::FaceMakerBullseye
  LengthFwd = 20
  LengthRev = 0
  Placement = pos=(0,0,-193) rot=(0,0,1;0rad)
  Solid = true
  Symmetric = false
FEATURE [Part::FeaturePython] Tube006  # WARN: FeaturePython — macro-defined, semantics opaque (R4)
  AttacherType = Attacher::AttachEngine3D
  Height = 65
  InnerRadius = 94
  OuterRadius = 98
  Placement = pos=(0,-150,-125) rot=(0,0,1;0rad)
FEATURE [Part::MultiFuse] Fusion095  label="tube5to005"
  Placement = pos=(0,0,-125) rot=(0,0,1;0rad)
  Shapes = -> [Extrude030,Tube006]
FEATURE [Part::Cut] Cut047  label="tube4to006"
  Base = -> Fusion095
  Tool = -> Fusion096
FEATURE [Part::Cut] Cut048  label="tube4to5s001"
  Base = -> Cut047
  Tool = -> Extrude031
FEATURE [Part::Fillet] Fillet003  label="level5s002"
  Base = -> Cut048
  Edges = 3 edges r=3: [Edge3,Edge7,Edge32]
FEATURE [Part::Cut] Cut049  label="cutAddOn"
  Base = -> Tube005
  Placement = pos=(0,0,0.25) rot=(0,0,1;0rad)
  Tool = -> Fillet003
FEATURE [Part::MultiFuse] Fusion097  label="tube4to3S"
  Shapes = -> [Cut042,Cut049]
FEATURE [Part::Fillet] Fillet004  label="tube4to3s"
  Base = -> Fusion097
  Edges = 1 edges r=3: [Edge3]
FEATURE [Part::Cylinder] Cylinder153
  Angle = 360
  AttacherType = Attacher::AttachEngine3D
  FirstAngle = 0
  Height = 300
  Placement = pos=(0,0,90) rot=(1,0,0;1.5708rad)
  Radius = 2.13
  SecondAngle = 0
FEATURE [Part::Cylinder] Cylinder154
  Angle = 360
  AttacherType = Attacher::AttachEngine3D
  FirstAngle = 0
  Height = 300
  Placement = pos=(-150,-150,90) rot=(0.57735,0.57735,0.57735;2.0944rad)
  Radius = 2.13
  SecondAngle = 0
FEATURE [Part::MultiFuse] Fusion099  label="m4Cuts016"
  Placement = pos=(0,0,-321) rot=(0,0,1;0rad)
  Shapes = -> [Cylinder154,Cylinder153]
FEATURE [Sketcher::SketchObject] Sketch050  label="top017"
  FullyConstrained = true
  sketch-geometry (2):
    g0: Circle CenterX=0 CenterY=-150 CenterZ=0 NormalX=0 NormalY=0 NormalZ=1 AngleXU=0 Radius=98
    g1: Circle CenterX=0 CenterY=-150 CenterZ=0 NormalX=0 NormalY=0 NormalZ=1 AngleXU=0 Radius=76
  constraints (5):
    c: PointOnObject(g0,g-2)
    c: Diameter(g0) = 196
    c: DistanceY(g0) = -150
    c: Coincident(g1,g0)
    c: Radius(g1) = 76
FEATURE [Part::Extrusion] Extrude032  label="TupeConnectLevel006"
  Base = -> Sketch050
  Dir = (0,0,1)
  DirMode = 2
  FaceMakerClass = Part::FaceMakerBullseye
  LengthFwd = 5
  LengthRev = 0
  Placement = pos=(0,0,-65) rot=(0,0,1;0rad)
  Solid = true
  Symmetric = false
FEATURE [Sketcher::SketchObject] Sketch051
  FullyConstrained = true
  sketch-geometry (4):
    g0: Circle CenterX=0 CenterY=-68 CenterZ=0 NormalX=0 NormalY=0 NormalZ=1 AngleXU=0 Radius=2.8
    g1: Circle CenterX=82 CenterY=-150 CenterZ=0 NormalX=0 NormalY=0 NormalZ=1 AngleXU=0 Radius=2.8
    g2: Circle CenterX=0 CenterY=-232 CenterZ=0 NormalX=0 NormalY=0 NormalZ=1 AngleXU=0 Radius=2.8
    g3: Circle CenterX=-82 CenterY=-150 CenterZ=0 NormalX=0 NormalY=0 NormalZ=1 AngleXU=0 Radius=2.8
  constraints (12):
    c: PointOnObject(g0,g-2)
    c: DistanceY(g1) = -150
    c: DistanceY(g1,g3) = 0
    c: DistanceX(g2) = 0
    c: DistanceX(g1) = 82
    c: Equal(g1,g0)
    c: Equal(g1,g3)
    c: Equal(g1,g2)
    c: Diameter(g1) = 5.6
    c: DistanceX(g3) = -82
    c: DistanceY(g3,g0) = 82
    c: DistanceY(g2,g3) = 82
FEATURE [Part::Extrusion] Extrude033  label="m4HeatSetVerCuts005"
  Base = -> Sketch051
  Dir = (0,0,1)
  DirMode = 2
  FaceMakerClass = Part::FaceMakerBullseye
  LengthFwd = 20
  LengthRev = 0
  Placement = pos=(0,0,-193) rot=(0,0,1;0rad)
  Solid = true
  Symmetric = false
FEATURE [Part::FeaturePython] Tube007  # WARN: FeaturePython — macro-defined, semantics opaque (R4)
  AttacherType = Attacher::AttachEngine3D
  Height = 3
  InnerRadius = 95
  OuterRadius = 98
  Placement = pos=(0,-150,-188) rot=(0,0,1;0rad)
FEATURE [Part::FeaturePython] Tube008  # WARN: FeaturePython — macro-defined, semantics opaque (R4)
  AttacherType = Attacher::AttachEngine3D
  Height = 65
  InnerRadius = 94
  OuterRadius = 98
  Placement = pos=(0,-150,-125) rot=(0,0,1;0rad)
FEATURE [Part::MultiFuse] Fusion098  label="tube5to006"
  Placement = pos=(0,0,-125) rot=(0,0,1;0rad)
  Shapes = -> [Extrude032,Tube008]
FEATURE [Part::Cut] Cut050  label="tube4to007"
  Base = -> Fusion098
  Tool = -> Fusion099
FEATURE [Part::Cut] Cut051  label="tube4to5s002"
  Base = -> Cut050
  Tool = -> Extrude033
FEATURE [Part::Fillet] Fillet005  label="level5s003"
  Base = -> Cut051
  Edges = 3 edges r=3: [Edge3,Edge7,Edge32]
FEATURE [Part::Cut] Cut052  label="cutAddOn001"
  Base = -> Tube007
  Placement = pos=(0,0,125.25) rot=(0,0,1;0rad)
  Tool = -> Fillet005
FEATURE [Part::MultiFuse] Fusion100  label="level3to2"
  Shapes = -> [Cut046,Cut052]
FEATURE [Part::Fillet] Fillet006  label="level003to2s"
  Base = -> Fusion100
  Edges = 1 edges r=3: [Edge5]
FEATURE [Part::Cylinder] Cylinder155
  Angle = 360
  AttacherType = Attacher::AttachEngine3D
  FirstAngle = 0
  Height = 300
  Placement = pos=(0,0,90) rot=(1,0,0;1.5708rad)
  Radius = 2.13
  SecondAngle = 0
FEATURE [Part::Cylinder] Cylinder156
  Angle = 360
  AttacherType = Attacher::AttachEngine3D
  FirstAngle = 0
  Height = 300
  Placement = pos=(-150,-150,90) rot=(0.57735,0.57735,0.57735;2.0944rad)
  Radius = 2.13
  SecondAngle = 0
FEATURE [Part::MultiFuse] Fusion102  label="m4Cuts017"
  Placement = pos=(0,0,-321) rot=(0,0,1;0rad)
  Shapes = -> [Cylinder156,Cylinder155]
FEATURE [Sketcher::SketchObject] Sketch052  label="top018"
  FullyConstrained = true
  sketch-geometry (2):
    g0: Circle CenterX=0 CenterY=-150 CenterZ=0 NormalX=0 NormalY=0 NormalZ=1 AngleXU=0 Radius=98
    g1: Circle CenterX=0 CenterY=-150 CenterZ=0 NormalX=0 NormalY=0 NormalZ=1 AngleXU=0 Radius=76
  constraints (5):
    c: PointOnObject(g0,g-2)
    c: Diameter(g0) = 196
    c: DistanceY(g0) = -150
    c: Coincident(g1,g0)
    c: Radius(g1) = 76
FEATURE [Part::Extrusion] Extrude034  label="TupeConnectLevel007"
  Base = -> Sketch052
  Dir = (0,0,1)
  DirMode = 2
  FaceMakerClass = Part::FaceMakerBullseye
  LengthFwd = 5
  LengthRev = 0
  Placement = pos=(0,0,-65) rot=(0,0,1;0rad)
  Solid = true
  Symmetric = false
FEATURE [Sketcher::SketchObject] Sketch053
  FullyConstrained = true
  sketch-geometry (4):
    g0: Circle CenterX=0 CenterY=-68 CenterZ=0 NormalX=0 NormalY=0 NormalZ=1 AngleXU=0 Radius=2.8
    g1: Circle CenterX=82 CenterY=-150 CenterZ=0 NormalX=0 NormalY=0 NormalZ=1 AngleXU=0 Radius=2.8
    g2: Circle CenterX=0 CenterY=-232 CenterZ=0 NormalX=0 NormalY=0 NormalZ=1 AngleXU=0 Radius=2.8
    g3: Circle CenterX=-82 CenterY=-150 CenterZ=0 NormalX=0 NormalY=0 NormalZ=1 AngleXU=0 Radius=2.8
  constraints (12):
    c: PointOnObject(g0,g-2)
    c: DistanceY(g1) = -150
    c: DistanceY(g1,g3) = 0
    c: DistanceX(g2) = 0
    c: DistanceX(g1) = 82
    c: Equal(g1,g0)
    c: Equal(g1,g3)
    c: Equal(g1,g2)
    c: Diameter(g1) = 5.6
    c: DistanceX(g3) = -82
    c: DistanceY(g3,g0) = 82
    c: DistanceY(g2,g3) = 82
FEATURE [Part::Extrusion] Extrude035  label="m4HeatSetVerCuts006"
  Base = -> Sketch053
  Dir = (0,0,1)
  DirMode = 2
  FaceMakerClass = Part::FaceMakerBullseye
  LengthFwd = 20
  LengthRev = 0
  Placement = pos=(0,0,-193) rot=(0,0,1;0rad)
  Solid = true
  Symmetric = false
FEATURE [Part::FeaturePython] Tube009  # WARN: FeaturePython — macro-defined, semantics opaque (R4)
  AttacherType = Attacher::AttachEngine3D
  Height = 3
  InnerRadius = 95
  OuterRadius = 98
  Placement = pos=(0,-150,-188) rot=(0,0,1;0rad)
FEATURE [Part::FeaturePython] Tube010  # WARN: FeaturePython — macro-defined, semantics opaque (R4)
  AttacherType = Attacher::AttachEngine3D
  Height = 65
  InnerRadius = 94
  OuterRadius = 98
  Placement = pos=(0,-150,-125) rot=(0,0,1;0rad)
FEATURE [Part::MultiFuse] Fusion101  label="tube5to007"
  Placement = pos=(0,0,-125) rot=(0,0,1;0rad)
  Shapes = -> [Extrude034,Tube010]
FEATURE [Part::Cut] Cut053  label="tube4to008"
  Base = -> Fusion101
  Tool = -> Fusion102
FEATURE [Part::Cut] Cut054  label="tube4to5s003"
  Base = -> Cut053
  Tool = -> Extrude035
FEATURE [Part::Fillet] Fillet007  label="level5s004"
  Base = -> Cut054
  Edges = 3 edges r=3: [Edge3,Edge7,Edge32]
FEATURE [Part::Cut] Cut055  label="cutAddOn002"
  Base = -> Tube009
  Placement = pos=(0,0,205.25) rot=(0,0,1;0rad)
  Tool = -> Fillet007
FEATURE [Part::MultiFuse] Fusion103  label="srs003"
  Shapes = -> [Cut055,Cut033]
FEATURE [Sketcher::SketchObject] Sketch054
  FullyConstrained = true
  Placement = pos=(0,0,0) rot=(1,0,0;1.5708rad)
  sketch-geometry (8):
    g0: LineSegment StartX=-20.75 StartY=-250 StartZ=0 EndX=-12.75 EndY=-250 EndZ=0
    g1: LineSegment StartX=-12.75 StartY=-250 StartZ=0 EndX=-12.75 EndY=-275.75 EndZ=0
    g2: LineSegment StartX=-12.75 StartY=-275.75 StartZ=0 EndX=12.75 EndY=-275.75 EndZ=0
    g3: LineSegment StartX=12.75 StartY=-275.75 StartZ=0 EndX=12.75 EndY=-250 EndZ=0
    g4: LineSegment StartX=12.75 StartY=-250 StartZ=0 EndX=20.75 EndY=-250 EndZ=0
    g5: LineSegment StartX=20.75 StartY=-250 StartZ=0 EndX=20.75 EndY=-283.75 EndZ=0
    g6: LineSegment StartX=20.75 StartY=-283.75 StartZ=0 EndX=-20.75 EndY=-283.75 EndZ=0
    g7: LineSegment StartX=-20.75 StartY=-283.75 StartZ=0 EndX=-20.75 EndY=-250 EndZ=0
  constraints (24):
    c: Horizontal(g0)
    c: Vertical(g1)
    c: Coincident(g2,g1)
    c: Horizontal(g2)
    c: Vertical(g3)
    c: Coincident(g4,g3)
    c: Horizontal(g4)
    c: Coincident(g5,g4)
    c: Vertical(g5)
    c: Coincident(g6,g5)
    c: Horizontal(g6)
    c: Coincident(g7,g6)
    c: Coincident(g7,g0)
    c: Vertical(g7)
    c: Coincident(g0,g1)
    c: DistanceY(g0) = -250
    c: DistanceX(g0) = -12.75
    c: DistanceX(g3) = 12.75
    c: DistanceY(g1) = -275.75
    c: Coincident(g3,g2)
    c: DistanceY(g3,g0) = 0
    c: DistanceX(g0,g0) = 8
    c: DistanceX(g3,g4) = 8
    c: DistanceY(g5,g2) = 8
FEATURE [Part::Extrusion] Extrude036
  Base = -> Sketch054
  Dir = (0,-1,-3e-16)
  DirMode = 2
  FaceMakerClass = Part::FaceMakerBullseye
  LengthFwd = 100
  LengthRev = 0
  Placement = pos=(0,-70,0) rot=(0,0,1;0rad)
  Solid = true
  Symmetric = false
FEATURE [Part::Fillet] Fillet008
  Base = -> Extrude036
  Edges = 2 edges r=5: [Edge17,Edge20]
FEATURE [Part::Fillet] Fillet009  label="framingSupportsHolders"
  Base = -> Fillet008
  Edges = 2 edges r=2: [Edge26,Edge28]
FEATURE [Part::MultiFuse] Fusion104
  Shapes = -> [Fillet009,Cut041]
FEATURE [Part::Fillet] Fillet010
  Base = -> Fusion104
  Edges = 2 edges r=5: [Edge40,Edge46]
FEATURE [Mesh::Feature] tinker
  Placement = pos=(3,-241,-145) rot=(1,0,0;1.5708rad)
FEATURE [Sketcher::SketchObject] Sketch055
  FullyConstrained = false
  Placement = pos=(0,0,0) rot=(1,0,0;1.5708rad)
  sketch-geometry (884):
    g0: LineSegment StartX=35.7189 StartY=14.4677 StartZ=0 EndX=35.5415 EndY=14.2824 EndZ=0
    g1: LineSegment StartX=35.5415 StartY=14.2079 StartZ=0 EndX=35.4533 EndY=14.1342 EndZ=0
    g2: LineSegment StartX=35.4533 StartY=14.1342 StartZ=0 EndX=35.4583 EndY=14.0618 EndZ=0
    g3: LineSegment StartX=35.4583 StartY=14.0618 StartZ=0 EndX=35.3195 EndY=13.9216 EndZ=0
    g4: LineSegment StartX=35.3195 StartY=13.9216 StartZ=0 EndX=35.3195 EndY=13.853 EndZ=0
    g5: LineSegment StartX=35.3195 StartY=13.853 StartZ=0 EndX=35.248 EndY=13.7975 EndZ=0
    g6: LineSegment StartX=35.248 StartY=13.7975 StartZ=0 EndX=35.248 EndY=13.6573 EndZ=0
    g7: LineSegment StartX=35.248 StartY=13.6573 StartZ=0 EndX=35.1825 EndY=13.5912 EndZ=0
    g8: LineSegment StartX=35.1825 StartY=13.5912 StartZ=0 EndX=35.1825 EndY=13.2647 EndZ=0
    g9: LineSegment StartX=35.1825 StartY=13.2647 StartZ=0 EndX=35.0994 EndY=13.159 EndZ=0
    g10: LineSegment StartX=35.0994 StartY=13.159 StartZ=0 EndX=35.0994 EndY=13.0459 EndZ=0
    g11: LineSegment StartX=35.0994 StartY=13.0459 StartZ=0 EndX=35.0336 EndY=12.9565 EndZ=0
    g12: LineSegment StartX=35.0336 StartY=12.9565 StartZ=0 EndX=35.0336 EndY=12.3489 EndZ=0
    g13: LineSegment StartX=35.0336 StartY=12.3489 StartZ=0 EndX=35.1008 EndY=12.3489 EndZ=0
    g14: LineSegment StartX=35.1008 StartY=12.3489 StartZ=0 EndX=35.1008 EndY=12.2102 EndZ=0
    g15: LineSegment StartX=35.1008 StartY=12.2102 StartZ=0 EndX=35.1709 EndY=12.2072 EndZ=0
    g16: LineSegment StartX=35.1709 StartY=12.2072 StartZ=0 EndX=35.1709 EndY=11.9948 EndZ=0
    g17: LineSegment StartX=35.1709 StartY=11.9948 StartZ=0 EndX=35.2359 EndY=11.9948 EndZ=0
    g18: LineSegment StartX=35.2359 StartY=11.9948 StartZ=0 EndX=35.2359 EndY=11.9181 EndZ=0
    g19: LineSegment StartX=35.2359 StartY=11.9181 StartZ=0 EndX=35.3001 EndY=11.9181 EndZ=0
    g20: LineSegment StartX=35.3001 StartY=11.9181 StartZ=0 EndX=35.3001 EndY=11.8402 EndZ=0
    g21: LineSegment StartX=35.3001 StartY=11.8402 StartZ=0 EndX=35.3675 EndY=11.8402 EndZ=0
    g22: LineSegment StartX=35.3675 StartY=11.8402 StartZ=0 EndX=35.3675 EndY=11.2433 EndZ=0
    g23: LineSegment StartX=35.3675 StartY=11.2433 StartZ=0 EndX=35.435 EndY=11.2433 EndZ=0
    g24: LineSegment StartX=35.435 StartY=11.2433 StartZ=0 EndX=35.435 EndY=11.1727 EndZ=0
    g25: LineSegment StartX=35.435 StartY=11.1727 StartZ=0 EndX=35.5098 EndY=11.1727 EndZ=0
    g26: LineSegment StartX=35.5098 StartY=11.1727 StartZ=0 EndX=35.5098 EndY=11.1026 EndZ=0
    g27: LineSegment StartX=35.5098 StartY=11.1026 StartZ=0 EndX=35.6558 EndY=11.1026 EndZ=0
    g28: LineSegment StartX=35.6558 StartY=11.1026 StartZ=0 EndX=35.6558 EndY=11.0252 EndZ=0
    g29: LineSegment StartX=35.6558 StartY=11.0252 StartZ=0 EndX=35.7128 EndY=11.0252 EndZ=0
    g30: LineSegment StartX=35.7128 StartY=11.0252 StartZ=0 EndX=35.7128 EndY=10.7682 EndZ=0
    g31: LineSegment StartX=35.7128 StartY=10.7682 StartZ=0 EndX=35.7756 EndY=10.7681 EndZ=0
    g32: LineSegment StartX=35.7756 StartY=10.7681 StartZ=0 EndX=35.7756 EndY=10.5644 EndZ=0
    g33: LineSegment StartX=35.7756 StartY=10.5644 StartZ=0 EndX=35.846 EndY=10.5644 EndZ=0
    g34: LineSegment StartX=35.846 StartY=10.5644 StartZ=0 EndX=35.846 EndY=10.4767 EndZ=0
    g35: LineSegment StartX=35.846 StartY=10.4767 StartZ=0 EndX=35.988 EndY=10.4767 EndZ=0
    g36: LineSegment StartX=35.988 StartY=10.4767 StartZ=0 EndX=35.988 EndY=10.4228 EndZ=0
    g37: LineSegment StartX=35.988 StartY=10.4228 StartZ=0 EndX=36.1201 EndY=10.4228 EndZ=0
    g38: LineSegment StartX=36.1201 StartY=10.4228 StartZ=0 EndX=36.1201 EndY=10.2907 EndZ=0
    g39: LineSegment StartX=36.1201 StartY=10.2907 StartZ=0 EndX=36.1926 EndY=10.2907 EndZ=0
    g40: LineSegment StartX=36.1926 StartY=10.2907 StartZ=0 EndX=36.1926 EndY=10.1585 EndZ=0
    g41: LineSegment StartX=36.1926 StartY=10.1585 StartZ=0 EndX=36.2533 EndY=10.1585 EndZ=0
    g42: LineSegment StartX=36.2533 StartY=10.1585 StartZ=0 EndX=36.2533 EndY=10.0897 EndZ=0
    g43: LineSegment StartX=36.2533 StartY=10.0897 StartZ=0 EndX=36.3179 EndY=10.0897 EndZ=0
    g44: LineSegment StartX=36.3179 StartY=10.0897 StartZ=0 EndX=36.3179 EndY=9.8871 EndZ=0
    g45: LineSegment StartX=36.3179 StartY=9.8871 StartZ=0 EndX=36.3888 EndY=9.8871 EndZ=0
    g46: LineSegment StartX=36.3888 StartY=9.8871 StartZ=0 EndX=36.3888 EndY=9.73503 EndZ=0
    g47: LineSegment StartX=36.3888 StartY=9.73503 StartZ=0 EndX=36.4516 EndY=9.73503 EndZ=0
    g48: LineSegment StartX=36.4516 StartY=9.73503 StartZ=0 EndX=36.4516 EndY=9.65617 EndZ=0
    g49: LineSegment StartX=36.4516 StartY=9.65617 StartZ=0 EndX=36.6707 EndY=9.65617 EndZ=0
    g50: LineSegment StartX=36.6707 StartY=9.65617 StartZ=0 EndX=36.6707 EndY=9.58899 EndZ=0
    g51: LineSegment StartX=36.6707 StartY=9.58899 StartZ=0 EndX=36.7335 EndY=9.58899 EndZ=0
    g52: LineSegment StartX=36.7335 StartY=9.58899 StartZ=0 EndX=36.7335 EndY=9.51158 EndZ=0
    g53: LineSegment StartX=36.7335 StartY=9.51158 StartZ=0 EndX=36.7948 EndY=9.51158 EndZ=0
    g54: LineSegment StartX=36.7948 StartY=9.51158 StartZ=0 EndX=36.7948 EndY=9.40351 EndZ=0
    g55: LineSegment StartX=36.7948 StartY=9.40351 StartZ=0 EndX=36.8664 EndY=9.40351 EndZ=0
    g56: LineSegment StartX=36.8664 StartY=9.40351 StartZ=0 EndX=36.8664 EndY=9.2487 EndZ=0
    g57: LineSegment StartX=36.8664 StartY=9.2487 StartZ=0 EndX=36.9292 EndY=9.2487 EndZ=0
    g58: LineSegment StartX=36.9292 StartY=9.2487 StartZ=0 EndX=36.9292 EndY=9.18298 EndZ=0
    g59: LineSegment StartX=36.9292 StartY=9.18298 StartZ=0 EndX=37.0036 EndY=9.18298 EndZ=0
    g60: LineSegment StartX=37.0036 StartY=9.18298 StartZ=0 EndX=37.0036 EndY=9.12121 EndZ=0
    g61: LineSegment StartX=37.0036 StartY=9.12121 StartZ=0 EndX=37.066 EndY=9.12121 EndZ=0
    g62: LineSegment StartX=37.066 StartY=9.12121 StartZ=0 EndX=37.066 EndY=8.98122 EndZ=0
    g63: LineSegment StartX=37.066 StartY=8.98122 StartZ=0 EndX=37.1365 EndY=8.98122 EndZ=0
    g64: LineSegment StartX=37.1365 StartY=8.98122 StartZ=0 EndX=37.1365 EndY=8.85617 EndZ=0
    g65: LineSegment StartX=37.1365 StartY=8.85617 StartZ=0 EndX=37.2117 EndY=8.85617 EndZ=0
    g66: LineSegment StartX=37.2117 StartY=8.85617 StartZ=0 EndX=37.2117 EndY=8.77808 EndZ=0
    g67: LineSegment StartX=37.2117 StartY=8.77808 StartZ=0 EndX=37.276 EndY=8.7779 EndZ=0
    g68: LineSegment StartX=37.276 StartY=8.7779 StartZ=0 EndX=37.276 EndY=8.70839 EndZ=0
    g69: LineSegment StartX=37.276 StartY=8.70839 StartZ=0 EndX=37.3475 EndY=8.70839 EndZ=0
    g70: LineSegment StartX=37.3475 StartY=8.70839 StartZ=0 EndX=37.3475 EndY=8.58602 EndZ=0
    g71: LineSegment StartX=37.3475 StartY=8.58602 StartZ=0 EndX=37.4111 EndY=8.58602 EndZ=0
    g72: LineSegment StartX=37.4111 StartY=8.58602 StartZ=0 EndX=37.4111 EndY=8.50272 EndZ=0
    g73: LineSegment StartX=37.4111 StartY=8.50272 StartZ=0 EndX=37.4778 EndY=8.50272 EndZ=0
    g74: LineSegment StartX=37.4778 StartY=8.50272 StartZ=0 EndX=37.4778 EndY=8.37852 EndZ=0
    g75: LineSegment StartX=37.4778 StartY=8.37852 StartZ=0 EndX=37.55 EndY=8.37852 EndZ=0
    g76: LineSegment StartX=37.55 StartY=8.37852 StartZ=0 EndX=37.55 EndY=8.29594 EndZ=0
    g77: LineSegment StartX=37.55 StartY=8.29594 StartZ=0 EndX=37.6238 EndY=8.29594 EndZ=0
    g78: LineSegment StartX=37.6238 StartY=8.29594 StartZ=0 EndX=37.6238 EndY=8.20831 EndZ=0
    g79: LineSegment StartX=37.6238 StartY=8.20831 StartZ=0 EndX=37.6953 EndY=8.21123 EndZ=0
    g80: LineSegment StartX=37.6953 StartY=8.21123 StartZ=0 EndX=37.6953 EndY=8.14022 EndZ=0
    g81: LineSegment StartX=37.6953 StartY=8.14022 StartZ=0 EndX=37.7536 EndY=8.14414 EndZ=0
    g82: LineSegment StartX=37.7536 StartY=8.14414 StartZ=0 EndX=37.7574 EndY=8.06459 EndZ=0
    g83: LineSegment StartX=37.7574 StartY=8.06459 StartZ=0 EndX=37.8181 EndY=8.06459 EndZ=0
    g84: LineSegment StartX=37.8181 StartY=8.06459 StartZ=0 EndX=37.8216 EndY=7.98967 EndZ=0
    g85: LineSegment StartX=37.8216 StartY=7.98967 StartZ=0 EndX=38.1025 EndY=7.98967 EndZ=0
    g86: LineSegment StartX=38.1025 StartY=7.98967 StartZ=0 EndX=38.1917 EndY=8.08042 EndZ=0
    g87: LineSegment StartX=38.1917 StartY=8.08042 StartZ=0 EndX=38.2417 EndY=8.08577 EndZ=0
    g88: LineSegment StartX=38.2417 StartY=8.08577 StartZ=0 EndX=38.4557 EndY=8.32302 EndZ=0
    g89: LineSegment StartX=38.4557 StartY=8.32302 StartZ=0 EndX=38.5235 EndY=8.32302 EndZ=0
    g90: LineSegment StartX=38.5235 StartY=8.32302 StartZ=0 EndX=38.5887 EndY=8.40314 EndZ=0
    g91: LineSegment StartX=38.5887 StartY=8.40314 StartZ=0 EndX=38.6773 EndY=8.40314 EndZ=0
    g92: LineSegment StartX=38.6773 StartY=8.40314 StartZ=0 EndX=39.0643 EndY=8.80818 EndZ=0
    g93: LineSegment StartX=39.0643 StartY=8.80818 StartZ=0 EndX=39.152 EndY=8.80818 EndZ=0
    g94: LineSegment StartX=39.152 StartY=8.80818 StartZ=0 EndX=39.5355 EndY=9.19803 EndZ=0
    g95: LineSegment StartX=39.5355 StartY=9.19803 StartZ=0 EndX=39.6318 EndY=9.19803 EndZ=0
    g96: LineSegment StartX=39.6318 StartY=9.19803 StartZ=0 EndX=39.792 EndY=9.38195 EndZ=0
    g97: LineSegment StartX=39.792 StartY=9.38195 StartZ=0 EndX=39.7884 EndY=9.45608 EndZ=0
    g98: LineSegment StartX=39.7884 StartY=9.45608 StartZ=0 EndX=39.9772 EndY=9.63446 EndZ=0
    g99: LineSegment StartX=39.9772 StartY=9.63446 StartZ=0 EndX=39.9772 EndY=9.72533 EndZ=0
    g100: LineSegment StartX=39.9772 StartY=9.72533 StartZ=0 EndX=40.1697 EndY=9.91904 EndZ=0
    g101: LineSegment StartX=40.1697 StartY=9.91904 StartZ=0 EndX=40.1746 EndY=9.99558 EndZ=0
    g102: LineSegment StartX=40.1746 StartY=9.99558 StartZ=0 EndX=40.2388 EndY=10.0603 EndZ=0
    g103: LineSegment StartX=40.2388 StartY=10.0603 StartZ=0 EndX=40.2423 EndY=10.1261 EndZ=0
    g104: LineSegment StartX=40.2423 StartY=10.1261 StartZ=0 EndX=40.5948 EndY=10.4793 EndZ=0
    g105: LineSegment StartX=40.5948 StartY=10.4793 StartZ=0 EndX=40.5948 EndY=10.5499 EndZ=0
    g106: LineSegment StartX=40.5948 StartY=10.5499 StartZ=0 EndX=40.6701 EndY=10.618 EndZ=0
    g107: LineSegment StartX=40.6701 StartY=10.618 StartZ=0 EndX=40.6581 EndY=10.6527 EndZ=0
    g108: LineSegment StartX=40.6581 StartY=10.6527 StartZ=0 EndX=40.6988 EndY=10.6527 EndZ=0
    g109: LineSegment StartX=40.6988 StartY=10.6527 StartZ=0 EndX=40.9317 EndY=10.8877 EndZ=0
    g110: LineSegment StartX=40.9317 StartY=10.8877 StartZ=0 EndX=40.9317 EndY=10.9592 EndZ=0
    g111: LineSegment StartX=40.9317 StartY=10.9592 StartZ=0 EndX=41.0136 EndY=11.0405 EndZ=0
    g112: LineSegment StartX=41.0136 StartY=11.0405 StartZ=0 EndX=41.0068 EndY=11.1648 EndZ=0
    g113: LineSegment StartX=41.0068 StartY=11.1648 StartZ=0 EndX=41.0763 EndY=11.2275 EndZ=0
    g114: LineSegment StartX=41.0763 StartY=11.2275 StartZ=0 EndX=41.0723 EndY=11.2979 EndZ=0
    g115: LineSegment StartX=41.0723 StartY=11.2979 StartZ=0 EndX=41.15 EndY=11.3821 EndZ=0
    g116: LineSegment StartX=41.15 StartY=11.3821 StartZ=0 EndX=41.15 EndY=11.5724 EndZ=0
    g117: LineSegment StartX=41.15 StartY=11.5724 StartZ=0 EndX=41.2317 EndY=11.6351 EndZ=0
    g118: LineSegment StartX=41.2317 StartY=11.6351 StartZ=0 EndX=41.2155 EndY=11.7717 EndZ=0
    g119: LineSegment StartX=41.2155 StartY=11.7717 StartZ=0 EndX=41.2837 EndY=11.8432 EndZ=0
    g120: LineSegment StartX=41.2837 StartY=11.8432 StartZ=0 EndX=41.2786 EndY=11.8698 EndZ=0
    g121: LineSegment StartX=41.2786 StartY=11.8698 StartZ=0 EndX=41.3138 EndY=11.8698 EndZ=0
    g122: LineSegment StartX=41.3138 StartY=11.8698 StartZ=0 EndX=41.5455 EndY=12.1045 EndZ=0
    g123: LineSegment StartX=41.5455 StartY=12.1045 StartZ=0 EndX=41.5618 EndY=12.4305 EndZ=0
    g124: LineSegment StartX=41.5618 StartY=12.4305 StartZ=0 EndX=41.6277 EndY=12.505 EndZ=0
    g125: LineSegment StartX=41.6277 StartY=12.505 StartZ=0 EndX=41.6277 EndY=12.6108 EndZ=0
    g126: LineSegment StartX=41.6277 StartY=12.6108 StartZ=0 EndX=41.692 EndY=12.5393 EndZ=0
    g127: LineSegment StartX=41.692 StartY=12.5393 StartZ=0 EndX=41.7679 EndY=12.5393 EndZ=0
    g128: LineSegment StartX=41.7679 StartY=12.5393 StartZ=0 EndX=41.7679 EndY=12.4516 EndZ=0
    g129: LineSegment StartX=41.7679 StartY=12.4516 StartZ=0 EndX=41.8336 EndY=12.4546 EndZ=0
    g130: LineSegment StartX=41.8336 StartY=12.4546 StartZ=0 EndX=41.8336 EndY=12.3903 EndZ=0
    g131: LineSegment StartX=41.8336 StartY=12.3903 StartZ=0 EndX=41.8935 EndY=12.3903 EndZ=0
    g132: LineSegment StartX=41.8935 StartY=12.3903 StartZ=0 EndX=41.8935 EndY=12.3173 EndZ=0
    g133: LineSegment StartX=41.8935 StartY=12.3173 StartZ=0 EndX=41.9592 EndY=12.3217 EndZ=0
    g134: LineSegment StartX=41.9592 StartY=12.3217 StartZ=0 EndX=41.9651 EndY=12.2501 EndZ=0
    g135: LineSegment StartX=41.9651 StartY=12.2501 StartZ=0 EndX=42.0235 EndY=12.2559 EndZ=0
    g136: LineSegment StartX=42.0235 StartY=12.2559 StartZ=0 EndX=42.0264 EndY=12.1829 EndZ=0
    g137: LineSegment StartX=42.0264 StartY=12.1829 StartZ=0 EndX=42.1067 EndY=12.1888 EndZ=0
    g138: LineSegment StartX=42.1067 StartY=12.1888 StartZ=0 EndX=42.1067 EndY=12.1143 EndZ=0
    g139: LineSegment StartX=42.1067 StartY=12.1143 StartZ=0 EndX=42.2426 EndY=12.1216 EndZ=0
    g140: LineSegment StartX=42.2426 StartY=12.1216 StartZ=0 EndX=42.2426 EndY=12.0413 EndZ=0
    g141: LineSegment StartX=42.2426 StartY=12.0413 StartZ=0 EndX=42.4427 EndY=12.0413 EndZ=0
    g142: LineSegment StartX=42.4427 StartY=12.0413 StartZ=0 EndX=42.45 EndY=11.9566 EndZ=0
    g143: LineSegment StartX=42.45 StartY=11.9566 StartZ=0 EndX=42.523 EndY=11.9639 EndZ=0
    g144: LineSegment StartX=42.523 StartY=11.9639 StartZ=0 EndX=42.5274 EndY=11.8952 EndZ=0
    g145: LineSegment StartX=42.5274 StartY=11.8952 StartZ=0 EndX=42.5931 EndY=11.9011 EndZ=0
    g146: LineSegment StartX=42.5931 StartY=11.9011 StartZ=0 EndX=42.5931 EndY=11.847 EndZ=0
    g147: LineSegment StartX=42.5931 StartY=11.847 StartZ=0 EndX=42.6457 EndY=11.8499 EndZ=0
    g148: LineSegment StartX=42.6457 StartY=11.8499 StartZ=0 EndX=42.6457 EndY=11.7886 EndZ=0
    g149: LineSegment StartX=42.6457 StartY=11.7886 StartZ=0 EndX=42.7844 EndY=11.7886 EndZ=0
    g150: LineSegment StartX=42.7844 StartY=11.7886 StartZ=0 EndX=42.7844 EndY=11.7131 EndZ=0
    g151: LineSegment StartX=42.7844 StartY=11.7131 StartZ=0 EndX=43.0642 EndY=11.7131 EndZ=0
    g152: LineSegment StartX=43.0642 StartY=11.7131 StartZ=0 EndX=43.0642 EndY=11.6357 EndZ=0
    g153: LineSegment StartX=43.0642 StartY=11.6357 StartZ=0 EndX=43.1985 EndY=11.6357 EndZ=0
    g154: LineSegment StartX=43.1985 StartY=11.6357 StartZ=0 EndX=43.1985 EndY=11.5714 EndZ=0
    g155: LineSegment StartX=43.1985 StartY=11.5714 StartZ=0 EndX=43.2613 EndY=11.5714 EndZ=0
    g156: LineSegment StartX=43.2613 StartY=11.5714 StartZ=0 EndX=43.2613 EndY=11.5086 EndZ=0
    g157: LineSegment StartX=43.2613 StartY=11.5086 StartZ=0 EndX=43.3285 EndY=11.5086 EndZ=0
    g158: LineSegment StartX=43.3285 StartY=11.5086 StartZ=0 EndX=43.3285 EndY=11.4327 EndZ=0
    g159: LineSegment StartX=43.3285 StartY=11.4327 StartZ=0 EndX=43.3913 EndY=11.4371 EndZ=0
    g160: LineSegment StartX=43.3913 StartY=11.4371 StartZ=0 EndX=43.3932 EndY=11.3717 EndZ=0
    g161: LineSegment StartX=43.3932 StartY=11.3717 StartZ=0 EndX=43.7436 EndY=11.3717 EndZ=0
    g162: LineSegment StartX=43.7436 StartY=11.3717 StartZ=0 EndX=43.7436 EndY=11.3021 EndZ=0
    g163: LineSegment StartX=43.7436 StartY=11.3021 StartZ=0 EndX=43.8098 EndY=11.3021 EndZ=0
    g164: LineSegment StartX=43.8098 StartY=11.3021 StartZ=0 EndX=43.8134 EndY=11.2285 EndZ=0
    g165: LineSegment StartX=43.8134 StartY=11.2285 StartZ=0 EndX=44.0238 EndY=11.2285 EndZ=0
    g166: LineSegment StartX=44.0238 StartY=11.2285 StartZ=0 EndX=44.0238 EndY=11.1603 EndZ=0
    g167: LineSegment StartX=44.0238 StartY=11.1603 StartZ=0 EndX=44.1542 EndY=11.1603 EndZ=0
    g168: LineSegment StartX=44.1542 StartY=11.1603 StartZ=0 EndX=44.1506 EndY=11.0922 EndZ=0
    g169: LineSegment StartX=44.1506 StartY=11.0922 StartZ=0 EndX=44.2845 EndY=11.1005 EndZ=0
    g170: LineSegment StartX=44.2845 StartY=11.1005 StartZ=0 EndX=44.2845 EndY=11.0276 EndZ=0
    g171: LineSegment StartX=44.2845 StartY=11.0276 StartZ=0 EndX=44.3538 EndY=11.0312 EndZ=0
    g172: LineSegment StartX=44.3538 StartY=11.0312 StartZ=0 EndX=44.3538 EndY=10.9534 EndZ=0
    g173: LineSegment StartX=44.3538 StartY=10.9534 StartZ=0 EndX=44.4925 EndY=10.9534 EndZ=0
    g174: LineSegment StartX=44.4925 StartY=10.9534 StartZ=0 EndX=44.4925 EndY=10.9066 EndZ=0
    g175: LineSegment StartX=44.4925 StartY=10.9066 StartZ=0 EndX=44.8405 EndY=10.9066 EndZ=0
    g176: LineSegment StartX=44.8405 StartY=10.9066 StartZ=0 EndX=44.8405 EndY=10.8227 EndZ=0
    g177: LineSegment StartX=44.8405 StartY=10.8227 StartZ=0 EndX=44.9671 EndY=10.8245 EndZ=0
    g178: LineSegment StartX=44.9671 StartY=10.8245 StartZ=0 EndX=44.9671 EndY=10.7496 EndZ=0
    g179: LineSegment StartX=44.9671 StartY=10.7496 StartZ=0 EndX=45.2382 EndY=10.7496 EndZ=0
    g180: LineSegment StartX=45.2382 StartY=10.7496 StartZ=0 EndX=45.2382 EndY=10.6783 EndZ=0
    g181: LineSegment StartX=45.2382 StartY=10.6783 StartZ=0 EndX=45.438 EndY=10.6783 EndZ=0
    g182: LineSegment StartX=45.438 StartY=10.6783 StartZ=0 EndX=45.438 EndY=10.6176 EndZ=0
    g183: LineSegment StartX=45.438 StartY=10.6176 StartZ=0 EndX=45.8572 EndY=10.6176 EndZ=0
    g184: LineSegment StartX=45.8572 StartY=10.6176 StartZ=0 EndX=45.8572 EndY=10.548 EndZ=0
    g185: LineSegment StartX=45.8572 StartY=10.548 StartZ=0 EndX=46.2711 EndY=10.548 EndZ=0
    g186: LineSegment StartX=46.2711 StartY=10.548 StartZ=0 EndX=46.5712 EndY=10.876 EndZ=0
    g187: LineSegment StartX=46.5712 StartY=10.876 StartZ=0 EndX=46.568 EndY=10.9537 EndZ=0
    g188: LineSegment StartX=46.568 StartY=10.9537 StartZ=0 EndX=46.6513 EndY=11.0387 EndZ=0
    g189: LineSegment StartX=46.6513 StartY=11.0387 StartZ=0 EndX=46.6513 EndY=11.2162 EndZ=0
    g190: LineSegment StartX=46.6513 StartY=11.2162 StartZ=0 EndX=46.7535 EndY=11.317 EndZ=0
    g191: LineSegment StartX=46.7535 StartY=11.317 StartZ=0 EndX=46.7462 EndY=11.4353 EndZ=0
    g192: LineSegment StartX=46.7462 StartY=11.4353 StartZ=0 EndX=46.8178 EndY=11.5141 EndZ=0
    g193: LineSegment StartX=46.8178 StartY=11.5141 StartZ=0 EndX=46.8081 EndY=11.636 EndZ=0
    g194: LineSegment StartX=46.8081 StartY=11.636 StartZ=0 EndX=46.8919 EndY=11.7287 EndZ=0
    g195: LineSegment StartX=46.8919 StartY=11.7287 StartZ=0 EndX=46.8919 EndY=11.9142 EndZ=0
    g196: LineSegment StartX=46.8919 StartY=11.9142 StartZ=0 EndX=46.9704 EndY=12.0106 EndZ=0
    g197: LineSegment StartX=46.9704 StartY=12.0106 StartZ=0 EndX=46.9704 EndY=13.0147 EndZ=0
    g198: LineSegment StartX=46.9704 StartY=13.0147 StartZ=0 EndX=47.1435 EndY=13.1957 EndZ=0
    g199: LineSegment StartX=47.1435 StartY=13.1957 StartZ=0 EndX=47.1435 EndY=13.5812 EndZ=0
    g200: LineSegment StartX=47.1435 StartY=13.5812 StartZ=0 EndX=47.0232 EndY=13.5812 EndZ=0
    g201: LineSegment StartX=47.0232 StartY=13.5812 StartZ=0 EndX=47.0232 EndY=13.968 EndZ=0
    g202: LineSegment StartX=47.0232 StartY=13.968 StartZ=0 EndX=46.9387 EndY=13.981 EndZ=0
    g203: LineSegment StartX=46.9387 StartY=13.981 StartZ=0 EndX=46.9387 EndY=14.1923 EndZ=0
    g204: LineSegment StartX=46.9387 StartY=14.1923 StartZ=0 EndX=46.8607 EndY=14.189 EndZ=0
    g205: LineSegment StartX=46.8607 StartY=14.189 StartZ=0 EndX=46.8607 EndY=14.2768 EndZ=0
    g206: LineSegment StartX=46.8607 StartY=14.2768 StartZ=0 EndX=46.9745 EndY=14.4003 EndZ=0
    g207: LineSegment StartX=46.9745 StartY=14.4003 StartZ=0 EndX=46.9842 EndY=14.6473 EndZ=0
    g208: LineSegment StartX=46.9842 StartY=14.6473 StartZ=0 EndX=46.8672 EndY=14.6603 EndZ=0
    g209: LineSegment StartX=46.8672 StartY=14.6603 StartZ=0 EndX=46.8672 EndY=14.8066 EndZ=0
    g210: LineSegment StartX=46.8672 StartY=14.8066 StartZ=0 EndX=46.799 EndY=14.8131 EndZ=0
    g211: LineSegment StartX=46.799 StartY=14.8131 StartZ=0 EndX=46.7957 EndY=14.8846 EndZ=0
    g212: LineSegment StartX=46.7957 StartY=14.8846 StartZ=0 EndX=46.7372 EndY=14.8911 EndZ=0
    g213: LineSegment StartX=46.7372 StartY=14.8911 StartZ=0 EndX=46.7502 EndY=15.0699 EndZ=0
    g214: LineSegment StartX=46.7502 StartY=15.0699 StartZ=0 EndX=46.6592 EndY=15.0764 EndZ=0
    g215: LineSegment StartX=46.6592 StartY=15.0764 StartZ=0 EndX=46.6592 EndY=15.2096 EndZ=0
    g216: LineSegment StartX=46.6592 StartY=15.2096 StartZ=0 EndX=46.7535 EndY=15.2811 EndZ=0
    g217: LineSegment StartX=46.7535 StartY=15.2811 StartZ=0 EndX=47.5498 EndY=15.2811 EndZ=0
    g218: LineSegment StartX=47.5498 StartY=15.2811 StartZ=0 EndX=47.5498 EndY=15.2015 EndZ=0
    g219: LineSegment StartX=47.5498 StartY=15.2015 StartZ=0 EndX=48.1326 EndY=15.2015 EndZ=0
    g220: LineSegment StartX=48.1326 StartY=15.2015 StartZ=0 EndX=48.1915 EndY=15.2887 EndZ=0
    g221: LineSegment StartX=48.1915 StartY=15.2887 StartZ=0 EndX=48.2811 EndY=15.2887 EndZ=0
    g222: LineSegment StartX=48.2811 StartY=15.2887 StartZ=0 EndX=48.4046 EndY=15.4194 EndZ=0
    g223: LineSegment StartX=48.4046 StartY=15.4194 StartZ=0 EndX=48.6512 EndY=15.4194 EndZ=0
    g224: LineSegment StartX=48.6512 StartY=15.4194 StartZ=0 EndX=48.6512 EndY=15.3322 EndZ=0
    g225: LineSegment StartX=48.6512 StartY=15.3322 StartZ=0 EndX=48.9084 EndY=15.3322 EndZ=0
    g226: LineSegment StartX=48.9084 StartY=15.3322 StartZ=0 EndX=48.9084 EndY=15.2647 EndZ=0
    g227: LineSegment StartX=48.9084 StartY=15.2647 StartZ=0 EndX=49.1131 EndY=15.2647 EndZ=0
    g228: LineSegment StartX=49.1131 StartY=15.2647 StartZ=0 EndX=49.1131 EndY=15.171 EndZ=0
    g229: LineSegment StartX=49.1131 StartY=15.171 StartZ=0 EndX=49.344 EndY=15.171 EndZ=0
    g230: LineSegment StartX=49.344 StartY=15.171 StartZ=0 EndX=49.4317 EndY=15.2779 EndZ=0
    g231: LineSegment StartX=49.4317 StartY=15.2779 StartZ=0 EndX=49.513 EndY=15.2714 EndZ=0
    g232: LineSegment StartX=49.513 StartY=15.2714 StartZ=0 EndX=49.6365 EndY=15.4177 EndZ=0
    g233: LineSegment StartX=49.6365 StartY=15.4177 StartZ=0 EndX=51.1609 EndY=15.4177 EndZ=0
    g234: LineSegment StartX=51.1609 StartY=15.4177 StartZ=0 EndX=51.2713 EndY=15.4747 EndZ=0
    g235: LineSegment StartX=51.2713 StartY=15.4747 StartZ=0 EndX=51.8707 EndY=15.4747 EndZ=0
    g236: LineSegment StartX=51.8707 StartY=15.4747 StartZ=0 EndX=51.9501 EndY=15.5501 EndZ=0
    g237: LineSegment StartX=51.9501 StartY=15.5501 StartZ=0 EndX=52.0613 EndY=15.5501 EndZ=0
    g238: LineSegment StartX=52.0613 StartY=15.5501 StartZ=0 EndX=52.1566 EndY=15.6335 EndZ=0
    g239: LineSegment StartX=52.1566 StartY=15.6335 StartZ=0 EndX=53.0776 EndY=15.6335 EndZ=0
    g240: LineSegment StartX=53.0776 StartY=15.6335 StartZ=0 EndX=53.2557 EndY=15.8082 EndZ=0
    g241: LineSegment StartX=53.2557 StartY=15.8082 StartZ=0 EndX=53.2557 EndY=16.103 EndZ=0
    g242: LineSegment StartX=53.2557 StartY=16.103 StartZ=0 EndX=53.1958 EndY=16.103 EndZ=0
    g243: LineSegment StartX=53.1958 StartY=16.103 StartZ=0 EndX=53.1958 EndY=16.3046 EndZ=0
    g244: LineSegment StartX=53.1958 StartY=16.3046 StartZ=0 EndX=53.1301 EndY=16.3017 EndZ=0
    g245: LineSegment StartX=53.1301 StartY=16.3017 StartZ=0 EndX=53.1301 EndY=16.4404 EndZ=0
    g246: LineSegment StartX=53.1301 StartY=16.4404 StartZ=0 EndX=53.0594 EndY=16.4404 EndZ=0
    g247: LineSegment StartX=53.0594 StartY=16.4404 StartZ=0 EndX=53.0558 EndY=16.5171 EndZ=0
    g248: LineSegment StartX=53.0558 StartY=16.5171 StartZ=0 EndX=52.9773 EndY=16.5171 EndZ=0
    g249: LineSegment StartX=52.9773 StartY=16.5171 StartZ=0 EndX=52.9773 EndY=16.6455 EndZ=0
    g250: LineSegment StartX=52.9773 StartY=16.6455 StartZ=0 EndX=52.9219 EndY=16.6452 EndZ=0
    g251: LineSegment StartX=52.9219 StartY=16.6452 StartZ=0 EndX=52.9219 EndY=16.7146 EndZ=0
    g252: LineSegment StartX=52.9219 StartY=16.7146 StartZ=0 EndX=52.8549 EndY=16.7146 EndZ=0
    g253: LineSegment StartX=52.8549 StartY=16.7146 StartZ=0 EndX=52.8535 EndY=16.7863 EndZ=0
    g254: LineSegment StartX=52.8535 StartY=16.7863 StartZ=0 EndX=52.7868 EndY=16.7863 EndZ=0
    g255: LineSegment StartX=52.7868 StartY=16.7863 StartZ=0 EndX=52.7868 EndY=16.9211 EndZ=0
    g256: LineSegment StartX=52.7868 StartY=16.9211 StartZ=0 EndX=52.715 EndY=16.9211 EndZ=0
    g257: LineSegment StartX=52.715 StartY=16.9211 StartZ=0 EndX=52.715 EndY=16.98 EndZ=0
    g258: LineSegment StartX=52.715 StartY=16.98 StartZ=0 EndX=52.6457 EndY=16.98 EndZ=0
    g259: LineSegment StartX=52.6457 StartY=16.98 StartZ=0 EndX=52.6457 EndY=17.0366 EndZ=0
    g260: LineSegment StartX=52.6457 StartY=17.0366 StartZ=0 EndX=52.5763 EndY=17.0366 EndZ=0
    g261: LineSegment StartX=52.5763 StartY=17.0366 StartZ=0 EndX=52.5763 EndY=17.128 EndZ=0
    g262: LineSegment StartX=52.5763 StartY=17.128 StartZ=0 EndX=52.5147 EndY=17.128 EndZ=0
    g263: LineSegment StartX=52.5147 StartY=17.128 StartZ=0 EndX=52.5147 EndY=17.2695 EndZ=0
    g264: LineSegment StartX=52.5147 StartY=17.2695 StartZ=0 EndX=52.4502 EndY=17.2647 EndZ=0
    g265: LineSegment StartX=52.4502 StartY=17.2647 StartZ=0 EndX=52.4454 EndY=17.336 EndZ=0
    g266: LineSegment StartX=52.4454 StartY=17.336 StartZ=0 EndX=52.3797 EndY=17.3384 EndZ=0
    g267: LineSegment StartX=52.3797 StartY=17.3384 StartZ=0 EndX=52.3829 EndY=17.4058 EndZ=0
    g268: LineSegment StartX=52.3829 StartY=17.4058 StartZ=0 EndX=52.318 EndY=17.4026 EndZ=0
    g269: LineSegment StartX=52.318 StartY=17.4026 StartZ=0 EndX=52.318 EndY=17.4715 EndZ=0
    g270: LineSegment StartX=52.318 StartY=17.4715 StartZ=0 EndX=52.2451 EndY=17.4715 EndZ=0
    g271: LineSegment StartX=52.2451 StartY=17.4715 StartZ=0 EndX=52.2451 EndY=17.5364 EndZ=0
    g272: LineSegment StartX=52.2451 StartY=17.5364 StartZ=0 EndX=52.1833 EndY=17.5388 EndZ=0
    g273: LineSegment StartX=52.1833 StartY=17.5388 StartZ=0 EndX=52.1833 EndY=17.6077 EndZ=0
    g274: LineSegment StartX=52.1833 StartY=17.6077 StartZ=0 EndX=52.1144 EndY=17.6077 EndZ=0
    g275: LineSegment StartX=52.1144 StartY=17.6077 StartZ=0 EndX=52.1144 EndY=17.6741 EndZ=0
    g276: LineSegment StartX=52.1144 StartY=17.6741 StartZ=0 EndX=52.0495 EndY=17.6741 EndZ=0
    g277: LineSegment StartX=52.0495 StartY=17.6741 StartZ=0 EndX=52.0495 EndY=17.7495 EndZ=0
    g278: LineSegment StartX=52.0495 StartY=17.7495 StartZ=0 EndX=51.9017 EndY=17.7495 EndZ=0
    g279: LineSegment StartX=51.9017 StartY=17.7495 StartZ=0 EndX=51.9017 EndY=17.8092 EndZ=0
    g280: LineSegment StartX=51.9017 StartY=17.8092 StartZ=0 EndX=51.8351 EndY=17.8092 EndZ=0
    g281: LineSegment StartX=51.8351 StartY=17.8092 StartZ=0 EndX=51.8351 EndY=17.8911 EndZ=0
    g282: LineSegment StartX=51.8351 StartY=17.8911 StartZ=0 EndX=51.7639 EndY=17.8911 EndZ=0
    g283: LineSegment StartX=51.7639 StartY=17.8911 StartZ=0 EndX=51.7639 EndY=17.9626 EndZ=0
    g284: LineSegment StartX=51.7639 StartY=17.9626 StartZ=0 EndX=51.6325 EndY=17.9626 EndZ=0
    g285: LineSegment StartX=51.6325 StartY=17.9626 StartZ=0 EndX=51.6325 EndY=18.0284 EndZ=0
    g286: LineSegment StartX=51.6325 StartY=18.0284 StartZ=0 EndX=51.485 EndY=18.0284 EndZ=0
    g287: LineSegment StartX=51.485 StartY=18.0284 StartZ=0 EndX=51.485 EndY=18.0711 EndZ=0
    g288: LineSegment StartX=51.485 StartY=18.0711 StartZ=0 EndX=51.4163 EndY=18.0711 EndZ=0
    g289: LineSegment StartX=51.4163 StartY=18.0711 StartZ=0 EndX=51.4163 EndY=18.1587 EndZ=0
    g290: LineSegment StartX=51.4163 StartY=18.1587 StartZ=0 EndX=51.2878 EndY=18.1587 EndZ=0
    g291: LineSegment StartX=51.2878 StartY=18.1587 StartZ=0 EndX=51.2878 EndY=18.2275 EndZ=0
    g292: LineSegment StartX=51.2878 StartY=18.2275 StartZ=0 EndX=51.2232 EndY=18.2275 EndZ=0
    g293: LineSegment StartX=51.2232 StartY=18.2275 StartZ=0 EndX=51.2267 EndY=18.2921 EndZ=0
    g294: LineSegment StartX=51.2267 StartY=18.2921 StartZ=0 EndX=51.1526 EndY=18.2921 EndZ=0
    g295: LineSegment StartX=51.1526 StartY=18.2921 StartZ=0 EndX=51.1526 EndY=18.3662 EndZ=0
    g296: LineSegment StartX=51.1526 StartY=18.3662 StartZ=0 EndX=51.0845 EndY=18.3602 EndZ=0
    g297: LineSegment StartX=51.0845 StartY=18.3602 StartZ=0 EndX=51.0845 EndY=18.4424 EndZ=0
    g298: LineSegment StartX=51.0845 StartY=18.4424 StartZ=0 EndX=51.0222 EndY=18.4424 EndZ=0
    g299: LineSegment StartX=51.0222 StartY=18.4424 StartZ=0 EndX=51.0222 EndY=18.5138 EndZ=0
    g300: LineSegment StartX=51.0222 StartY=18.5138 StartZ=0 EndX=50.8169 EndY=18.5138 EndZ=0
    g301: LineSegment StartX=50.8169 StartY=18.5138 StartZ=0 EndX=50.7878 EndY=18.6026 EndZ=0
    g302: LineSegment StartX=50.7878 StartY=18.6026 StartZ=0 EndX=50.7494 EndY=18.6113 EndZ=0
    g303: LineSegment StartX=50.7494 StartY=18.6113 StartZ=0 EndX=50.7397 EndY=18.6731 EndZ=0
    g304: LineSegment StartX=50.7397 StartY=18.6731 StartZ=0 EndX=50.5414 EndY=18.6536 EndZ=0
    g305: LineSegment StartX=50.5414 StartY=18.6536 StartZ=0 EndX=50.5381 EndY=18.7381 EndZ=0
    g306: LineSegment StartX=50.5381 StartY=18.7381 StartZ=0 EndX=50.4114 EndY=18.7218 EndZ=0
    g307: LineSegment StartX=50.4114 StartY=18.7218 StartZ=0 EndX=50.3951 EndY=18.7934 EndZ=0
    g308: LineSegment StartX=50.3951 StartY=18.7934 StartZ=0 EndX=50.3334 EndY=18.7934 EndZ=0
    g309: LineSegment StartX=50.3334 StartY=18.7934 StartZ=0 EndX=50.3366 EndY=18.8389 EndZ=0
    g310: LineSegment StartX=50.3366 StartY=18.8389 StartZ=0 EndX=50.2066 EndY=18.8389 EndZ=0
    g311: LineSegment StartX=50.2066 StartY=18.8389 StartZ=0 EndX=50.2099 EndY=18.9201 EndZ=0
    g312: LineSegment StartX=50.2099 StartY=18.9201 StartZ=0 EndX=50.1254 EndY=18.9266 EndZ=0
    g313: LineSegment StartX=50.1254 StartY=18.9266 StartZ=0 EndX=50.1156 EndY=19.0046 EndZ=0
    g314: LineSegment StartX=50.1156 StartY=19.0046 StartZ=0 EndX=49.9986 EndY=18.9949 EndZ=0
    g315: LineSegment StartX=49.9986 StartY=18.9949 StartZ=0 EndX=49.9921 EndY=19.0859 EndZ=0
    g316: LineSegment StartX=49.9921 StartY=19.0859 StartZ=0 EndX=49.9368 EndY=19.0501 EndZ=0
    g317: LineSegment StartX=49.9368 StartY=19.0501 StartZ=0 EndX=49.9206 EndY=19.1509 EndZ=0
    g318: LineSegment StartX=49.9206 StartY=19.1509 StartZ=0 EndX=49.7971 EndY=19.1281 EndZ=0
    g319: LineSegment StartX=49.7971 StartY=19.1281 StartZ=0 EndX=49.8068 EndY=19.2029 EndZ=0
    g320: LineSegment StartX=49.8068 StartY=19.2029 StartZ=0 EndX=49.7288 EndY=19.1899 EndZ=0
    g321: LineSegment StartX=49.7288 StartY=19.1899 StartZ=0 EndX=49.7191 EndY=19.2582 EndZ=0
    g322: LineSegment StartX=49.7191 StartY=19.2582 StartZ=0 EndX=49.6606 EndY=19.2647 EndZ=0
    g323: LineSegment StartX=49.6606 StartY=19.2647 StartZ=0 EndX=49.6541 EndY=19.3329 EndZ=0
    g324: LineSegment StartX=49.6541 StartY=19.3329 StartZ=0 EndX=49.6021 EndY=19.3329 EndZ=0
    g325: LineSegment StartX=49.6021 StartY=19.3329 StartZ=0 EndX=49.5988 EndY=19.4077 EndZ=0
    g326: LineSegment StartX=49.5988 StartY=19.4077 StartZ=0 EndX=49.4623 EndY=19.3947 EndZ=0
    g327: LineSegment StartX=49.4623 StartY=19.3947 StartZ=0 EndX=49.4623 EndY=19.4727 EndZ=0
    g328: LineSegment StartX=49.4623 StartY=19.4727 StartZ=0 EndX=49.2543 EndY=19.4532 EndZ=0
    g329: LineSegment StartX=49.2543 StartY=19.4532 StartZ=0 EndX=49.2543 EndY=19.5279 EndZ=0
    g330: LineSegment StartX=49.2543 StartY=19.5279 StartZ=0 EndX=49.199 EndY=19.5279 EndZ=0
    g331: LineSegment StartX=49.199 StartY=19.5279 StartZ=0 EndX=49.199 EndY=19.6189 EndZ=0
    g332: LineSegment StartX=49.199 StartY=19.6189 StartZ=0 EndX=49.0658 EndY=19.6059 EndZ=0
    g333: LineSegment StartX=49.0658 StartY=19.6059 StartZ=0 EndX=49.0495 EndY=19.6612 EndZ=0
    g334: LineSegment StartX=49.0495 StartY=19.6612 StartZ=0 EndX=48.991 EndY=19.6547 EndZ=0
    g335: LineSegment StartX=48.991 StartY=19.6547 StartZ=0 EndX=48.9845 EndY=19.7359 EndZ=0
    g336: LineSegment StartX=48.9845 StartY=19.7359 StartZ=0 EndX=48.8577 EndY=19.7262 EndZ=0
    g337: LineSegment StartX=48.8577 StartY=19.7262 StartZ=0 EndX=48.8577 EndY=19.8149 EndZ=0
    g338: LineSegment StartX=48.8577 StartY=19.8149 StartZ=0 EndX=48.7743 EndY=19.8069 EndZ=0
    g339: LineSegment StartX=48.7743 StartY=19.8069 StartZ=0 EndX=48.7743 EndY=19.8894 EndZ=0
    g340: LineSegment StartX=48.7743 StartY=19.8894 StartZ=0 EndX=48.5854 EndY=19.8894 EndZ=0
    g341: LineSegment StartX=48.5854 StartY=19.8894 StartZ=0 EndX=48.5854 EndY=19.9533 EndZ=0
    g342: LineSegment StartX=48.5854 StartY=19.9533 StartZ=0 EndX=48.4417 EndY=19.9533 EndZ=0
    g343: LineSegment StartX=48.4417 StartY=19.9533 StartZ=0 EndX=48.4417 EndY=20.0118 EndZ=0
    g344: LineSegment StartX=48.4417 StartY=20.0118 StartZ=0 EndX=48.3751 EndY=20.0118 EndZ=0
    g345: LineSegment StartX=48.3751 StartY=20.0118 StartZ=0 EndX=48.3751 EndY=20.089 EndZ=0
    g346: LineSegment StartX=48.3751 StartY=20.089 StartZ=0 EndX=48.3033 EndY=20.089 EndZ=0
    g347: LineSegment StartX=48.3033 StartY=20.089 StartZ=0 EndX=48.3033 EndY=20.1524 EndZ=0
    g348: LineSegment StartX=48.3033 StartY=20.1524 StartZ=0 EndX=48.0916 EndY=20.1524 EndZ=0
    g349: LineSegment StartX=48.0916 StartY=20.1524 StartZ=0 EndX=48.0916 EndY=20.2331 EndZ=0
    g350: LineSegment StartX=48.0916 StartY=20.2331 StartZ=0 EndX=47.8912 EndY=20.2331 EndZ=0
    g351: LineSegment StartX=47.8912 StartY=20.2331 StartZ=0 EndX=47.8912 EndY=20.2962 EndZ=0
    g352: LineSegment StartX=47.8912 StartY=20.2962 StartZ=0 EndX=47.6864 EndY=20.2962 EndZ=0
    g353: LineSegment StartX=47.6864 StartY=20.2962 StartZ=0 EndX=47.6864 EndY=20.3681 EndZ=0
    g354: LineSegment StartX=47.6864 StartY=20.3681 StartZ=0 EndX=47.2898 EndY=20.3681 EndZ=0
    g355: LineSegment StartX=47.2898 StartY=20.3681 StartZ=0 EndX=47.2898 EndY=20.4313 EndZ=0
    g356: LineSegment StartX=47.2898 StartY=20.4313 StartZ=0 EndX=47.0094 EndY=20.4313 EndZ=0
    g357: LineSegment StartX=47.0094 StartY=20.4313 StartZ=0 EndX=47.0094 EndY=20.5033 EndZ=0
    g358: LineSegment StartX=47.0094 StartY=20.5033 StartZ=0 EndX=46.7265 EndY=20.5033 EndZ=0
    g359: LineSegment StartX=46.7265 StartY=20.5033 StartZ=0 EndX=46.7265 EndY=20.5623 EndZ=0
    g360: LineSegment StartX=46.7265 StartY=20.5623 StartZ=0 EndX=46.3195 EndY=20.5623 EndZ=0
    g361: LineSegment StartX=46.3195 StartY=20.5623 StartZ=0 EndX=46.2304 EndY=20.478 EndZ=0
    g362: LineSegment StartX=46.2304 StartY=20.478 StartZ=0 EndX=45.8403 EndY=20.478 EndZ=0
    g363: LineSegment StartX=45.8403 StartY=20.478 StartZ=0 EndX=45.7581 EndY=20.3987 EndZ=0
    g364: LineSegment StartX=45.7581 StartY=20.3987 StartZ=0 EndX=45.6847 EndY=20.3987 EndZ=0
    g365: LineSegment StartX=45.6847 StartY=20.3987 StartZ=0 EndX=45.6847 EndY=20.4757 EndZ=0
    g366: LineSegment StartX=45.6847 StartY=20.4757 StartZ=0 EndX=45.2353 EndY=20.4757 EndZ=0
    g367: LineSegment StartX=45.2353 StartY=20.4757 StartZ=0 EndX=45.1511 EndY=20.3964 EndZ=0
    g368: LineSegment StartX=45.1511 StartY=20.3964 StartZ=0 EndX=45.039 EndY=20.3905 EndZ=0
    g369: LineSegment StartX=45.1271 StartY=20.498 StartZ=0 EndX=45.039 EndY=20.3905 EndZ=0
    g370: LineSegment StartX=45.1271 StartY=20.498 StartZ=0 EndX=45.1672 EndY=20.498 EndZ=0
    g371: LineSegment StartX=45.1672 StartY=20.498 StartZ=0 EndX=45.2586 EndY=20.5605 EndZ=0
    g372: LineSegment StartX=45.2586 StartY=20.5605 StartZ=0 EndX=45.3242 EndY=20.5605 EndZ=0
    g373: LineSegment StartX=45.3242 StartY=20.5605 StartZ=0 EndX=45.4009 EndY=20.6461 EndZ=0
    g374: LineSegment StartX=45.4009 StartY=20.6461 StartZ=0 EndX=45.5221 EndY=20.6461 EndZ=0
    g375: LineSegment StartX=45.5221 StartY=20.6461 StartZ=0 EndX=45.6149 EndY=20.705 EndZ=0
    g376: LineSegment StartX=45.6149 StartY=20.705 StartZ=0 EndX=45.8042 EndY=20.705 EndZ=0
    g377: LineSegment StartX=45.8042 StartY=20.705 StartZ=0 EndX=45.9915 EndY=20.8898 EndZ=0
    g378: LineSegment StartX=45.9915 StartY=20.8898 StartZ=0 EndX=45.9915 EndY=20.959 EndZ=0
    g379: LineSegment StartX=45.9915 StartY=20.959 StartZ=0 EndX=46.0581 EndY=21.0202 EndZ=0
    g380: LineSegment StartX=46.0581 StartY=21.0202 StartZ=0 EndX=46.0527 EndY=21.0894 EndZ=0
    g381: LineSegment StartX=46.0527 StartY=21.0894 StartZ=0 EndX=46.2124 EndY=21.2464 EndZ=0
    g382: LineSegment StartX=46.2124 StartY=21.2464 StartZ=0 EndX=46.2763 EndY=21.2277 EndZ=0
    g383: LineSegment StartX=46.2763 StartY=21.2277 StartZ=0 EndX=46.5051 EndY=21.4486 EndZ=0
    g384: LineSegment StartX=46.5051 StartY=21.4486 StartZ=0 EndX=46.585 EndY=21.4539 EndZ=0
    g385: LineSegment StartX=46.585 StartY=21.4539 StartZ=0 EndX=46.6994 EndY=21.603 EndZ=0
    g386: LineSegment StartX=46.6994 StartY=21.603 StartZ=0 EndX=46.8245 EndY=21.5843 EndZ=0
    g387: LineSegment StartX=46.8245 StartY=21.5843 StartZ=0 EndX=46.9016 EndY=21.6855 EndZ=0
    g388: LineSegment StartX=46.9016 StartY=21.6855 StartZ=0 EndX=46.9655 EndY=21.6562 EndZ=0
    g389: LineSegment StartX=46.9655 StartY=21.6562 StartZ=0 EndX=47.205 EndY=21.8754 EndZ=0
    g390: LineSegment StartX=47.205 StartY=21.8754 StartZ=0 EndX=47.205 EndY=22.0711 EndZ=0
    g391: LineSegment StartX=47.205 StartY=22.0711 StartZ=0 EndX=47.2634 EndY=22.0711 EndZ=0
    g392: LineSegment StartX=47.2634 StartY=22.0711 StartZ=0 EndX=47.6208 EndY=22.4458 EndZ=0
    g393: LineSegment StartX=47.6208 StartY=22.4458 StartZ=0 EndX=47.6208 EndY=22.5177 EndZ=0
    g394: LineSegment StartX=47.6208 StartY=22.5177 StartZ=0 EndX=47.8212 EndY=22.7182 EndZ=0
    g395: LineSegment StartX=47.8212 StartY=22.7182 StartZ=0 EndX=47.8343 EndY=22.7944 EndZ=0
    g396: LineSegment StartX=47.8343 StartY=22.7944 StartZ=0 EndX=48.0478 EndY=22.997 EndZ=0
    g397: LineSegment StartX=48.0478 StartY=22.997 StartZ=0 EndX=48.0478 EndY=23.1365 EndZ=0
    g398: LineSegment StartX=48.0478 StartY=23.1365 StartZ=0 EndX=48.0998 EndY=23.2173 EndZ=0
    g399: LineSegment StartX=48.0998 StartY=23.2173 StartZ=0 EndX=48.0998 EndY=23.2802 EndZ=0
    ... +484 more geometry lines
  constraints (1492):
    c: Coincident(g3,g2)
    c: Vertical(g4)
    c: Vertical(g6)
    c: Coincident(g8,g7)
    c: Vertical(g8)
    c: Coincident(g8,g9)
    c: Coincident(g9,g10)
    c: Vertical(g10)
    c: Coincident(g10,g11)
    c: Coincident(g11,g12)
    c: Vertical(g12)
    c: Coincident(g13,g12)
    c: Horizontal(g13)
    c: Vertical(g14)
    c: Coincident(g16,g15)
    c: Vertical(g16)
    c: Horizontal(g17)
    c: Coincident(g18,g17)
    c: Vertical(g18)
    c: Horizontal(g19)
    c: Coincident(g20,g19)
    c: Vertical(g20)
    c: Horizontal(g21)
    c: Vertical(g22)
    c: Horizontal(g23)
    c: Coincident(g24,g23)
    c: Vertical(g24)
    c: Horizontal(g25)
    c: Coincident(g27,g26)
    c: Horizontal(g27)
    c: Vertical(g28)
    c: Coincident(g30,g29)
    c: Vertical(g30)
    c: Coincident(g31,g32)
    c: Vertical(g32)
    c: Coincident(g32,g33)
    c: Horizontal(g33)
    c: Coincident(g34,g33)
    c: Vertical(g34)
    c: Coincident(g35,g34)
    c: Horizontal(g35)
    c: Coincident(g36,g35)
    c: Vertical(g36)
    c: Coincident(g37,g36)
    c: Horizontal(g37)
    c: Vertical(g38)
    c: Horizontal(g39)
    c: Vertical(g40)
    c: Horizontal(g41)
    c: Coincident(g42,g41)
    c: Vertical(g42)
    c: Horizontal(g43)
    c: Coincident(g44,g43)
    c: Vertical(g44)
    c: Coincident(g45,g44)
    c: Horizontal(g45)
    c: Coincident(g46,g45)
    c: Vertical(g46)
    c: Coincident(g47,g46)
    c: Horizontal(g47)
    c: Coincident(g48,g47)
    c: Vertical(g48)
    c: Horizontal(g49)
    c: Vertical(g50)
    c: Coincident(g51,g50)
    c: Horizontal(g51)
    c: Vertical(g52)
    c: Coincident(g53,g52)
    c: Horizontal(g53)
    c: Coincident(g54,g53)
    c: Vertical(g54)
    c: Coincident(g55,g54)
    c: Horizontal(g55)
    c: Coincident(g56,g55)
    c: Vertical(g56)
    c: Coincident(g57,g56)
    c: Horizontal(g57)
    c: Coincident(g58,g57)
    c: Vertical(g58)
    c: Coincident(g60,g59)
    c: Vertical(g60)
    c: Coincident(g61,g60)
    c: Horizontal(g61)
    c: Vertical(g62)
    c: Horizontal(g63)
    c: Coincident(g64,g63)
    c: Vertical(g64)
    c: Horizontal(g65)
    c: Vertical(g66)
    c: Coincident(g68,g67)
    c: Vertical(g68)
    c: Horizontal(g69)
    c: Coincident(g70,g69)
    c: Vertical(g70)
    c: Horizontal(g71)
    c: Coincident(g72,g71)
    c: Vertical(g72)
    c: Horizontal(g73)
    c: Coincident(g74,g73)
    c: Vertical(g74)
    c: Horizontal(g75)
    c: Coincident(g76,g75)
    c: Vertical(g76)
    c: Horizontal(g77)
    c: Vertical(g78)
    c: Coincident(g79,g78)
    c: Coincident(g80,g79)
    c: Vertical(g80)
    c: Coincident(g81,g80)
    c: Coincident(g82,g81)
    c: Horizontal(g83)
    c: Coincident(g85,g84)
    c: Horizontal(g85)
    c: Coincident(g86,g85)
    c: Coincident(g89,g88)
    c: Horizontal(g89)
    c: Coincident(g90,g89)
    c: Coincident(g91,g90)
    c: Horizontal(g91)
    c: Coincident(g92,g91)
    c: Horizontal(g93)
    c: Coincident(g94,g93)
    c: Horizontal(g95)
    c: Coincident(g96,g95)
    c: Coincident(g97,g98)
    c: Coincident(g98,g99)
    c: Vertical(g99)
    c: Coincident(g99,g100)
    c: Coincident(g100,g101)
    c: Coincident(g101,g102)
    c: Coincident(g102,g103)
    c: Coincident(g103,g104)
    c: Coincident(g104,g105)
    c: Vertical(g105)
    c: Coincident(g105,g106)
    c: Coincident(g106,g107)
    c: Coincident(g107,g108)
    c: Horizontal(g108)
    c: Coincident(g108,g109)
    c: Coincident(g109,g110)
    c: Vertical(g110)
    c: Coincident(g110,g111)
    c: Coincident(g111,g112)
    c: Coincident(g112,g113)
    c: Coincident(g113,g114)
    c: Coincident(g114,g115)
    c: Coincident(g115,g116)
    c: Vertical(g116)
    c: Coincident(g116,g117)
    c: Coincident(g117,g118)
    c: Coincident(g118,g119)
    c: Coincident(g119,g120)
    c: Coincident(g120,g121)
    c: Horizontal(g121)
    c: Coincident(g121,g122)
    c: Coincident(g122,g123)
    c: Coincident(g123,g124)
    c: Coincident(g124,g125)
    c: Vertical(g125)
    c: Coincident(g125,g126)
    c: Coincident(g126,g127)
    c: Horizontal(g127)
    c: Coincident(g127,g128)
    c: Vertical(g128)
    c: Coincident(g128,g129)
    c: Coincident(g129,g130)
    c: Vertical(g130)
    c: Coincident(g130,g131)
    c: Horizontal(g131)
    c: Coincident(g131,g132)
    c: Vertical(g132)
    c: Coincident(g132,g133)
    c: Coincident(g133,g134)
    c: Coincident(g134,g135)
    c: Coincident(g135,g136)
    c: Coincident(g136,g137)
    c: Coincident(g137,g138)
    c: Vertical(g138)
    c: Coincident(g138,g139)
    c: Coincident(g139,g140)
    c: Vertical(g140)
    c: Coincident(g140,g141)
    c: Horizontal(g141)
    c: Coincident(g141,g142)
    c: Coincident(g142,g143)
    c: Coincident(g143,g144)
    c: Coincident(g144,g145)
    c: Coincident(g145,g146)
    c: Vertical(g146)
    c: Coincident(g146,g147)
    c: Coincident(g147,g148)
    c: Vertical(g148)
    c: Coincident(g148,g149)
    c: Horizontal(g149)
    c: Coincident(g149,g150)
    c: Vertical(g150)
    c: Coincident(g150,g151)
    c: Horizontal(g151)
    c: Coincident(g151,g152)
    c: Vertical(g152)
    c: Coincident(g152,g153)
    c: Horizontal(g153)
    c: Coincident(g153,g154)
    c: Vertical(g154)
    c: Coincident(g154,g155)
    c: Horizontal(g155)
    c: Coincident(g155,g156)
    c: Vertical(g156)
    c: Coincident(g156,g157)
    c: Horizontal(g157)
    c: Coincident(g157,g158)
    c: Vertical(g158)
    c: Coincident(g158,g159)
    c: Coincident(g159,g160)
    c: Coincident(g160,g161)
    c: Horizontal(g161)
    c: Coincident(g161,g162)
    c: Vertical(g162)
    c: Coincident(g162,g163)
    c: Horizontal(g163)
    c: Coincident(g163,g164)
    c: Coincident(g164,g165)
    c: Horizontal(g165)
    c: Coincident(g165,g166)
    c: Vertical(g166)
    c: Coincident(g166,g167)
    c: Horizontal(g167)
    c: Coincident(g167,g168)
    c: Coincident(g168,g169)
    c: Coincident(g169,g170)
    c: Vertical(g170)
    c: Coincident(g170,g171)
    c: Coincident(g171,g172)
    c: Vertical(g172)
    c: Coincident(g172,g173)
    c: Horizontal(g173)
    c: Coincident(g173,g174)
    c: Vertical(g174)
    c: Coincident(g174,g175)
    c: Horizontal(g175)
    c: Coincident(g175,g176)
    c: Vertical(g176)
    c: Coincident(g176,g177)
    c: Coincident(g177,g178)
    c: Vertical(g178)
    c: Coincident(g178,g179)
    c: Horizontal(g179)
    c: Coincident(g179,g180)
    c: Vertical(g180)
    c: Coincident(g180,g181)
    c: Horizontal(g181)
    c: Coincident(g181,g182)
    c: Vertical(g182)
    c: Coincident(g182,g183)
    c: Horizontal(g183)
    c: Coincident(g183,g184)
    c: Vertical(g184)
    c: Coincident(g184,g185)
    c: Horizontal(g185)
    c: Coincident(g185,g186)
    c: Coincident(g186,g187)
    c: Coincident(g187,g188)
    c: Coincident(g188,g189)
    c: Vertical(g189)
    c: Coincident(g189,g190)
    c: Coincident(g190,g191)
    c: Coincident(g191,g192)
    c: Coincident(g192,g193)
    c: Coincident(g193,g194)
    c: Coincident(g194,g195)
    c: Vertical(g195)
    c: Coincident(g195,g196)
    c: Coincident(g196,g197)
    c: Vertical(g197)
    c: Coincident(g197,g198)
    c: Coincident(g198,g199)
    c: Vertical(g199)
    c: Coincident(g199,g200)
    c: Coincident(g200,g201)
    c: Vertical(g201)
    c: Coincident(g201,g202)
    c: Coincident(g202,g203)
    c: Vertical(g203)
    c: Coincident(g203,g204)
    c: Coincident(g204,g205)
    c: Vertical(g205)
    c: Coincident(g205,g206)
    c: Coincident(g206,g207)
    c: Coincident(g207,g208)
    c: Coincident(g208,g209)
    c: Vertical(g209)
    c: Coincident(g209,g210)
    c: Coincident(g210,g211)
    c: Coincident(g211,g212)
    c: Coincident(g212,g213)
    c: Coincident(g213,g214)
    c: Coincident(g214,g215)
    c: Vertical(g215)
    c: Coincident(g215,g216)
    c: Coincident(g216,g217)
    c: Horizontal(g217)
    c: Coincident(g217,g218)
    c: Vertical(g218)
    c: Coincident(g218,g219)
    c: Horizontal(g219)
    c: Coincident(g219,g220)
    c: Coincident(g220,g221)
    c: Horizontal(g221)
    c: Coincident(g221,g222)
    c: Coincident(g222,g223)
    c: Horizontal(g223)
    c: Coincident(g223,g224)
    c: Coincident(g224,g225)
    c: Horizontal(g225)
    c: Coincident(g225,g226)
    c: Vertical(g226)
    c: Coincident(g226,g227)
    c: Horizontal(g227)
    c: Coincident(g227,g228)
    c: Vertical(g228)
    c: Coincident(g228,g229)
    c: Horizontal(g229)
    c: Coincident(g229,g230)
    c: Coincident(g230,g231)
    c: Coincident(g231,g232)
    c: Coincident(g232,g233)
    c: Horizontal(g233)
    c: Coincident(g233,g234)
    c: Coincident(g234,g235)
    c: Horizontal(g235)
    c: Coincident(g235,g236)
    c: Coincident(g236,g237)
    c: Horizontal(g237)
    c: Coincident(g237,g238)
    c: Coincident(g238,g239)
    c: Horizontal(g239)
    c: Coincident(g239,g240)
    c: Coincident(g240,g241)
    c: Vertical(g241)
    c: Coincident(g241,g242)
    c: Horizontal(g242)
    c: Coincident(g242,g243)
    c: Vertical(g243)
    c: Coincident(g243,g244)
    c: Coincident(g244,g245)
    c: Vertical(g245)
    c: Coincident(g245,g246)
    c: Horizontal(g246)
    c: Coincident(g246,g247)
    c: Coincident(g247,g248)
    c: Horizontal(g248)
    c: Coincident(g248,g249)
    c: Vertical(g249)
    c: Coincident(g249,g250)
    c: Coincident(g250,g251)
    c: Coincident(g251,g252)
    c: Horizontal(g252)
    c: Coincident(g252,g253)
    c: Coincident(g253,g254)
    c: Horizontal(g254)
    c: Coincident(g254,g255)
    c: Vertical(g255)
    c: Coincident(g255,g256)
    c: Coincident(g256,g257)
    c: Coincident(g257,g258)
    c: Coincident(g258,g259)
    c: Coincident(g259,g260)
    c: Coincident(g260,g261)
    c: Vertical(g257)
    c: Horizontal(g258)
    c: Horizontal(g256)
    c: Vertical(g259)
    c: Horizontal(g260)
    c: Vertical(g261)
    c: Coincident(g261,g262)
    c: Horizontal(g262)
    c: Coincident(g262,g263)
    c: Vertical(g263)
    c: Coincident(g263,g264)
    c: Coincident(g264,g265)
    c: Coincident(g265,g266)
    c: Coincident(g266,g267)
    c: Coincident(g267,g268)
    c: Coincident(g268,g269)
    c: Vertical(g269)
    c: Coincident(g269,g270)
    c: Horizontal(g270)
    c: Coincident(g270,g271)
    c: Vertical(g271)
    c: Coincident(g271,g272)
    c: Coincident(g272,g273)
    c: Vertical(g273)
    c: Coincident(g273,g274)
    c: Horizontal(g274)
    c: Coincident(g274,g275)
    c: Vertical(g275)
    c: Coincident(g275,g276)
    c: Horizontal(g276)
    c: Coincident(g276,g277)
    c: Coincident(g277,g278)
    c: Horizontal(g278)
    c: Coincident(g278,g279)
    c: Coincident(g279,g280)
    c: Coincident(g280,g281)
    c: Vertical(g281)
    c: Coincident(g281,g282)
    c: Coincident(g282,g283)
    c: Coincident(g283,g284)
    c: Horizontal(g284)
    c: Coincident(g284,g285)
    c: Coincident(g285,g286)
    c: Coincident(g286,g287)
    c: Coincident(g287,g288)
    c: Coincident(g288,g289)
    c: Coincident(g289,g290)
    c: Coincident(g290,g291)
    c: Vertical(g291)
    c: Coincident(g291,g292)
    c: Horizontal(g292)
    c: Coincident(g292,g293)
    c: Coincident(g293,g294)
    c: Horizontal(g294)
    c: Coincident(g294,g295)
    c: Vertical(g295)
    c: Coincident(g295,g296)
    c: Coincident(g296,g297)
    c: Vertical(g297)
    c: Coincident(g297,g298)
    c: Horizontal(g298)
    c: Coincident(g298,g299)
    c: Vertical(g299)
    c: Coincident(g299,g300)
    c: Horizontal(g300)
    c: Coincident(g300,g301)
    c: Coincident(g301,g302)
    c: Coincident(g302,g303)
    c: Coincident(g303,g304)
    c: Coincident(g304,g305)
    c: Coincident(g305,g306)
    c: Coincident(g306,g307)
    c: Coincident(g307,g308)
    c: Horizontal(g308)
    c: Coincident(g308,g309)
    c: Coincident(g309,g310)
    c: Horizontal(g310)
    c: Coincident(g310,g311)
    c: Coincident(g311,g312)
    c: Coincident(g312,g313)
    c: Coincident(g313,g314)
    c: Coincident(g314,g315)
    c: Coincident(g315,g316)
    c: Coincident(g316,g317)
    c: Coincident(g317,g318)
    c: Coincident(g318,g319)
    c: Coincident(g319,g320)
    c: Coincident(g320,g321)
    c: Coincident(g321,g322)
    c: Coincident(g322,g323)
    c: Coincident(g323,g324)
    c: Horizontal(g324)
    c: Coincident(g324,g325)
    c: Coincident(g325,g326)
    c: Coincident(g326,g327)
    c: Vertical(g327)
    c: Coincident(g327,g328)
    c: Coincident(g328,g329)
    c: Coincident(g329,g330)
    c: Coincident(g330,g331)
    c: Vertical(g331)
    c: Coincident(g331,g332)
    c: Coincident(g332,g333)
    c: Coincident(g333,g334)
    c: Coincident(g334,g335)
    c: Coincident(g335,g336)
    c: Coincident(g336,g337)
    c: Vertical(g337)
    c: Coincident(g337,g338)
    c: Coincident(g338,g339)
    c: Coincident(g339,g340)
    c: Coincident(g340,g341)
    c: Coincident(g341,g342)
    c: Coincident(g342,g343)
    c: Coincident(g343,g344)
    c: Coincident(g344,g345)
    c: Coincident(g345,g346)
    c: Coincident(g346,g347)
    c: Coincident(g347,g348)
    c: Coincident(g348,g349)
    c: Coincident(g349,g350)
    c: Coincident(g350,g351)
    c: Coincident(g351,g352)
    c: Coincident(g352,g353)
    c: Coincident(g353,g354)
    c: Coincident(g354,g355)
    c: Coincident(g355,g356)
    c: Coincident(g356,g357)
    c: Vertical(g357)
    c: Coincident(g357,g358)
    c: Horizontal(g358)
    c: Coincident(g358,g359)
    c: Coincident(g359,g360)
    c: Coincident(g360,g361)
    c: Coincident(g361,g362)
    c: Horizontal(g362)
    c: Coincident(g362,g363)
    c: Coincident(g363,g364)
    c: Coincident(g364,g365)
    c: Coincident(g365,g366)
    c: Coincident(g366,g367)
    c: Horizontal(g290)
    c: Vertical(g287)
    c: Vertical(g285)
    c: Vertical(g283)
    c: Vertical(g279)
    c: Vertical(g277)
    c: Horizontal(g286)
    c: Horizontal(g288)
    c: Vertical(g289)
    c: Horizontal(g280)
    c: Horizontal(g282)
    c: Vertical(g329)
    c: Horizontal(g330)
    c: Horizontal(g340)
    c: Horizontal(g342)
    c: Horizontal(g344)
    c: Horizontal(g346)
    c: Horizontal(g348)
    c: Horizontal(g350)
    c: Vertical(g339)
    c: Vertical(g341)
    c: Vertical(g343)
    c: Vertical(g345)
    c: Vertical(g347)
    c: Vertical(g349)
    c: Vertical(g351)
    c: Vertical(g353)
    c: Vertical(g355)
    c: Horizontal(g352)
    c: Horizontal(g354)
    c: Horizontal(g356)
    c: Vertical(g359)
    c: Horizontal(g360)
    c: Horizontal(g364)
    c: Vertical(g365)
    c: Horizontal(g366)
    c: Coincident(g368,g367)
    c: Coincident(g369,g368)
    c: Coincident(g369,g370)
    c: Coincident(g370,g371)
    c: Coincident(g371,g372)
    c: Horizontal(g372)
    c: Coincident(g372,g373)
    c: Coincident(g373,g374)
    c: Coincident(g374,g375)
    c: Coincident(g375,g376)
    c: Coincident(g376,g377)
    c: Coincident(g377,g378)
    c: Vertical(g378)
    c: Coincident(g378,g379)
    c: Coincident(g379,g380)
    c: Coincident(g380,g381)
    c: Coincident(g381,g382)
    c: Coincident(g382,g383)
    c: Coincident(g383,g384)
    c: Coincident(g384,g385)
    c: Coincident(g385,g386)
    c: Coincident(g386,g387)
    c: Coincident(g387,g388)
    c: Coincident(g388,g389)
    c: Coincident(g389,g390)
    c: Coincident(g390,g391)
    c: Horizontal(g391)
    c: Coincident(g391,g392)
    c: Coincident(g392,g393)
    c: Coincident(g393,g394)
    c: Coincident(g394,g395)
    c: Coincident(g395,g396)
    c: Coincident(g396,g397)
    c: Coincident(g397,g398)
    c: Coincident(g398,g399)
    c: Coincident(g399,g400)
    c: Coincident(g400,g401)
    c: Coincident(g401,g402)
    c: Coincident(g402,g403)
    c: Coincident(g403,g404)
    c: Coincident(g404,g405)
    c: Coincident(g405,g406)
    c: Coincident(g406,g407)
    c: Coincident(g407,g408)
    c: Coincident(g408,g409)
    c: Vertical(g409)
    c: Coincident(g409,g410)
    c: Coincident(g410,g411)
    c: Vertical(g411)
    c: Coincident(g411,g412)
    c: Horizontal(g412)
    c: Coincident(g412,g413)
    c: Coincident(g413,g414)
    c: Horizontal(g414)
    c: Coincident(g414,g415)
    c: Coincident(g415,g416)
    c: Coincident(g416,g417)
    c: Coincident(g417,g418)
    c: Coincident(g418,g419)
    c: Coincident(g419,g420)
    c: Coincident(g420,g421)
    c: Coincident(g421,g422)
    c: Coincident(g422,g423)
    c: Coincident(g423,g424)
    c: Coincident(g424,g425)
    c: Coincident(g425,g426)
    c: Horizontal(g426)
    c: Coincident(g426,g427)
    c: Coincident(g427,g428)
    c: Horizontal(g428)
    c: Coincident(g428,g429)
    c: Coincident(g429,g430)
    c: Coincident(g430,g431)
    c: Coincident(g431,g432)
    c: Horizontal(g432)
    c: Coincident(g432,g433)
    c: Coincident(g433,g434)
    c: Horizontal(g434)
    c: Coincident(g434,g435)
    c: Coincident(g435,g436)
    c: Coincident(g436,g437)
    c: Coincident(g437,g438)
    c: Coincident(g439,g440)
    c: Coincident(g440,g441)
    c: Coincident(g441,g442)
    c: Coincident(g442,g443)
    c: Coincident(g443,g444)
    c: Coincident(g444,g445)
    c: Coincident(g445,g446)
    c: Coincident(g446,g447)
    c: Coincident(g447,g448)
    c: Coincident(g448,g449)
    c: Coincident(g449,g450)
    c: Coincident(g450,g451)
    c: Coincident(g451,g452)
    c: Coincident(g452,g453)
    c: Coincident(g453,g454)
    c: Coincident(g454,g455)
    c: Coincident(g455,g456)
    c: Coincident(g456,g457)
    c: Coincident(g457,g458)
    c: Coincident(g458,g459)
    c: Coincident(g459,g460)
    c: Coincident(g460,g461)
    c: Coincident(g461,g462)
    c: Coincident(g462,g463)
    c: Coincident(g463,g464)
    c: Coincident(g464,g465)
    c: Coincident(g465,g466)
    c: Coincident(g466,g467)
    c: Coincident(g467,g468)
    c: Coincident(g468,g469)
    c: Coincident(g469,g470)
    c: Coincident(g470,g471)
    c: Coincident(g471,g472)
    c: Horizontal(g472)
    c: Coincident(g472,g473)
    c: Coincident(g473,g474)
    c: Coincident(g474,g475)
    c: Coincident(g475,g476)
    c: Coincident(g476,g477)
    c: Coincident(g477,g478)
    c: Coincident(g478,g479)
    c: Coincident(g479,g480)
    c: Coincident(g480,g481)
    c: Coincident(g481,g482)
    c: Coincident(g482,g483)
    c: Coincident(g483,g484)
    c: Coincident(g484,g485)
    c: Coincident(g485,g486)
    c: Coincident(g486,g487)
    c: Coincident(g487,g488)
    c: Vertical(g488)
    c: Coincident(g488,g489)
    c: Coincident(g489,g490)
    c: Vertical(g490)
    c: Coincident(g490,g491)
    c: Coincident(g491,g492)
    c: Coincident(g492,g493)
    c: Coincident(g493,g494)
    c: Coincident(g494,g495)
    c: Coincident(g495,g496)
    c: Coincident(g496,g497)
    c: Coincident(g497,g498)
    c: Coincident(g498,g499)
    c: Coincident(g499,g500)
    c: Coincident(g500,g501)
    c: Coincident(g501,g502)
    c: Coincident(g502,g503)
    c: Coincident(g503,g504)
    c: Horizontal(g370)
    c: Horizontal(g374)
    c: Horizontal(g376)
    c: Vertical(g390)
    c: Vertical(g397)
    c: Vertical(g399)
    c: Vertical(g401)
    c: Vertical(g403)
    c: Vertical(g407)
    c: Horizontal(g410)
    c: Vertical(g413)
    c: Vertical(g415)
    c: Horizontal(g416)
    c: Vertical(g417)
    c: Horizontal(g418)
    c: Vertical(g419)
    c: Vertical(g421)
    c: Vertical(g423)
    c: Vertical(g425)
    c: Vertical(g427)
    c: Vertical(g429)
    c: Horizontal(g420)
    c: Horizontal(g422)
    c: Horizontal(g424)
    c: Vertical(g431)
    c: Vertical(g433)
    c: Vertical(g435)
    c: Horizontal(g436)
    c: Horizontal(g438)
    c: Vertical(g437)
    c: Coincident(g439,g505)
    c: Horizontal(g505)
    c: Coincident(g505,g506)
    c: Coincident(g506,g438)
    c: Vertical(g506)
    c: Horizontal(g464)
    c: Horizontal(g462)
    c: Horizontal(g460)
    c: Horizontal(g458)
    c: Horizontal(g456)
    c: Horizontal(g454)
    c: Horizontal(g452)
    c: Horizontal(g450)
    c: Horizontal(g448)
    c: Horizontal(g446)
    c: Horizontal(g444)
    c: Horizontal(g442)
    c: Horizontal(g440)
    c: Horizontal(g468)
    c: Horizontal(g470)
    c: Horizontal(g474)
    c: Horizontal(g476)
    c: Horizontal(g478)
    c: Vertical(g465)
    c: Horizontal(g466)
    c: Vertical(g475)
    c: Vertical(g477)
    c: Horizontal(g491)
    c: Horizontal(g496)
    c: Horizontal(g494)
    c: Horizontal(g498)
    c: Vertical(g499)
    c: Vertical(g497)
    c: Vertical(g495)
    c: Vertical(g493)
    c: Horizontal(g500)
    c: Horizontal(g502)
    c: Horizontal(g504)
    c: Vertical(g501)
    c: Vertical(g503)
    c: Coincident(g504,g507)
    c: Vertical(g507)
    c: Coincident(g507,g508)
    c: Coincident(g508,g509)
    c: Coincident(g509,g510)
    c: Coincident(g510,g511)
    c: Vertical(g511)
    c: Coincident(g511,g512)
    c: Horizontal(g512)
    c: Coincident(g512,g513)
    c: Vertical(g513)
    c: Coincident(g513,g514)
    c: Coincident(g514,g515)
    c: Vertical(g515)
    c: Coincident(g515,g516)
    c: Horizontal(g516)
    c: Coincident(g516,g517)
    c: Coincident(g517,g518)
    c: Horizontal(g518)
    c: Coincident(g518,g519)
    c: Coincident(g519,g520)
    c: Coincident(g521,g522)
    c: Coincident(g522,g523)
    c: Coincident(g523,g524)
    c: Coincident(g524,g525)
    c: Coincident(g525,g526)
    c: Coincident(g526,g527)
    c: Coincident(g527,g528)
    c: Coincident(g528,g529)
    c: Coincident(g529,g530)
    c: Coincident(g531,g532)
    c: Coincident(g532,g533)
    c: Coincident(g533,g534)
    c: Coincident(g534,g535)
    c: Coincident(g535,g536)
    c: Coincident(g536,g537)
    c: Coincident(g537,g538)
    c: Coincident(g538,g539)
    c: Coincident(g539,g540)
    c: Coincident(g540,g541)
    c: Coincident(g541,g542)
    c: Coincident(g542,g543)
    c: Coincident(g543,g544)
    c: Coincident(g544,g545)
    c: Coincident(g545,g546)
    c: Coincident(g546,g547)
    c: Coincident(g547,g548)
    c: Coincident(g548,g549)
    c: Coincident(g549,g550)
    c: Horizontal(g550)
    c: Coincident(g550,g551)
    c: Coincident(g551,g552)
    c: Coincident(g552,g553)
    c: Coincident(g553,g554)
    c: Horizontal(g554)
    c: Coincident(g554,g555)
    c: Coincident(g555,g556)
    c: Coincident(g556,g557)
    c: Coincident(g557,g558)
    c: Horizontal(g558)
    c: Coincident(g558,g559)
    c: Coincident(g559,g560)
    c: Coincident(g560,g561)
    c: Coincident(g562,g563)
    c: Horizontal(g563)
    c: Coincident(g563,g564)
    c: Coincident(g564,g565)
    c: Coincident(g565,g566)
    c: Coincident(g566,g567)
    c: Horizontal(g567)
    c: Coincident(g567,g568)
    c: Coincident(g568,g569)
    c: Coincident(g569,g570)
    c: Coincident(g570,g571)
    c: Coincident(g571,g572)
    c: Coincident(g572,g573)
    c: Coincident(g573,g574)
    c: Coincident(g574,g575)
    c: Coincident(g575,g576)
    c: Coincident(g576,g577)
    c: Coincident(g577,g578)
    c: Coincident(g578,g579)
    c: Coincident(g579,g580)
    c: Vertical(g580)
    c: Coincident(g580,g581)
    c: Coincident(g581,g582)
    c: Coincident(g582,g583)
    c: Coincident(g583,g584)
    c: Coincident(g584,g585)
    c: Horizontal(g585)
    c: Coincident(g585,g586)
    c: Coincident(g586,g587)
    c: Coincident(g587,g588)
    c: Vertical(g588)
    c: Coincident(g588,g589)
    c: Coincident(g589,g590)
    c: Coincident(g590,g591)
    c: Coincident(g592,g593)
    c: Horizontal(g593)
    c: Coincident(g593,g594)
    c: Coincident(g594,g595)
    c: Coincident(g595,g596)
    c: Vertical(g596)
    c: Coincident(g596,g597)
    c: Horizontal(g597)
    c: Coincident(g597,g598)
    c: Vertical(g598)
    c: Coincident(g598,g599)
    c: Coincident(g599,g600)
    c: Coincident(g600,g601)
    c: Horizontal(g601)
    c: Coincident(g601,g602)
    c: Coincident(g602,g603)
    c: Coincident(g603,g604)
    c: Coincident(g604,g605)
    c: Coincident(g605,g606)
    c: Coincident(g606,g607)
    c: Coincident(g607,g608)
    c: Coincident(g608,g609)
    c: Horizontal(g609)
    c: Coincident(g609,g610)
    c: Coincident(g610,g611)
    c: Coincident(g611,g612)
    c: Coincident(g612,g613)
    c: Vertical(g613)
    c: Coincident(g613,g614)
    c: Coincident(g614,g615)
    c: Vertical(g615)
    c: Coincident(g615,g616)
    c: Coincident(g616,g617)
    c: Vertical(g617)
    c: Coincident(g618,g619)
    c: Vertical(g619)
    c: Coincident(g619,g620)
    c: Coincident(g620,g621)
    c: Coincident(g621,g622)
    c: Coincident(g622,g623)
    c: Coincident(g623,g624)
    c: Coincident(g624,g625)
    c: Coincident(g625,g626)
    c: Coincident(g626,g627)
    c: Vertical(g627)
    c: Coincident(g627,g628)
    c: Coincident(g628,g629)
    c: Coincident(g629,g630)
    c: Coincident(g630,g631)
    c: Coincident(g631,g632)
    c: Coincident(g632,g633)
    c: Vertical(g633)
    c: Coincident(g633,g634)
    c: Coincident(g634,g635)
    c: Vertical(g635)
    c: Coincident(g635,g636)
    c: Coincident(g636,g637)
    c: Coincident(g637,g638)
    c: Coincident(g638,g639)
    c: Coincident(g639,g640)
    c: Horizontal(g640)
    c: Coincident(g640,g641)
    c: Coincident(g641,g642)
    c: Vertical(g642)
    c: Coincident(g642,g643)
    c: Coincident(g643,g644)
    c: Vertical(g644)
    c: Coincident(g644,g645)
    c: Coincident(g645,g646)
    c: Coincident(g646,g647)
    c: Coincident(g647,g648)
    c: Coincident(g648,g649)
    c: Coincident(g649,g650)
    c: Coincident(g650,g651)
    c: Coincident(g651,g652)
    c: Vertical(g652)
    c: Coincident(g652,g653)
    c: Coincident(g653,g654)
    c: Coincident(g654,g655)
    c: Coincident(g655,g656)
    c: Coincident(g656,g657)
    c: Coincident(g657,g658)
    c: Vertical(g658)
    c: Coincident(g658,g659)
    c: Coincident(g659,g660)
    c: Vertical(g660)
    c: Coincident(g660,g661)
    c: Coincident(g661,g662)
    c: Coincident(g662,g663)
    c: Coincident(g663,g664)
    c: Coincident(g664,g665)
    c: Coincident(g665,g666)
    c: Coincident(g666,g667)
    c: Coincident(g667,g668)
    c: Coincident(g668,g669)
    c: Coincident(g669,g670)
    c: Coincident(g670,g671)
    c: Coincident(g671,g672)
    c: Coincident(g672,g673)
    c: Horizontal(g673)
    c: Coincident(g673,g674)
    c: Coincident(g674,g675)
    c: Coincident(g675,g676)
    c: Coincident(g676,g677)
    c: Coincident(g677,g678)
    c: Vertical(g678)
    c: Coincident(g678,g679)
    c: Coincident(g680,g681)
    c: Vertical(g681)
    c: Coincident(g681,g682)
    c: Horizontal(g682)
    c: Coincident(g682,g683)
    c: Coincident(g683,g684)
    c: Coincident(g684,g685)
    c: Coincident(g685,g686)
    c: Coincident(g686,g687)
    c: Vertical(g687)
    c: Coincident(g687,g688)
    c: Coincident(g688,g689)
    c: Coincident(g689,g690)
    c: Coincident(g690,g691)
    c: Coincident(g691,g692)
    c: Coincident(g692,g693)
    c: Coincident(g693,g694)
    c: Horizontal(g694)
    c: Coincident(g694,g695)
    c: Horizontal(g508)
    c: Vertical(g509)
    c: Horizontal(g510)
    c: Vertical(g519)
    c: Vertical(g517)
    c: Horizontal(g520)
    c: Coincident(g520,g696)
    c: Coincident(g696,g697)
    c: Horizontal(g697)
    c: Coincident(g697,g698)
    c: Coincident(g698,g521)
    c: Vertical(g698)
    c: Vertical(g522)
    c: Vertical(g524)
    c: Vertical(g526)
    c: Horizontal(g523)
    c: Horizontal(g525)
    c: Horizontal(g527)
    c: Horizontal(g529)
    c: Horizontal(g532)
    c: Horizontal(g521)
    c: Vertical(g528)
    c: Vertical(g530)
    c: Coincident(g530,g699)
    c: Coincident(g699,g700)
    c: Coincident(g700,g701)
    c: Coincident(g701,g531)
    c: Vertical(g700)
    c: Vertical(g531)
    c: Vertical(g533)
    c: Vertical(g535)
    c: Vertical(g537)
    c: Vertical(g539)
    c: Vertical(g541)
    c: Horizontal(g534)
    c: Horizontal(g536)
    c: Horizontal(g538)
    c: Horizontal(g540)
    c: Horizontal(g542)
    c: Horizontal(g544)
    c: Horizontal(g546)
    c: Horizontal(g699)
    c: Horizontal(g701)
    c: Vertical(g543)
    c: Vertical(g545)
    c: Vertical(g547)
    c: Vertical(g549)
    c: Horizontal(g548)
    c: Vertical(g555)
    c: Vertical(g553)
    c: Vertical(g551)
    c: Horizontal(g552)
    c: Horizontal(g556)
    c: Horizontal(g560)
    c: Vertical(g557)
    c: Vertical(g559)
    c: Vertical(g561)
    c: Coincident(g702,g562)
    c: Coincident(g702,g561)
    c: Horizontal(g565)
    c: Horizontal(g569)
    c: Horizontal(g571)
    c: Horizontal(g573)
    c: Horizontal(g575)
    c: Horizontal(g702)
    c: Vertical(g566)
    c: Vertical(g568)
    c: Vertical(g570)
    c: Vertical(g572)
    c: Vertical(g574)
    c: Vertical(g576)
    c: Vertical(g578)
    c: Vertical(g582)
    c: Vertical(g584)
    c: Horizontal(g577)
    c: Horizontal(g579)
    c: Horizontal(g581)
    c: Horizontal(g583)
    c: Horizontal(g587)
    c: Horizontal(g589)
    c: Horizontal(g591)
    c: Coincident(g591,g592)
    c: Vertical(g590)
    c: Vertical(g592)
    c: Vertical(g594)
    c: Vertical(g602)
    c: Vertical(g604)
    c: Horizontal(g595)
    c: Horizontal(g599)
    c: Horizontal(g605)
    c: Horizontal(g607)
    c: Vertical(g608)
    c: Vertical(g611)
    c: Horizontal(g612)
    c: Horizontal(g614)
    c: Horizontal(g620)
    c: Horizontal(g622)
    c: Vertical(g621)
    c: Vertical(g623)
    c: Coincident(g618,g703)
    c: Vertical(g703)
    c: Coincident(g703,g704)
    c: Horizontal(g704)
    c: Coincident(g704,g617)
    c: Horizontal(g624)
    c: Vertical(g625)
    c: Horizontal(g643)
    c: Horizontal(g645)
    c: Horizontal(g647)
    c: Horizontal(g649)
    c: Horizontal(g651)
    c: Horizontal(g653)
    c: Horizontal(g655)
    c: Horizontal(g657)
    c: Horizontal(g659)
    c: Vertical(g656)
    c: Vertical(g654)
    c: Vertical(g650)
    c: Vertical(g648)
    c: Vertical(g646)
    c: Vertical(g637)
    c: Vertical(g639)
    c: Horizontal(g661)
    c: Horizontal(g663)
    c: Horizontal(g665)
    c: Horizontal(g667)
    c: Horizontal(g669)
    c: Horizontal(g671)
    c: Horizontal(g675)
    c: Vertical(g662)
    c: Vertical(g664)
    c: Vertical(g666)
    c: Vertical(g668)
    c: Vertical(g670)
    c: Vertical(g672)
    c: Vertical(g674)
    c: Vertical(g676)
    c: Horizontal(g677)
    c: Horizontal(g679)
    c: Coincident(g679,g705)
    c: Vertical(g705)
    c: Coincident(g705,g706)
    c: Horizontal(g706)
    c: Coincident(g706,g707)
    c: Coincident(g680,g707)
    c: Horizontal(g680)
    c: Vertical(g707)
    c: Vertical(g691)
    c: Vertical(g693)
    c: Vertical(g689)
    c: Vertical(g685)
    c: Vertical(g683)
    c: Horizontal(g686)
    c: Horizontal(g688)
    c: Horizontal(g690)
    c: Horizontal(g692)
    c: Horizontal(g684)
    c: Vertical(g695)
    c: Coincident(g695,g708)
    c: Coincident(g708,g709)
    c: Coincident(g709,g710)
    c: Coincident(g710,g711)
    c: Coincident(g711,g712)
    c: Coincident(g712,g713)
    c: Horizontal(g713)
    c: Coincident(g713,g714)
    c: Coincident(g714,g715)
    c: Coincident(g715,g716)
    c: Coincident(g716,g717)
    c: Coincident(g718,g719)
    c: Horizontal(g720)
    c: Coincident(g721,g722)
    c: Coincident(g722,g723)
    c: Coincident(g723,g724)
    c: Horizontal(g724)
    c: Coincident(g724,g725)
    c: Horizontal(g726)
    c: Coincident(g726,g727)
    c: Coincident(g727,g728)
    c: Horizontal(g728)
    c: Coincident(g728,g729)
    c: Coincident(g729,g730)
    c: Coincident(g730,g731)
    c: Coincident(g731,g732)
    c: Coincident(g732,g733)
    c: Coincident(g733,g734)
    c: Coincident(g734,g735)
    c: Coincident(g735,g736)
    c: Coincident(g736,g737)
    c: Coincident(g737,g738)
    c: Coincident(g738,g739)
    c: Coincident(g739,g740)
    c: Coincident(g740,g741)
    c: Coincident(g741,g742)
    c: Coincident(g742,g743)
    c: Coincident(g743,g744)
    c: Coincident(g744,g745)
    c: Coincident(g745,g746)
    c: Coincident(g746,g747)
    c: Coincident(g747,g748)
    c: Coincident(g748,g749)
    c: Coincident(g749,g750)
    c: Coincident(g750,g751)
    c: Coincident(g751,g752)
    c: Coincident(g752,g753)
    c: Coincident(g753,g754)
    c: Coincident(g754,g755)
    c: Coincident(g755,g756)
    c: Coincident(g756,g757)
    c: Coincident(g757,g758)
    c: Coincident(g760,g761)
    c: Coincident(g761,g762)
    c: Coincident(g762,g763)
    c: Coincident(g763,g764)
    c: Coincident(g765,g766)
    c: Coincident(g766,g767)
    c: Coincident(g767,g768)
    c: Coincident(g769,g770)
    c: Coincident(g770,g771)
    c: Coincident(g772,g773)
    c: Coincident(g773,g774)
    c: Coincident(g774,g775)
    c: Coincident(g775,g776)
    c: Coincident(g776,g777)
    c: Coincident(g777,g778)
    c: Coincident(g778,g779)
    c: Coincident(g779,g780)
    c: Coincident(g780,g781)
    c: Coincident(g781,g782)
    c: Coincident(g782,g783)
    c: Coincident(g783,g784)
    c: Coincident(g784,g785)
    c: Coincident(g785,g786)
    c: Horizontal(g787)
    c: Coincident(g787,g788)
    c: Coincident(g788,g789)
    c: Coincident(g789,g790)
    c: Coincident(g790,g791)
    c: Horizontal(g791)
    c: Coincident(g791,g792)
    c: Coincident(g792,g793)
    c: Horizontal(g793)
    c: Coincident(g793,g794)
    c: Coincident(g794,g795)
    c: Coincident(g795,g796)
    c: Vertical(g796)
    c: Coincident(g796,g797)
    c: Horizontal(g797)
    c: Coincident(g797,g798)
    c: Coincident(g798,g799)
    c: Horizontal(g799)
    c: Coincident(g799,g800)
    c: Coincident(g800,g801)
    c: Coincident(g801,g802)
    c: Coincident(g802,g803)
    c: Horizontal(g803)
    c: Vertical(g804)
    c: Coincident(g804,g805)
    c: Coincident(g805,g806)
    c: Coincident(g806,g807)
    c: Coincident(g807,g808)
    c: Coincident(g808,g809)
    c: Coincident(g809,g810)
    c: Vertical(g810)
    c: Coincident(g810,g811)
    c: Coincident(g811,g812)
    c: Coincident(g812,g813)
    c: Coincident(g813,g814)
    c: Coincident(g814,g815)
    c: Horizontal(g815)
    c: Coincident(g815,g816)
    c: Coincident(g816,g817)
    c: Coincident(g817,g818)
    c: Coincident(g818,g819)
    c: Coincident(g819,g820)
    c: Coincident(g820,g821)
    c: Horizontal(g821)
    c: Coincident(g821,g822)
    c: Vertical(g822)
    c: Coincident(g822,g823)
    c: Coincident(g823,g824)
    c: Coincident(g824,g825)
    c: Horizontal(g825)
    c: Coincident(g825,g826)
    c: Coincident(g826,g827)
    c: Coincident(g827,g828)
    c: Coincident(g828,g829)
    c: Horizontal(g829)
    c: Coincident(g829,g830)
    c: Coincident(g830,g831)
    c: Coincident(g831,g832)
    c: Coincident(g832,g833)
    c: Horizontal(g834)
    c: Coincident(g834,g835)
    c: Coincident(g835,g836)
    c: Horizontal(g836)
    c: Coincident(g836,g837)
    c: Coincident(g837,g838)
    c: Horizontal(g838)
    c: Coincident(g838,g839)
    c: Coincident(g839,g840)
    c: Coincident(g840,g841)
    c: Coincident(g841,g842)
    c: Coincident(g842,g843)
    c: Coincident(g843,g844)
    c: Coincident(g844,g845)
    c: Coincident(g845,g846)
    c: Coincident(g846,g847)
    c: Coincident(g847,g848)
    c: Horizontal(g848)
    c: Coincident(g848,g849)
    c: Coincident(g849,g850)
    c: Coincident(g850,g851)
    c: Coincident(g851,g852)
    c: Coincident(g852,g853)
    c: Coincident(g853,g854)
    c: Coincident(g854,g855)
    c: Coincident(g855,g856)
    c: Coincident(g856,g857)
    c: Coincident(g857,g858)
    c: Horizontal(g858)
    c: Coincident(g858,g859)
    c: Coincident(g859,g860)
    c: Coincident(g860,g861)
    c: Coincident(g861,g862)
    c: Coincident(g862,g863)
    c: Coincident(g863,g864)
    c: Coincident(g786,g865)
    c: Coincident(g865,g866)
    c: Coincident(g866,g787)
    c: Vertical(g866)
    c: Horizontal(g709)
    c: Horizontal(g711)
    c: Horizontal(g715)
    c: Horizontal(g717)
    c: Horizontal(g719)
    c: Horizontal(g722)
    c: Coincident(g718,g867)
    c: Horizontal(g867)
    c: Coincident(g867,g868)
    c: Coincident(g868,g717)
    c: Coincident(g721,g869)
    c: Coincident(g869,g870)
    c: Coincident(g720,g870)
    c: Coincident(g871,g720)
    c: Coincident(g871,g719)
    c: Vertical(g871)
    c: Vertical(g870)
    c: Vertical(g723)
    c: Horizontal(g869)
    c: Coincident(g872,g726)
    c: Coincident(g873,g872)
    c: Coincident(g725,g873)
    c: Horizontal(g873)
    c: Horizontal(g736)
    c: Horizontal(g734)
    c: Horizontal(g732)
    c: Horizontal(g730)
    c: Horizontal(g738)
    c: Horizontal(g740)
    c: Horizontal(g742)
    c: Horizontal(g744)
    c: Horizontal(g746)
    c: Horizontal(g748)
    c: Horizontal(g750)
    c: Horizontal(g752)
    c: Horizontal(g754)
    c: Coincident(g758,g759)
    c: Horizontal(g756)
    c: Horizontal(g758)
    c: Coincident(g874,g759)
    c: Horizontal(g874)
    c: Coincident(g875,g760)
    c: Coincident(g875,g874)
    c: Horizontal(g760)
    c: Vertical(g762)
    c: Coincident(g765,g764)
    c: Vertical(g764)
    c: Vertical(g766)
    c: Vertical(g768)
    c: Coincident(g769,g768)
    c: Vertical(g770)
    c: Coincident(g876,g771)
    c: Coincident(g877,g772)
    c: Coincident(g877,g876)
    c: Vertical(g772)
    c: Vertical(g774)
    c: Vertical(g776)
    c: Vertical(g778)
    c: Vertical(g780)
    c: Vertical(g782)
    c: Vertical(g876)
    c: Horizontal(g773)
    c: Horizontal(g775)
    c: Horizontal(g777)
    c: Horizontal(g779)
    c: Horizontal(g781)
    c: Horizontal(g783)
    c: Horizontal(g785)
    c: Horizontal(g865)
    c: Vertical(g784)
    c: Vertical(g786)
    c: Vertical(g788)
    c: Vertical(g790)
    c: Horizontal(g789)
    c: Vertical(g792)
    c: Vertical(g794)
    c: Horizontal(g795)
    c: Vertical(g798)
    c: Vertical(g800)
    c: Vertical(g802)
    c: Horizontal(g801)
    c: Coincident(g804,g803)
    c: Horizontal(g805)
    c: Horizontal(g807)
    c: Horizontal(g809)
    c: Vertical(g806)
    c: Vertical(g808)
    c: Vertical(g812)
    c: Vertical(g816)
    c: Vertical(g814)
    c: Vertical(g818)
    c: Vertical(g820)
    c: Vertical(g824)
    c: Vertical(g826)
    c: Vertical(g828)
    c: Vertical(g830)
    c: Vertical(g832)
    c: Horizontal(g827)
    c: Horizontal(g823)
    c: Horizontal(g819)
    c: Horizontal(g817)
    c: Horizontal(g831)
    c: Horizontal(g833)
    c: Coincident(g878,g833)
    c: Coincident(g878,g834)
    c: Vertical(g837)
    c: Horizontal(g840)
    c: Horizontal(g842)
    c: Horizontal(g846)
    c: Horizontal(g850)
    c: Horizontal(g852)
    c: Horizontal(g854)
    c: Horizontal(g856)
    c: Horizontal(g860)
    c: Horizontal(g862)
    c: Horizontal(g864)
    c: Horizontal(g844)
    c: Coincident(g864,g879)
    c: Coincident(g879,g880)
    c: Coincident(g880,g881)
    c: Coincident(g881,g882)
    c: Horizontal(g882)
    c: Coincident(g883,g1)
    c: Coincident(g883,g0)
    c: Vertical(g883)
    c: Coincident(g0,g882)
    c: Coincident(g1,g2)
    c: Coincident(g3,g4)
    c: Coincident(g4,g5)
    c: Coincident(g5,g6)
    c: Coincident(g6,g7)
    c: Coincident(g13,g14)
    c: Coincident(g14,g15)
    c: Coincident(g16,g17)
    c: Coincident(g18,g19)
    c: Coincident(g22,g23)
    c: Coincident(g24,g25)
    c: Coincident(g27,g28)
    c: Vertical(g26)
    c: Coincident(g28,g29)
    c: Coincident(g30,g31)
    c: Horizontal(g29)
    c: Coincident(g37,g38)
    c: Coincident(g38,g39)
    c: Coincident(g39,g40)
    c: Coincident(g40,g41)
    c: Coincident(g42,g43)
    c: Coincident(g20,g21)
    c: Coincident(g21,g22)
    c: Coincident(g25,g26)
    c: Coincident(g48,g49)
    c: Coincident(g49,g50)
    c: Coincident(g58,g59)
    c: Horizontal(g59)
    c: Coincident(g61,g62)
    c: Coincident(g64,g65)
    c: Coincident(g65,g66)
    c: Coincident(g66,g67)
    c: Coincident(g68,g69)
    c: Coincident(g70,g71)
    c: Coincident(g72,g73)
    c: Coincident(g74,g75)
    c: Coincident(g86,g87)
    c: Coincident(g87,g88)
    c: Coincident(g92,g93)
    c: Coincident(g94,g95)
    c: Coincident(g96,g97)
    c: Coincident(g51,g52)
    c: Coincident(g62,g63)
    c: Coincident(g76,g77)
    c: Coincident(g77,g78)
    c: Coincident(g82,g83)
    c: Coincident(g83,g84)
FEATURE [Part::Extrusion] Extrude037  label="logoCut"
  Base = -> Sketch055
  Dir = (0,1,0)
  DirMode = 0
  FaceMakerClass = Part::FaceMakerBullseye
  LengthFwd = 10
  LengthRev = 0
  Placement = pos=(-39,-248,-165) rot=(0,0,1;0rad)
  Solid = true
  Symmetric = false
FEATURE [Part::Cut] Cut056  label="level4to5"
  Base = -> Fillet004
  Tool = -> Extrude037
FEATURE [Sketcher::SketchObject] Sketch056
  FullyConstrained = true
  sketch-geometry (4):
    g0: ArcOfCircle CenterX=0 CenterY=-150 CenterZ=0 NormalX=0 NormalY=0 NormalZ=1 AngleXU=0 Radius=93.5 StartAngle=4.49682 EndAngle=4.92796
    g1: LineSegment StartX=-20 StartY=-241.336 StartZ=0 EndX=-20 EndY=-237.336 EndZ=0
    g2: LineSegment StartX=-20 StartY=-237.336 StartZ=0 EndX=20 EndY=-237.336 EndZ=0
    g3: LineSegment StartX=20 StartY=-237.336 StartZ=0 EndX=20 EndY=-241.336 EndZ=0
  constraints (13):
    c: PointOnObject(g0,g-2)
    c: DistanceY(g0) = -150
    c: DistanceX(g0,g0) = 20
    c: DistanceX(g0,g0) = 20
    c: Diameter(g0) = 187
    c: Coincident(g1,g0)
    c: Horizontal(g2)
    c: Coincident(g3,g2)
    c: Coincident(g3,g0)
    c: Vertical(g3)
    c: Vertical(g1)
    c: Coincident(g1,g2)
    c: DistanceY(g0,g2) = 4
FEATURE [Part::Extrusion] Extrude038  label="logoAttach"
  Base = -> Sketch056
  Dir = (0,0,1)
  DirMode = 2
  FaceMakerClass = Part::FaceMakerBullseye
  LengthFwd = 28
  LengthRev = 0
  Placement = pos=(0,0,-160) rot=(0,0,1;0rad)
  Solid = true
  Symmetric = false
FEATURE [Part::Cylinder] Cylinder157
  Angle = 360
  AttacherType = Attacher::AttachEngine3D
  FirstAngle = 0
  Height = 10
  Placement = pos=(0,-238,-147.25) rot=(1,0,0;1.5708rad)
  Radius = 2
  SecondAngle = 0
FEATURE [Part::MultiFuse] Fusion105  label="logoAttach001"
  Shapes = -> [Extrude038,Cylinder157]
